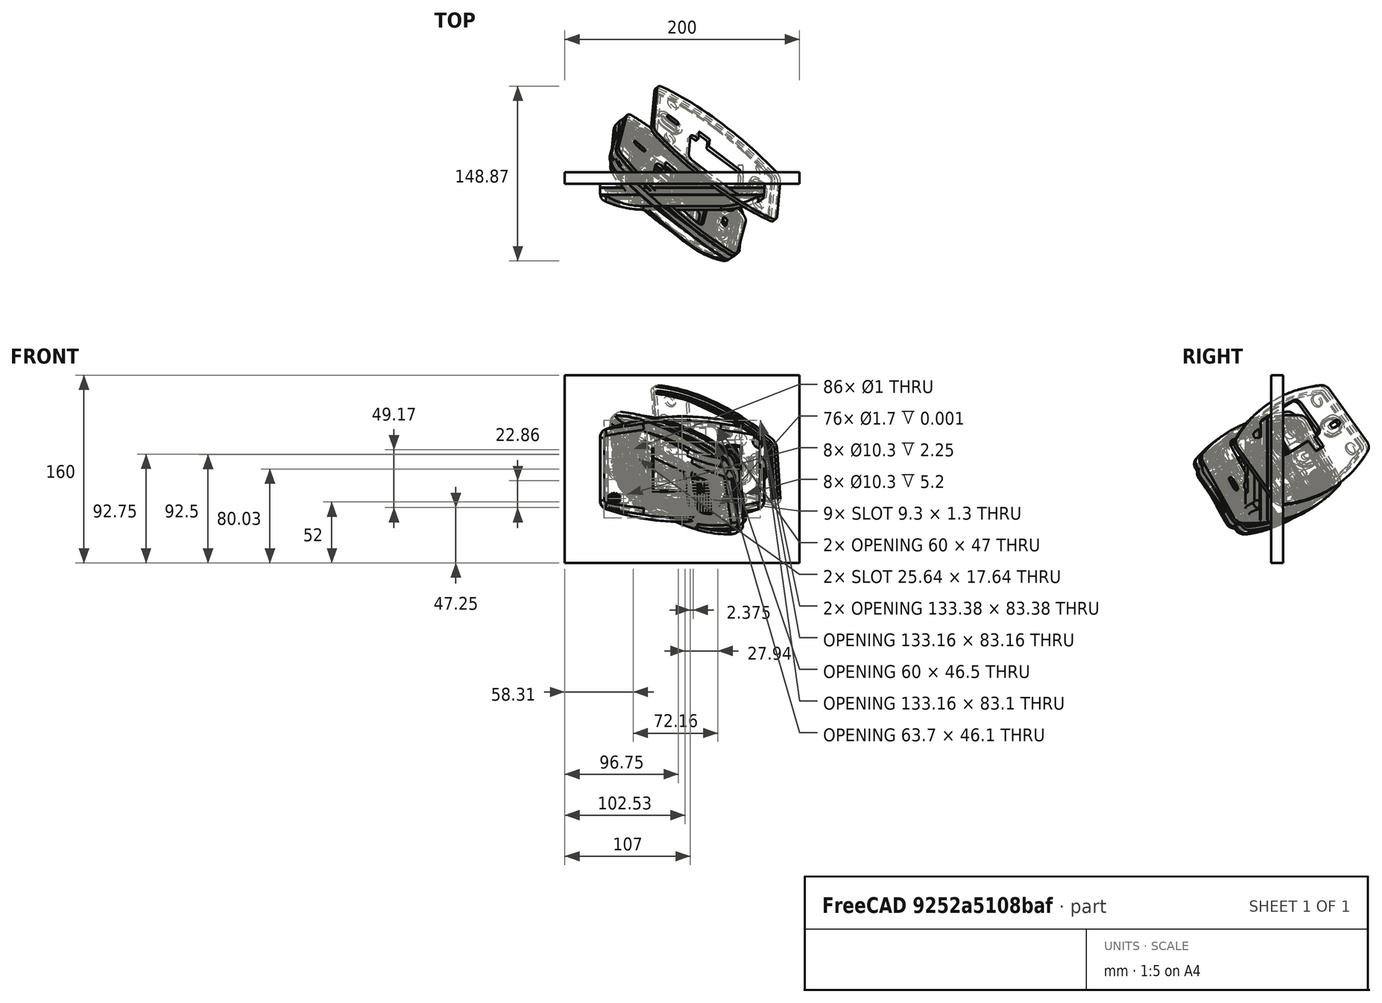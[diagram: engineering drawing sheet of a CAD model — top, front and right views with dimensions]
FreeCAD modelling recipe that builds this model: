
FCSTD DOCUMENT  (FreeCAD 0.19R24291 (Git))
Label: _RoomThermostat
License: All rights reserved
LicenseURL: http://en.wikipedia.org/wiki/All_rights_reserved
objects: Sketcher::SketchObject×100, PartDesign::Pocket×28, PartDesign::Body×26, Part::Feature×23, PartDesign::Pad×20, PartDesign::Mirrored×16, PartDesign::Revolution×11, Part::FeaturePython×10, PartDesign::LinearPattern×6, Part::Compound×6, PartDesign::SubtractivePipe×6, PartDesign::MultiTransform×5, PartDesign::Fillet×5, PartDesign::SubtractiveLoft×5, PartDesign::AdditivePipe×4, PartDesign::Groove×4, PartDesign::PolarPattern×4, PartDesign::AdditiveLoft×3, Drawing::FeatureViewPart×3, PartDesign::Plane×2, +2 more types
note: 371 computed .brp shape members not serialized (recipe doc carries the construction recipe); baked Part::Feature solids carry a one-line shape summary decoded from their .brp

FEATURE [Part::Feature] Part__Feature  label="MH-ET_LIVE_MiniKit"
  Placement = pos=(16.5,-5,-21) rot=(0,0,1;3.14159rad)
  shape: bbox 31.02 x 99.68 x 39.44 mm, 5494 faces, 23 solids (baked)
FEATURE [Sketcher::SketchObject] Sketch  label="gl base"
  FullyConstrained = false
  MapMode = 5
  Placement = pos=(0,0,0) rot=(1,0,0;1.5708rad)
  Support = -> [XZ_Plane]
  sketch-geometry (8):
    g0: LineSegment StartX=-33.28 StartY=21.36 StartZ=0 EndX=26.98 EndY=21.36 EndZ=0
    g1: LineSegment StartX=26.98 StartY=21.36 StartZ=0 EndX=26.98 EndY=-21.36 EndZ=0
    g2: LineSegment StartX=26.98 StartY=-21.36 StartZ=0 EndX=-33.28 EndY=-21.36 EndZ=0
    g3: LineSegment StartX=-33.28 StartY=-21.36 StartZ=0 EndX=-33.28 EndY=21.36 EndZ=0
    g4: LineSegment StartX=-24.48 StartY=18.36 StartZ=0 EndX=24.48 EndY=18.36 EndZ=0
    g5: LineSegment StartX=24.48 StartY=18.36 StartZ=0 EndX=24.48 EndY=-18.36 EndZ=0
    g6: LineSegment StartX=24.48 StartY=-18.36 StartZ=0 EndX=-24.48 EndY=-18.36 EndZ=0
    g7: LineSegment StartX=-24.48 StartY=-18.36 StartZ=0 EndX=-24.48 EndY=18.36 EndZ=0
  constraints (21):
    c: Coincident(g0,g1)
    c: Coincident(g1,g2)
    c: Coincident(g2,g3)
    c: Coincident(g3,g0)
    c: Horizontal(g2)
    c: Vertical(g3)
    c: DistanceX(g0,g0) = 60.26
    c: DistanceY(g1,g1) = 42.72
    c: Coincident(g4,g5)
    c: Coincident(g5,g6)
    c: Coincident(g6,g7)
    c: Coincident(g7,g4)
    c: Horizontal(g6)
    c: Vertical(g7)
    c: Horizontal(g0)
    c: Symmetric(g4,g4,g-2)
    c: Symmetric(g4,g5,g-1)
    c: DistanceX(g4,g4) = 48.96
    c: DistanceX(g4,g0) = 2.5
    c: DistanceY(g5,g5) = 36.72
    c: Symmetric(g0,g1,g-1)
FEATURE [PartDesign::Pad] Pad  label="GL Base"
  Direction = (1,1,1)
  Length = 4.2
  Length2 = 100
  Placement = pos=(0,0,0) rot=(1,0,0;1.5708rad)
  Profile = -> Sketch
  Reversed = true
  Type = 0
FEATURE [Sketcher::SketchObject] Sketch001  label="gl active area"
  FullyConstrained = false
  MapMode = 5
  Placement = pos=(0,0,0) rot=(1,0,0;1.5708rad)
  Support = -> [XZ_Plane]
  sketch-geometry (4):
    g0: LineSegment StartX=-24.48 StartY=18.36 StartZ=0 EndX=24.48 EndY=18.36 EndZ=0
    g1: LineSegment StartX=24.48 StartY=18.36 StartZ=0 EndX=24.48 EndY=-18.36 EndZ=0
    g2: LineSegment StartX=24.48 StartY=-18.36 StartZ=0 EndX=-24.48 EndY=-18.36 EndZ=0
    g3: LineSegment StartX=-24.48 StartY=-18.36 StartZ=0 EndX=-24.48 EndY=18.36 EndZ=0
  constraints (10):
    c: Coincident(g0,g1)
    c: Coincident(g1,g2)
    c: Coincident(g2,g3)
    c: Coincident(g3,g0)
    c: Horizontal(g2)
    c: Vertical(g3)
    c: Symmetric(g0,g0,g-2)
    c: Symmetric(g0,g1,g-1)
    c: DistanceY(g1,g1) = 36.72
    c: DistanceX(g0,g0) = 48.96
FEATURE [PartDesign::Pad] Pad001  label="GL active area"
  BaseFeature = -> Pad
  Direction = (1,1,1)
  Length = 0.1
  Length2 = 100
  Placement = pos=(0,0,0) rot=(1,0,0;1.5708rad)
  Profile = -> Sketch001
  Type = 0
FEATURE [PartDesign::Body] Body  label="Glass"
  Group = -> [Sketch,Pad,Sketch001,Pad001]
  Origin = -> Origin
  Tip = -> Pad001
FEATURE [Sketcher::SketchObject] Sketch003  label="pc skeleton"
  FullyConstrained = false
  MapMode = 5
  Placement = pos=(0,0,0) rot=(1,0,0;1.5708rad)
  Support = -> [XZ_Plane001]
  sketch-geometry (8):
    g0: LineSegment StartX=-33.28 StartY=21.36 StartZ=0 EndX=26.98 EndY=21.36 EndZ=0
    g1: LineSegment StartX=26.98 StartY=21.36 StartZ=0 EndX=26.98 EndY=-21.36 EndZ=0
    g2: LineSegment StartX=26.98 StartY=-21.36 StartZ=0 EndX=-33.28 EndY=-21.36 EndZ=0
    g3: LineSegment StartX=-33.28 StartY=-21.36 StartZ=0 EndX=-33.28 EndY=21.36 EndZ=0
    g4: LineSegment StartX=-24.48 StartY=18.36 StartZ=0 EndX=24.48 EndY=18.36 EndZ=0
    g5: LineSegment StartX=24.48 StartY=18.36 StartZ=0 EndX=24.48 EndY=-18.36 EndZ=0
    g6: LineSegment StartX=24.48 StartY=-18.36 StartZ=0 EndX=-24.48 EndY=-18.36 EndZ=0
    g7: LineSegment StartX=-24.48 StartY=-18.36 StartZ=0 EndX=-24.48 EndY=18.36 EndZ=0
  constraints (21):
    c: Coincident(g0,g1)
    c: Coincident(g1,g2)
    c: Coincident(g2,g3)
    c: Coincident(g3,g0)
    c: Horizontal(g2)
    c: Vertical(g3)
    c: DistanceX(g0,g0) = 60.26
    c: DistanceY(g1,g1) = 42.72
    c: Coincident(g4,g5)
    c: Coincident(g5,g6)
    c: Coincident(g6,g7)
    c: Coincident(g7,g4)
    c: Horizontal(g6)
    c: Vertical(g7)
    c: Horizontal(g0)
    c: Symmetric(g4,g4,g-2)
    c: Symmetric(g4,g5,g-1)
    c: DistanceX(g4,g4) = 48.96
    c: DistanceX(g4,g0) = 2.5
    c: DistanceY(g5,g5) = 36.72
    c: Symmetric(g0,g1,g-1)
FEATURE [Sketcher::SketchObject] Sketch002  label="pc base"
  AttachmentOffset = pos=(0,0,-4.2) rot=(0,0,1;0rad)
  ExternalGeometry = -> [Sketch003]
  FullyConstrained = false
  MapMode = 5
  Placement = pos=(0,4.2,9e-16) rot=(1,0,0;1.5708rad)
  Support = -> [XZ_Plane001]
  sketch-geometry (12):
    g0: LineSegment StartX=33.49 StartY=21.45 StartZ=0 EndX=-43.69 EndY=21.45 EndZ=0
    g1: LineSegment StartX=-43.69 StartY=21.45 StartZ=0 EndX=-43.69 EndY=-21.45 EndZ=0
    g2: LineSegment StartX=-43.69 StartY=-21.45 StartZ=0 EndX=33.49 EndY=-21.45 EndZ=0
    g3: LineSegment StartX=33.49 StartY=-21.45 StartZ=0 EndX=33.49 EndY=21.45 EndZ=0
    g4: LineSegment StartX=-36.77 StartY=18.45 StartZ=0 EndX=30.49 EndY=18.45 EndZ=0
    g5: LineSegment StartX=30.49 StartY=18.45 StartZ=0 EndX=30.49 EndY=-18.45 EndZ=0
    g6: LineSegment StartX=30.49 StartY=-18.45 StartZ=0 EndX=-36.77 EndY=-18.45 EndZ=0
    g7: LineSegment StartX=-36.77 StartY=-18.45 StartZ=0 EndX=-36.77 EndY=18.45 EndZ=0
    g8: Circle CenterX=30.49 CenterY=18.45 CenterZ=0 NormalX=0 NormalY=0 NormalZ=1 AngleXU=0 Radius=1.5
    g9: Circle CenterX=30.49 CenterY=-18.45 CenterZ=0 NormalX=0 NormalY=0 NormalZ=1 AngleXU=0 Radius=1.5
    g10: Circle CenterX=-36.77 CenterY=-18.45 CenterZ=0 NormalX=0 NormalY=0 NormalZ=1 AngleXU=0 Radius=1.5
    g11: Circle CenterX=-36.77 CenterY=18.45 CenterZ=0 NormalX=0 NormalY=0 NormalZ=1 AngleXU=0 Radius=1.5
  constraints (30):
    c: Coincident(g0,g1)
    c: Coincident(g1,g2)
    c: Coincident(g2,g3)
    c: Coincident(g3,g0)
    c: Horizontal(g0)
    c: Horizontal(g2)
    c: Vertical(g1)
    c: Symmetric(g0,g2,g-1)
    c: DistanceX(g0,g-3) = 10.41
    c: DistanceX(g0,g0) = 77.18
    c: DistanceY(g3,g3) = 42.9
    c: Coincident(g4,g5)
    c: Coincident(g5,g6)
    c: Coincident(g6,g7)
    c: Coincident(g7,g4)
    c: Horizontal(g4)
    c: Horizontal(g6)
    c: Vertical(g7)
    c: Symmetric(g4,g5,g-1)
    c: Coincident(g8,g4)
    c: Coincident(g9,g5)
    c: Coincident(g10,g6)
    c: Coincident(g11,g4)
    c: Equal(g8,g11)
    c: Equal(g11,g10)
    c: Equal(g10,g9)
    c: Radius(g9) = 1.5
    c: DistanceX(g0,g11) = 6.92
    c: DistanceX(g8,g0) = 3
    c: DistanceY(g8,g0) = 3
FEATURE [PartDesign::Pad] Pad002  label="PC base"
  Direction = (1,1,1)
  Length = 1.6
  Length2 = 100
  Placement = pos=(0,0,0) rot=(1,0,0;1.5708rad)
  Profile = -> Sketch002
  Reversed = true
  Type = 0
FEATURE [Sketcher::SketchObject] Sketch004  label="pc hole"
  ExternalGeometry = -> [Sketch002]
  FullyConstrained = false
  MapMode = 5
  Placement = pos=(0,0,0) rot=(1,0,0;1.5708rad)
  Support = -> [XZ_Plane001]
  sketch-geometry (1):
    g0: Circle CenterX=-41.69 CenterY=-16.6 CenterZ=0 NormalX=0 NormalY=0 NormalZ=1 AngleXU=0 Radius=0.5
  constraints (3):
    c: DistanceX(g-3,g0) = 2
    c: DistanceY(g-3,g0) = 4.85
    c: Radius(g0) = 0.5
FEATURE [PartDesign::Pocket] Pocket  label="PC FirstHole"
  BaseFeature = -> Pad002
  Length = 5
  Length2 = 100
  Midplane = true
  Placement = pos=(0,0,0) rot=(1,0,0;1.5708rad)
  Profile = -> Sketch004
  Type = 1
FEATURE [PartDesign::LinearPattern] LinearPattern  label="PC OtherHoles"
  BaseFeature = -> Pocket
  Direction = -> Z_Axis001
  Length = 33.02
  Occurrences = 14
  Originals = -> [Pocket]
  Placement = pos=(0,0,0) rot=(1,0,0;1.5708rad)
FEATURE [PartDesign::Body] Body001  label="PCB"
  Group = -> [Sketch002,Sketch003,Pad002,Sketch004,Pocket,LinearPattern]
  Origin = -> Origin001
  Tip = -> LinearPattern
FEATURE [Sketcher::SketchObject] Sketch006  label="sd skeleton"
  FullyConstrained = false
  MapMode = 5
  Placement = pos=(0,0,0) rot=(1,0,0;1.5708rad)
  Support = -> [XZ_Plane002]
  sketch-geometry (8):
    g0: LineSegment StartX=-33.28 StartY=21.36 StartZ=0 EndX=26.98 EndY=21.36 EndZ=0
    g1: LineSegment StartX=26.98 StartY=21.36 StartZ=0 EndX=26.98 EndY=-21.36 EndZ=0
    g2: LineSegment StartX=26.98 StartY=-21.36 StartZ=0 EndX=-33.28 EndY=-21.36 EndZ=0
    g3: LineSegment StartX=-33.28 StartY=-21.36 StartZ=0 EndX=-33.28 EndY=21.36 EndZ=0
    g4: LineSegment StartX=-24.48 StartY=18.36 StartZ=0 EndX=24.48 EndY=18.36 EndZ=0
    g5: LineSegment StartX=24.48 StartY=18.36 StartZ=0 EndX=24.48 EndY=-18.36 EndZ=0
    g6: LineSegment StartX=24.48 StartY=-18.36 StartZ=0 EndX=-24.48 EndY=-18.36 EndZ=0
    g7: LineSegment StartX=-24.48 StartY=-18.36 StartZ=0 EndX=-24.48 EndY=18.36 EndZ=0
  constraints (21):
    c: Coincident(g0,g1)
    c: Coincident(g1,g2)
    c: Coincident(g2,g3)
    c: Coincident(g3,g0)
    c: Horizontal(g2)
    c: Vertical(g3)
    c: DistanceX(g0,g0) = 60.26
    c: DistanceY(g1,g1) = 42.72
    c: Coincident(g4,g5)
    c: Coincident(g5,g6)
    c: Coincident(g6,g7)
    c: Coincident(g7,g4)
    c: Horizontal(g6)
    c: Vertical(g7)
    c: Horizontal(g0)
    c: Symmetric(g4,g4,g-2)
    c: Symmetric(g4,g5,g-1)
    c: DistanceX(g4,g4) = 48.96
    c: DistanceX(g4,g0) = 2.5
    c: DistanceY(g5,g5) = 36.72
    c: Symmetric(g0,g1,g-1)
FEATURE [Sketcher::SketchObject] Sketch005  label="sd base"
  AttachmentOffset = pos=(0,0,-5.8) rot=(0,0,1;0rad)
  ExternalGeometry = -> [Sketch006]
  FullyConstrained = false
  MapMode = 5
  Placement = pos=(0,5.8,1.3e-15) rot=(1,0,0;1.5708rad)
  Support = -> [XZ_Plane002]
  sketch-geometry (6):
    g0: LineSegment StartX=-16.02 StartY=19.96 StartZ=0 EndX=10.58 EndY=19.96 EndZ=0
    g1: LineSegment StartX=10.58 StartY=19.96 StartZ=0 EndX=10.58 EndY=10.96 EndZ=0
    g2: LineSegment StartX=8.48 StartY=3.26 StartZ=0 EndX=-16.02 EndY=3.26 EndZ=0
    g3: LineSegment StartX=-16.02 StartY=3.26 StartZ=0 EndX=-16.02 EndY=19.96 EndZ=0
    g4: LineSegment StartX=10.58 StartY=10.96 StartZ=0 EndX=8.48 EndY=8.86 EndZ=0
    g5: LineSegment StartX=8.48 StartY=8.86 StartZ=0 EndX=8.48 EndY=3.26 EndZ=0
  constraints (18):
    c: Coincident(g0,g1)
    c: Coincident(g2,g3)
    c: Coincident(g3,g0)
    c: Horizontal(g0)
    c: Horizontal(g2)
    c: Vertical(g1)
    c: Vertical(g3)
    c: DistanceX(g0,g-3) = 16.4
    c: DistanceX(g0,g0) = 26.6
    c: DistanceY(g0,g-3) = 1.4
    c: Coincident(g4,g5)
    c: Vertical(g5)
    c: Coincident(g2,g5)
    c: Coincident(g4,g1)
    c: DistanceY(g2,g0) = 16.7
    c: DistanceX(g2,g2) = 24.5
    c: DistanceY(g5,g5) = 5.6
    c: Angle(g5,g4) = 2.35619
FEATURE [PartDesign::Pad] Pad003  label="SD Base"
  Direction = (1,1,1)
  Length = 2.9
  Length2 = 100
  Placement = pos=(0,0,0) rot=(1,0,0;1.5708rad)
  Profile = -> Sketch005
  Reversed = true
  Type = 0
FEATURE [PartDesign::Body] Body002  label="SD Card Slot"
  Group = -> [Sketch005,Sketch006,Pad003]
  Origin = -> Origin002
  Tip = -> Pad003
FEATURE [Sketcher::SketchObject] Sketch009  label="cm skeleton"
  AttachmentOffset = pos=(0,0,-4.2) rot=(0,0,1;0rad)
  ExternalGeometry = -> [Sketch003]
  FullyConstrained = false
  MapMode = 5
  Placement = pos=(0,4.2,9e-16) rot=(1,0,0;1.5708rad)
  Support = -> [XZ_Plane003]
  sketch-geometry (12):
    g0: LineSegment StartX=33.49 StartY=21.45 StartZ=0 EndX=-43.69 EndY=21.45 EndZ=0
    g1: LineSegment StartX=-43.69 StartY=21.45 StartZ=0 EndX=-43.69 EndY=-21.45 EndZ=0
    g2: LineSegment StartX=-43.69 StartY=-21.45 StartZ=0 EndX=33.49 EndY=-21.45 EndZ=0
    g3: LineSegment StartX=33.49 StartY=-21.45 StartZ=0 EndX=33.49 EndY=21.45 EndZ=0
    g4: LineSegment StartX=-36.77 StartY=18.45 StartZ=0 EndX=30.49 EndY=18.45 EndZ=0
    g5: LineSegment StartX=30.49 StartY=18.45 StartZ=0 EndX=30.49 EndY=-18.45 EndZ=0
    g6: LineSegment StartX=30.49 StartY=-18.45 StartZ=0 EndX=-36.77 EndY=-18.45 EndZ=0
    g7: LineSegment StartX=-36.77 StartY=-18.45 StartZ=0 EndX=-36.77 EndY=18.45 EndZ=0
    g8: Circle CenterX=30.49 CenterY=18.45 CenterZ=0 NormalX=0 NormalY=0 NormalZ=1 AngleXU=0 Radius=1.5
    g9: Circle CenterX=30.49 CenterY=-18.45 CenterZ=0 NormalX=0 NormalY=0 NormalZ=1 AngleXU=0 Radius=1.5
    g10: Circle CenterX=-36.77 CenterY=-18.45 CenterZ=0 NormalX=0 NormalY=0 NormalZ=1 AngleXU=0 Radius=1.5
    g11: Circle CenterX=-36.77 CenterY=18.45 CenterZ=0 NormalX=0 NormalY=0 NormalZ=1 AngleXU=0 Radius=1.5
  constraints (30):
    c: Coincident(g0,g1)
    c: Coincident(g1,g2)
    c: Coincident(g2,g3)
    c: Coincident(g3,g0)
    c: Horizontal(g0)
    c: Horizontal(g2)
    c: Vertical(g1)
    c: Symmetric(g0,g2,g-1)
    c: DistanceX(g0,g-3) = 10.41
    c: DistanceX(g0,g0) = 77.18
    c: DistanceY(g3,g3) = 42.9
    c: Coincident(g4,g5)
    c: Coincident(g5,g6)
    c: Coincident(g6,g7)
    c: Coincident(g7,g4)
    c: Horizontal(g4)
    c: Horizontal(g6)
    c: Vertical(g7)
    c: Symmetric(g4,g5,g-1)
    c: Coincident(g8,g4)
    c: Coincident(g9,g5)
    c: Coincident(g10,g6)
    c: Coincident(g11,g4)
    c: Equal(g8,g11)
    c: Equal(g11,g10)
    c: Equal(g10,g9)
    c: Radius(g9) = 1.5
    c: DistanceX(g0,g11) = 6.92
    c: DistanceX(g8,g0) = 3
    c: DistanceY(g8,g0) = 3
FEATURE [Sketcher::SketchObject] Sketch010  label="cm components"
  AttachmentOffset = pos=(0,0,-5.8) rot=(0,0,1;0rad)
  ExternalGeometry = -> [Sketch009]
  FullyConstrained = false
  MapMode = 5
  Placement = pos=(0,5.8,1.3e-15) rot=(1,0,0;1.5708rad)
  Support = -> [XZ_Plane003]
  sketch-geometry (4):
    g0: LineSegment StartX=-27.99 StartY=2.05 StartZ=0 EndX=6.01 EndY=2.05 EndZ=0
    g1: LineSegment StartX=6.01 StartY=2.05 StartZ=0 EndX=6.01 EndY=-17.45 EndZ=0
    g2: LineSegment StartX=6.01 StartY=-17.45 StartZ=0 EndX=-27.99 EndY=-17.45 EndZ=0
    g3: LineSegment StartX=-27.99 StartY=-17.45 StartZ=0 EndX=-27.99 EndY=2.05 EndZ=0
  constraints (12):
    c: Coincident(g0,g1)
    c: Coincident(g1,g2)
    c: Coincident(g2,g3)
    c: Coincident(g3,g0)
    c: Horizontal(g0)
    c: Horizontal(g2)
    c: Vertical(g1)
    c: Vertical(g3)
    c: DistanceX(g-3,g2) = 15.7
    c: DistanceX(g0,g0) = 34
    c: DistanceY(g-3,g2) = 4
    c: DistanceY(g1,g1) = 19.5
FEATURE [PartDesign::Pad] Pad004
  Direction = (1,1,1)
  Length = 1
  Length2 = 100
  Placement = pos=(0,0,0) rot=(1,0,0;1.5708rad)
  Profile = -> Sketch010
  Reversed = true
  Type = 0
FEATURE [PartDesign::Body] Body003  label="Components"
  Group = -> [Sketch009,Sketch010,Pad004]
  Origin = -> Origin003
  Tip = -> Pad004
FEATURE [Part::Compound] Compound  label="Display"
  Links = -> [Body,Body001,Body002,Body003]
  Placement = pos=(0,-20.5,0) rot=(0,0,1;0rad)
FEATURE [Part::FeaturePython] Screw  label="M5x10-Screw"  # Fasteners workbench fastener (typed FeaturePython)
  Placement = pos=(41,-20,14) rot=(1,0,0;1.5708rad)
  diameter = 3
  invert = false
  length = 1
  lengthCustom = 10
  matchOuter = false
  offset = 0
  thread = false
  type = 38
FEATURE [Part::FeaturePython] Nut  label="M5-Nut"  # Fasteners workbench fastener (typed FeaturePython)
  Placement = pos=(41,-13,14) rot=(-1,0,0;1.5708rad)
  diameter = 7
  invert = false
  matchOuter = false
  offset = 0
  thread = false
  type = 7
FEATURE [Part::FeaturePython] Screw001  label="M5x10-Screw005"  # Fasteners workbench fastener (typed FeaturePython)
  Placement = pos=(41,-20,0) rot=(1,0,0;1.5708rad)
  diameter = 3
  invert = false
  length = 1
  lengthCustom = 10
  matchOuter = false
  offset = 0
  thread = false
  type = 38
FEATURE [Part::FeaturePython] Nut001  label="M5-Nut017"  # Fasteners workbench fastener (typed FeaturePython)
  Placement = pos=(41,-13,0) rot=(-1,0,0;1.5708rad)
  diameter = 7
  invert = false
  matchOuter = false
  offset = 0
  thread = false
  type = 7
FEATURE [Part::FeaturePython] Screw002  label="M5x10-Screw006"  # Fasteners workbench fastener (typed FeaturePython)
  Placement = pos=(41,-20,-14) rot=(1,0,0;1.5708rad)
  diameter = 3
  invert = false
  length = 1
  lengthCustom = 10
  matchOuter = false
  offset = 0
  thread = false
  type = 38
FEATURE [Part::FeaturePython] Nut002  label="M5-Nut018"  # Fasteners workbench fastener (typed FeaturePython)
  Placement = pos=(41,-13,-14) rot=(-1,0,0;1.5708rad)
  diameter = 7
  invert = false
  matchOuter = false
  offset = 0
  thread = false
  type = 7
FEATURE [Sketcher::SketchObject] Sketch017
  FullyConstrained = false
  MapMode = 5
  Placement = pos=(0,0,0) rot=(1,0,0;1.5708rad)
  Support = -> [XZ_Plane005]
  sketch-geometry (6):
    g0: LineSegment StartX=-100 StartY=80 StartZ=0 EndX=100 EndY=80 EndZ=0
    g1: LineSegment StartX=100 StartY=80 StartZ=0 EndX=100 EndY=-80 EndZ=0
    g2: LineSegment StartX=100 StartY=-80 StartZ=0 EndX=-100 EndY=-80 EndZ=0
    g3: LineSegment StartX=-100 StartY=-80 StartZ=0 EndX=-100 EndY=80 EndZ=0
    g4: Circle CenterX=-50 CenterY=0 CenterZ=0 NormalX=0 NormalY=0 NormalZ=1 AngleXU=0 Radius=2
    g5: Circle CenterX=50 CenterY=0 CenterZ=0 NormalX=0 NormalY=0 NormalZ=1 AngleXU=0 Radius=2
  constraints (15):
    c: Coincident(g0,g1)
    c: Coincident(g1,g2)
    c: Coincident(g2,g3)
    c: Coincident(g3,g0)
    c: Horizontal(g2)
    c: Vertical(g3)
    c: Symmetric(g0,g1,g-1)
    c: Symmetric(g0,g0,g-2)
    c: DistanceX(g0,g0) = 200
    c: DistanceY(g3,g3) = 160
    c: PointOnObject(g4,g-1)
    c: Symmetric(g5,g4,g-2)
    c: Radius(g5) = 2
    c: Equal(g5,g4)
    c: DistanceX(g4,g5) = 100
FEATURE [PartDesign::Pad] Pad006
  Direction = (1,1,1)
  Length = 10
  Length2 = 100
  Placement = pos=(0,0,0) rot=(1,0,0;1.5708rad)
  Profile = -> Sketch017
  Reversed = true
  Type = 0
FEATURE [Sketcher::SketchObject] Sketch018
  FullyConstrained = false
  MapMode = 5
  Placement = pos=(0,0,0) rot=(1,0,0;1.5708rad)
  Support = -> [XZ_Plane005]
  sketch-geometry (4):
    g0: LineSegment StartX=-20 StartY=35 StartZ=0 EndX=20 EndY=35 EndZ=0
    g1: LineSegment StartX=20 StartY=35 StartZ=0 EndX=20 EndY=0 EndZ=0
    g2: LineSegment StartX=20 StartY=0 StartZ=0 EndX=-20 EndY=0 EndZ=0
    g3: LineSegment StartX=-20 StartY=0 StartZ=0 EndX=-20 EndY=35 EndZ=0
  constraints (11):
    c: Coincident(g0,g1)
    c: Coincident(g1,g2)
    c: Coincident(g2,g3)
    c: Coincident(g3,g0)
    c: Horizontal(g2)
    c: Vertical(g1)
    c: Vertical(g3)
    c: PointOnObject(g1,g-1)
    c: Symmetric(g0,g0,g-2)
    c: DistanceX(g0,g0) = 40
    c: DistanceY(g3,g3) = 35
FEATURE [PartDesign::Pad] Pad007
  BaseFeature = -> Pad006
  Direction = (1,1,1)
  Length = 2
  Length2 = 100
  Placement = pos=(0,0,0) rot=(1,0,0;1.5708rad)
  Profile = -> Sketch018
  Type = 0
FEATURE [PartDesign::Body] Body005  label="Wall"
  Group = -> [Sketch017,Pad006,Sketch018,Pad007]
  Origin = -> Origin005
  Placement = pos=(0,0.01,0) rot=(0,0,1;0rad)
  Tip = -> Pad007
FEATURE [Sketcher::SketchObject] Sketch019
  FullyConstrained = false
  MapMode = 5
  Support = -> [XY_Plane006]
  sketch-geometry (8):
    g0: LineSegment StartX=-2.65 StartY=3.15 StartZ=0 EndX=2.65 EndY=3.15 EndZ=0
    g1: LineSegment StartX=4.65 StartY=1.15 StartZ=0 EndX=4.65 EndY=-1.15 EndZ=0
    g2: LineSegment StartX=2.65 StartY=-3.15 StartZ=0 EndX=-2.65 EndY=-3.15 EndZ=0
    g3: LineSegment StartX=-4.65 StartY=-1.15 StartZ=0 EndX=-4.65 EndY=1.15 EndZ=0
    g4: ArcOfCircle CenterX=2.65 CenterY=-1.15 CenterZ=0 NormalX=0 NormalY=0 NormalZ=1 AngleXU=0 Radius=2 StartAngle=4.71239 EndAngle=6.28319
    g5: ArcOfCircle CenterX=2.65 CenterY=1.15 CenterZ=0 NormalX=0 NormalY=0 NormalZ=1 AngleXU=0 Radius=2 StartAngle=0 EndAngle=1.5708
    g6: ArcOfCircle CenterX=-2.65 CenterY=1.15 CenterZ=0 NormalX=0 NormalY=0 NormalZ=1 AngleXU=0 Radius=2 StartAngle=1.5708 EndAngle=3.14159
    g7: ArcOfCircle CenterX=-2.65 CenterY=-1.15 CenterZ=0 NormalX=0 NormalY=0 NormalZ=1 AngleXU=0 Radius=2 StartAngle=3.14159 EndAngle=4.71239
  constraints (18):
    c: Horizontal(g2)
    c: Vertical(g1)
    c: Vertical(g3)
    c: Tangent(g2,g4) = 1.5708
    c: Tangent(g1,g4) = 1.5708
    c: Tangent(g1,g5) = 1.5708
    c: Tangent(g0,g5) = 1.5708
    c: Tangent(g0,g6) = 1.5708
    c: Tangent(g3,g6) = 1.5708
    c: Tangent(g3,g7) = 1.5708
    c: Tangent(g2,g7) = 1.5708
    c: Equal(g7,g4)
    c: Equal(g5,g6)
    c: DistanceX(g3,g1) = 9.3
    c: DistanceY(g2,g0) = 6.3
    c: Radius(g5) = 2
    c: Symmetric(g4,g5,g-1)
    c: Symmetric(g5,g6,g-2)
FEATURE [PartDesign::Pad] Pad008
  AllowMultiFace = false
  Direction = (1,1,1)
  Length = 13
  Length2 = 100
  Profile = -> Sketch019
  Type = 0
FEATURE [PartDesign::Body] Body006  label="USB connector"
  Group = -> [Sketch019,Pad008]
  Origin = -> Origin006
  Placement = pos=(17,-7,0.25) rot=(0,0,1;3.14159rad)
  Tip = -> Pad008
FEATURE [Sketcher::SketchObject] Sketch022  label="wp cut around trj"
  FullyConstrained = false
  MapMode = 5
  Placement = pos=(0,0,0) rot=(1,0,0;1.5708rad)
  sketch-geometry (13):
    g0: LineSegment StartX=70 StartY=26.7141 StartZ=0 EndX=70 EndY=-26.7141 EndZ=0
    g1: LineSegment StartX=-70 StartY=-26.7141 StartZ=0 EndX=-70 EndY=26.7141 EndZ=0
    g2: ArcOfCircle CenterX=62 CenterY=26.7141 CenterZ=0 NormalX=0 NormalY=0 NormalZ=1 AngleXU=0 Radius=8 StartAngle=0 EndAngle=1.24199
    g3: ArcOfCircle CenterX=-62 CenterY=26.7141 CenterZ=0 NormalX=0 NormalY=0 NormalZ=1 AngleXU=0 Radius=8 StartAngle=1.89961 EndAngle=3.14159
    g4: ArcOfCircle CenterX=-62 CenterY=-26.7141 CenterZ=0 NormalX=0 NormalY=0 NormalZ=1 AngleXU=0 Radius=8 StartAngle=3.14159 EndAngle=4.38358
    g5: ArcOfCircle CenterX=62 CenterY=-26.7141 CenterZ=0 NormalX=0 NormalY=0 NormalZ=1 AngleXU=0 Radius=8 StartAngle=5.0412 EndAngle=6.28319
    g6: LineSegment StartX=62 StartY=26.7141 StartZ=0 EndX=-62 EndY=26.7141 EndZ=0
    g7: LineSegment StartX=-62 StartY=26.7141 StartZ=0 EndX=-62 EndY=-26.7141 EndZ=0
    g8: LineSegment StartX=-62 StartY=-26.7141 StartZ=0 EndX=62 EndY=-26.7141 EndZ=0
    g9: LineSegment StartX=62 StartY=-26.7141 StartZ=0 EndX=62 EndY=26.7141 EndZ=0
    g10: ArcOfCircle CenterX=-7.2e-15 CenterY=-155 CenterZ=0 NormalX=0 NormalY=0 NormalZ=1 AngleXU=0 Radius=200 StartAngle=1.24199 EndAngle=1.89961
    g11: ArcOfCircle CenterX=-1.16e-14 CenterY=155 CenterZ=0 NormalX=0 NormalY=0 NormalZ=1 AngleXU=0 Radius=200 StartAngle=4.38358 EndAngle=5.0412
    g12: LineSegment StartX=0 StartY=45 StartZ=0 EndX=0 EndY=-45 EndZ=0
  constraints (32):
    c: Vertical(g0)
    c: Vertical(g1)
    c: Tangent(g0,g2) = 1.5708
    c: Tangent(g1,g3) = 1.5708
    c: Tangent(g1,g4) = 1.5708
    c: Tangent(g0,g5) = 1.5708
    c: Coincident(g6,g7)
    c: Coincident(g7,g8)
    c: Coincident(g8,g9)
    c: Coincident(g9,g6)
    c: Horizontal(g8)
    c: Coincident(g6,g2)
    c: Coincident(g7,g4)
    c: Coincident(g3,g6)
    c: Coincident(g5,g8)
    c: Symmetric(g5,g2,g-1)
    c: Symmetric(g2,g3,g-2)
    c: DistanceX(g1,g0) = 140
    c: Radius(g2) = 8
    c: Equal(g2,g3)
    c: Equal(g3,g4)
    c: Tangent(g4,g11) = -1.5708
    c: Tangent(g5,g11) = -1.5708
    c: Tangent(g2,g10) = -1.5708
    c: Tangent(g3,g10) = -1.5708
    c: Equal(g11,g10)
    c: Radius(g10) = 200
    c: PointOnObject(g12,g10)
    c: PointOnObject(g12,g11)
    c: Vertical(g12)
    c: DistanceY(g12,g12) = 90
    c: PointOnObject(g-1,g12)
FEATURE [Sketcher::SketchObject] Sketch023  label="wp cut around crs"
  FullyConstrained = false
  MapMode = 5
  Support = -> [XY_Plane007]
  sketch-geometry (5):
    g0: LineSegment StartX=70 StartY=0 StartZ=0 EndX=90 EndY=0 EndZ=0
    g1: LineSegment StartX=90 StartY=0 StartZ=0 EndX=90 EndY=-25 EndZ=0
    g2: LineSegment StartX=90 StartY=-25 StartZ=0 EndX=62 EndY=-25 EndZ=0
    g3: LineSegment StartX=70 StartY=-6 StartZ=0 EndX=70 EndY=0 EndZ=0
    g4: ArcOfCircle CenterX=43.4375 CenterY=-6 CenterZ=0 NormalX=0 NormalY=0 NormalZ=1 AngleXU=0 Radius=26.5625 StartAngle=5.48614 EndAngle=6.28319
  constraints (15):
    c: Coincident(g0,g1)
    c: Coincident(g1,g2)
    c: Coincident(g3,g0)
    c: Horizontal(g0)
    c: Horizontal(g2)
    c: Vertical(g1)
    c: Vertical(g3)
    c: PointOnObject(g0,g-1)
    c: Coincident(g2,g4)
    c: Tangent(g4,g3) = -1.5708
    c: DistanceX(g0) = 70
    c: DistanceY(g3,g3) = 6
    c: DistanceY(g1,g1) = 25
    c: DistanceX(g2,g3) = 8
    c: DistanceX(g0,g0) = 20
FEATURE [Sketcher::SketchObject] Sketch026  label="wp base"
  FullyConstrained = false
  MapMode = 5
  Support = -> [XY_Plane007]
  sketch-geometry (6):
    g0: LineSegment StartX=-71 StartY=0 StartZ=0 EndX=71 EndY=0 EndZ=0
    g1: LineSegment StartX=71 StartY=0 StartZ=0 EndX=71 EndY=-12 EndZ=0
    g2: LineSegment StartX=32.5 StartY=-20 StartZ=0 EndX=-32.5 EndY=-20 EndZ=0
    g3: LineSegment StartX=-71 StartY=-12 StartZ=0 EndX=-71 EndY=0 EndZ=0
    g4: ArcOfCircle CenterX=-32.5 CenterY=76.6406 CenterZ=0 NormalX=0 NormalY=0 NormalZ=1 AngleXU=0 Radius=96.6406 StartAngle=4.30264 EndAngle=4.71239
    g5: ArcOfCircle CenterX=32.5 CenterY=76.6406 CenterZ=0 NormalX=0 NormalY=0 NormalZ=1 AngleXU=0 Radius=96.6406 StartAngle=4.71239 EndAngle=5.12214
  constraints (16):
    c: Coincident(g0,g1)
    c: Coincident(g3,g0)
    c: Horizontal(g2)
    c: Vertical(g1)
    c: Vertical(g3)
    c: Tangent(g2,g4) = 1.5708
    c: Tangent(g2,g5) = 1.5708
    c: Symmetric(g5,g4,g-2)
    c: DistanceX(g4,g5) = 65
    c: Symmetric(g0,g0,g-2)
    c: DistanceX(g0,g0) = 142
    c: Coincident(g3,g4)
    c: Coincident(g1,g5)
    c: DistanceY(g2,g3) = 8
    c: DistanceY(g2,g0) = 20
    c: PointOnObject(g0,g-1)
FEATURE [PartDesign::Pad] Pad009  label="WP Base"
  Direction = (1,1,1)
  Length = 92
  Length2 = 100
  Midplane = true
  Profile = -> Sketch026
  Type = 0
FEATURE [Sketcher::SketchObject] Sketch027  label="wp separation wall plate"
  FullyConstrained = false
  MapMode = 5
  Placement = pos=(0,0,0) rot=(0.57735,0.57735,0.57735;2.0944rad)
  Support = -> [YZ_Plane007]
  sketch-geometry (4):
    g0: LineSegment StartX=-3 StartY=47.5 StartZ=0 EndX=-23 EndY=47.5 EndZ=0
    g1: LineSegment StartX=-23 StartY=47.5 StartZ=0 EndX=-23 EndY=-47.5 EndZ=0
    g2: LineSegment StartX=-23 StartY=-47.5 StartZ=0 EndX=-3 EndY=-47.5 EndZ=0
    g3: LineSegment StartX=-3 StartY=-47.5 StartZ=0 EndX=-3 EndY=47.5 EndZ=0
  constraints (11):
    c: Coincident(g0,g1)
    c: Coincident(g1,g2)
    c: Coincident(g2,g3)
    c: Coincident(g3,g0)
    c: Horizontal(g0)
    c: Horizontal(g2)
    c: Vertical(g3)
    c: DistanceX(g0,g-1) = 3
    c: Symmetric(g1,g0,g-1)
    c: DistanceX(g0,g0) = 20
    c: DistanceY(g1,g1) = 95
FEATURE [PartDesign::Pocket] Pocket003  label="WP Separation wall plate"
  BaseFeature = -> Pad009
  Length = 5
  Length2 = 100
  Midplane = true
  Profile = -> Sketch027
  Type = 1
FEATURE [PartDesign::SubtractivePipe] SubtractivePipe001  label="WP Cut around"
  AuxilleryCurvelinear = true
  AuxillerySpineTangent = false
  BaseFeature = -> Pocket003
  Binormal = (0,0,0)
  Mode = 0
  Profile = -> Sketch023
  Spine = -> Sketch022
  SpineTangent = false
  Transformation = 0
  Transition = 0
FEATURE [Part::FeaturePython] Screw003  label="M4x20-Screw"  # Fasteners workbench fastener (typed FeaturePython)
  Placement = pos=(50,-4,6e-15) rot=(0.57735,-0.57735,0.57735;2.0944rad)
  diameter = 6
  invert = false
  length = 7
  lengthCustom = 20
  matchOuter = false
  offset = 0
  thread = false
  type = 33
FEATURE [Sketcher::SketchObject] Sketch035  label="wp screw holes"
  FullyConstrained = false
  MapMode = 5
  Placement = pos=(0,0,0) rot=(1,0,0;1.5708rad)
  Support = -> [XZ_Plane007]
  sketch-geometry (30):
    g0: ArcOfCircle CenterX=-54 CenterY=0 CenterZ=0 NormalX=0 NormalY=0 NormalZ=1 AngleXU=0 Radius=2.3 StartAngle=1.5708 EndAngle=4.71239
    g1: ArcOfCircle CenterX=-46 CenterY=-1.40496e-11 CenterZ=0 NormalX=0 NormalY=0 NormalZ=1 AngleXU=0 Radius=2.3 StartAngle=4.71239 EndAngle=7.85398
    g2: LineSegment StartX=-54 StartY=-2.3 StartZ=0 EndX=-46 EndY=-2.3 EndZ=0
    g3: LineSegment StartX=-54 StartY=2.3 StartZ=0 EndX=-46 EndY=2.3 EndZ=0
    g4: LineSegment StartX=-50 StartY=2.3 StartZ=0 EndX=-50 EndY=-2.3 EndZ=0
    g5: ArcOfCircle CenterX=50 CenterY=4 CenterZ=0 NormalX=0 NormalY=0 NormalZ=1 AngleXU=0 Radius=2.3 StartAngle=-1.0937e-11 EndAngle=3.14159
    g6: ArcOfCircle CenterX=50 CenterY=-4 CenterZ=0 NormalX=0 NormalY=0 NormalZ=1 AngleXU=0 Radius=2.3 StartAngle=3.14159 EndAngle=6.28319
    g7: LineSegment StartX=47.7 StartY=4 StartZ=0 EndX=47.7 EndY=-4 EndZ=0
    g8: LineSegment StartX=52.3 StartY=4 StartZ=0 EndX=52.3 EndY=-4 EndZ=0
    g9: LineSegment StartX=-24 StartY=30 StartZ=0 EndX=24 EndY=30 EndZ=0
    g10: LineSegment StartX=24 StartY=30 StartZ=0 EndX=24 EndY=6 EndZ=0
    g11: LineSegment StartX=24 StartY=6 StartZ=0 EndX=-24 EndY=6 EndZ=0
    g12: LineSegment StartX=-24 StartY=6 StartZ=0 EndX=-24 EndY=30 EndZ=0
    g13: LineSegment StartX=30 StartY=30 StartZ=0 EndX=30 EndY=6 EndZ=0
    g14: LineSegment StartX=24 StartY=0 StartZ=0 EndX=-8 EndY=0 EndZ=0
    g15: LineSegment StartX=-21 StartY=-10 StartZ=0 EndX=-21 EndY=-1 EndZ=0
    g16: LineSegment StartX=-20 StartY=-11 StartZ=0 EndX=-10 EndY=-11 EndZ=0
    g17: LineSegment StartX=-9 StartY=-10 StartZ=0 EndX=-9 EndY=-1 EndZ=0
    g18: ArcOfCircle CenterX=-20 CenterY=-10 CenterZ=0 NormalX=0 NormalY=0 NormalZ=1 AngleXU=0 Radius=1 StartAngle=3.14159 EndAngle=4.71239
    g19: ArcOfCircle CenterX=-10 CenterY=-10 CenterZ=0 NormalX=0 NormalY=0 NormalZ=1 AngleXU=0 Radius=1 StartAngle=4.71239 EndAngle=6.28319
    g20: ArcOfCircle CenterX=-8 CenterY=-1 CenterZ=0 NormalX=0 NormalY=0 NormalZ=1 AngleXU=0 Radius=1 StartAngle=1.5708 EndAngle=3.14159
    g21: LineSegment StartX=-15 StartY=6 StartZ=0 EndX=-15 EndY=-11 EndZ=0
    g22: ArcOfCircle CenterX=24 CenterY=6 CenterZ=0 NormalX=0 NormalY=0 NormalZ=1 AngleXU=0 Radius=6 StartAngle=4.71239 EndAngle=6.28319
    g23: LineSegment StartX=-22 StartY=4.4e-15 StartZ=0 EndX=-24 EndY=4.4e-15 EndZ=0
    g24: LineSegment StartX=-30 StartY=6 StartZ=0 EndX=-30 EndY=30 EndZ=0
    g25: LineSegment StartX=-24 StartY=36 StartZ=0 EndX=24 EndY=36 EndZ=0
    g26: ArcOfCircle CenterX=-24 CenterY=30 CenterZ=0 NormalX=0 NormalY=0 NormalZ=1 AngleXU=0 Radius=6 StartAngle=1.5708 EndAngle=3.14159
    g27: ArcOfCircle CenterX=24 CenterY=30 CenterZ=0 NormalX=0 NormalY=0 NormalZ=1 AngleXU=0 Radius=6 StartAngle=0 EndAngle=1.5708
    g28: ArcOfCircle CenterX=-24 CenterY=6 CenterZ=0 NormalX=0 NormalY=0 NormalZ=1 AngleXU=0 Radius=6 StartAngle=3.14159 EndAngle=4.71239
    g29: ArcOfCircle CenterX=-22 CenterY=-1 CenterZ=0 NormalX=0 NormalY=0 NormalZ=1 AngleXU=0 Radius=1 StartAngle=0 EndAngle=1.5708
  constraints (72):
    c: Tangent(g0,g3)
    c: Tangent(g0,g2)
    c: Tangent(g2,g1)
    c: Tangent(g3,g1)
    c: Horizontal(g2)
    c: Equal(g0,g1)
    c: PointOnObject(g0,g-1)
    c: Radius(g1) = 2.3
    c: PointOnObject(g4,g3)
    c: PointOnObject(g4,g2)
    c: Symmetric(g1,g0,g4)
    c: DistanceX(g3,g3) = 8
    c: DistanceX(g4,g-1) = 50
    c: Tangent(g5,g8)
    c: Tangent(g5,g7)
    c: Tangent(g7,g6)
    c: Tangent(g8,g6)
    c: Vertical(g7)
    c: Symmetric(g6,g5,g-1)
    c: DistanceY(g6,g5) = 8
    c: Radius(g5) = 2.3
    c: DistanceX(g5) = 50
    c: Coincident(g10,g11)
    c: Coincident(g11,g12)
    c: Horizontal(g11)
    c: Vertical(g10)
    c: Vertical(g12)
    c: Symmetric(g9,g9,g-2)
    c: Horizontal(g14)
    c: Vertical(g13)
    c: Horizontal(g16)
    c: Vertical(g17)
    c: Tangent(g15,g18) = 1.5708
    c: Tangent(g16,g18) = -1.5708
    c: Tangent(g17,g19) = -1.5708
    c: Tangent(g16,g19) = -1.5708
    c: Tangent(g14,g20) = -1.5708
    c: Tangent(g17,g20) = 1.5708
    c: Equal(g19,g20)
    c: Equal(g20,g18)
    c: Vertical(g15)
    c: DistanceY(g16,g-1) = 11
    c: PointOnObject(g21,g11)
    c: PointOnObject(g21,g16)
    c: DistanceX(g21,g-1) = 15
    c: Symmetric(g19,g18,g21)
    c: DistanceX(g15,g17) = 12
    c: Radius(g19) = 1
    c: Tangent(g14,g22) = 1.5708
    c: Tangent(g13,g22) = 1.5708
    c: PointOnObject(g14,g-1)
    c: Vertical(g24)
    c: Horizontal(g25)
    c: Tangent(g25,g26) = 1.5708
    c: Tangent(g24,g26) = 1.5708
    c: Tangent(g25,g27) = 1.5708
    c: Tangent(g13,g27) = 1.5708
    c: Coincident(g9,g10)
    c: DistanceY(g14,g25) = 36
    c: DistanceX(g24,g13) = 60
    c: Radius(g27) = 6
    c: Coincident(g9,g27)
    c: Coincident(g9,g26)
    c: Coincident(g9,g12)
    c: Coincident(g10,g22)
    c: Tangent(g23,g28) = 1.5708
    c: Tangent(g24,g28) = 1.5708
    c: Coincident(g28,g11)
    c: Tangent(g23,g29) = -1.5708
    c: Tangent(g15,g29) = -1.5708
    c: Equal(g29,g19)
    c: Horizontal(g23)
FEATURE [PartDesign::Pocket] Pocket006  label="WP Screw holes"
  BaseFeature = -> SubtractivePipe001
  Length = 5
  Length2 = 100
  Midplane = true
  Profile = -> Sketch035
  Type = 1
FEATURE [Sketcher::SketchObject] Sketch036  label="wp seal rib crs"
  FullyConstrained = false
  MapMode = 5
  Support = -> [XY_Plane007]
  sketch-geometry (5):
    g0: LineSegment StartX=63.4216 StartY=-3 StartZ=0 EndX=66.5784 EndY=-3 EndZ=0
    g1: LineSegment StartX=66.5784 StartY=-3 StartZ=0 EndX=65.75 EndY=-5 EndZ=0
    g2: LineSegment StartX=65.75 StartY=-5 StartZ=0 EndX=64.25 EndY=-5 EndZ=0
    g3: LineSegment StartX=64.25 StartY=-5 StartZ=0 EndX=63.4216 EndY=-3 EndZ=0
    g4: LineSegment StartX=65 StartY=-5 StartZ=0 EndX=65 EndY=-3 EndZ=0
  constraints (14):
    c: Coincident(g0,g1)
    c: Coincident(g1,g2)
    c: Coincident(g2,g3)
    c: Coincident(g3,g0)
    c: Horizontal(g0)
    c: DistanceY(g0,g-1) = 3
    c: PointOnObject(g4,g2)
    c: PointOnObject(g4,g0)
    c: Symmetric(g0,g0,g4)
    c: Symmetric(g1,g2,g4)
    c: DistanceX(g2,g2) = 1.5
    c: Angle(g1,g3) = 0.785398
    c: DistanceY(g1,g1) = 2
    c: DistanceX(g-1,g4) = 65
FEATURE [Sketcher::SketchObject] Sketch039  label="Sketch"
  FullyConstrained = false
  MapMode = 5
  Placement = pos=(0,0,0) rot=(1,0,0;1.5708rad)
  Support = -> [XZ_Plane009]
  sketch-geometry (5):
    g0: LineSegment StartX=3.2 StartY=2.75 StartZ=0 EndX=5 EndY=2.75 EndZ=0
    g1: LineSegment StartX=5 StartY=2.75 StartZ=0 EndX=5 EndY=0 EndZ=0
    g2: LineSegment StartX=5 StartY=0 StartZ=0 EndX=1.5 EndY=0 EndZ=0
    g3: LineSegment StartX=1.5 StartY=0 StartZ=0 EndX=1.5 EndY=1.05 EndZ=0
    g4: LineSegment StartX=3.2 StartY=2.75 StartZ=0 EndX=1.5 EndY=1.05 EndZ=0
  constraints (15):
    c: Coincident(g0,g1)
    c: Coincident(g1,g2)
    c: Coincident(g2,g3)
    c: Horizontal(g0)
    c: Horizontal(g2)
    c: Vertical(g1)
    c: Vertical(g3)
    c: PointOnObject(g1,g-1)
    c: DistanceX(g1) = 5
    c: Coincident(g0,g4)
    c: Coincident(g4,g3)
    c: DistanceY(g0) = 2.75
    c: DistanceX(g2) = 1.5
    c: Angle(g3,g4) = 2.35619
    c: DistanceX(g0) = 3.2
FEATURE [PartDesign::Revolution] Revolution
  Angle = 360
  Axis = (-3e-16,3e-16,1)
  Base = (0,0,0)
  Placement = pos=(0,0,0) rot=(1,0,0;1.5708rad)
  Profile = -> Sketch039
  ReferenceAxis = -> Z_Axis009
  Reversed = true
FEATURE [PartDesign::Body] Body009  label="RingMagnet10x2.75_1"
  Group = -> [Sketch039,Revolution]
  Origin = -> Origin009
  Placement = pos=(-50,-3.5,25) rot=(0,0.707107,0.707107;3.14159rad)
  Tip = -> Revolution
FEATURE [Part::FeaturePython] Washer  label="M4-Washer"  # Fasteners workbench fastener (typed FeaturePython)
  Placement = pos=(50,-3,-1e-15) rot=(1,0,0;1.5708rad)
  diameter = 3
  invert = false
  matchOuter = false
  offset = 0
  type = 6
FEATURE [Part::FeaturePython] Screw004  label="M4x20-Screw001"  # Fasteners workbench fastener (typed FeaturePython)
  Placement = pos=(-50,-4,6e-15) rot=(0.57735,-0.57735,0.57735;2.0944rad)
  diameter = 6
  invert = false
  length = 7
  lengthCustom = 20
  matchOuter = false
  offset = 0
  thread = false
  type = 33
FEATURE [Part::FeaturePython] Washer001  label="M4-Washer001"  # Fasteners workbench fastener (typed FeaturePython)
  Placement = pos=(-50,-3,-1e-15) rot=(1,0,0;1.5708rad)
  diameter = 3
  invert = false
  matchOuter = false
  offset = 0
  type = 6
FEATURE [Sketcher::SketchObject] Sketch040  label="wp screw rim right crs"
  FullyConstrained = false
  MapMode = 5
  Support = -> [XY_Plane007]
  sketch-geometry (5):
    g0: LineSegment StartX=56.3 StartY=-3 StartZ=0 EndX=58.8218 EndY=-3 EndZ=0
    g1: LineSegment StartX=58.8218 StartY=-3 StartZ=0 EndX=57.75 EndY=-7 EndZ=0
    g2: LineSegment StartX=57.75 StartY=-7 StartZ=0 EndX=56.3 EndY=-7 EndZ=0
    g3: LineSegment StartX=56.3 StartY=-7 StartZ=0 EndX=56.3 EndY=-3 EndZ=0
    g4: LineSegment StartX=50 StartY=0 StartZ=0 EndX=50 EndY=-7 EndZ=0
  constraints (16):
    c: Coincident(g0,g1)
    c: Coincident(g1,g2)
    c: Coincident(g2,g3)
    c: Coincident(g3,g0)
    c: Horizontal(g0)
    c: Horizontal(g2)
    c: Vertical(g3)
    c: PointOnObject(g4,g-1)
    c: Vertical(g4)
    c: PointOnObject(g4,g2)
    c: DistanceX(g4) = 50
    c: DistanceX(g4,g2) = 6.3
    c: DistanceX(g2,g2) = 1.45
    c: DistanceY(g0,g4) = 3
    c: DistanceY(g3,g3) = 4
    c: Angle(g1,g3) = 0.261799
FEATURE [PartDesign::AdditivePipe] AdditivePipe001  label="WP Screw rim right"
  AuxilleryCurvelinear = true
  AuxillerySpineTangent = false
  BaseFeature = -> Pocket006
  Binormal = (0,0,0)
  Mode = 0
  Profile = -> Sketch040
  Spine = -> Sketch035 [Edge8,Edge5,Edge6,Edge7]
  SpineTangent = false
  Transformation = 0
  Transition = 0
FEATURE [Sketcher::SketchObject] Sketch041  label="wp screw rim left crs"
  AttachmentOffset = pos=(0,0,-50) rot=(0,0,1;0rad)
  FullyConstrained = false
  MapMode = 5
  Placement = pos=(-50,1.11e-14,-1.11e-14) rot=(0.57735,0.57735,0.57735;2.0944rad)
  Support = -> [YZ_Plane007]
  sketch-geometry (4):
    g0: LineSegment StartX=-3 StartY=6.3 StartZ=0 EndX=-7 EndY=6.3 EndZ=0
    g1: LineSegment StartX=-7 StartY=6.3 StartZ=0 EndX=-7 EndY=7.75 EndZ=0
    g2: LineSegment StartX=-7 StartY=7.75 StartZ=0 EndX=-3 EndY=8.8218 EndZ=0
    g3: LineSegment StartX=-3 StartY=8.8218 StartZ=0 EndX=-3 EndY=6.3 EndZ=0
  constraints (12):
    c: Coincident(g0,g1)
    c: Coincident(g1,g2)
    c: Coincident(g2,g3)
    c: Coincident(g3,g0)
    c: Horizontal(g0)
    c: Vertical(g1)
    c: Vertical(g3)
    c: DistanceX(g0,g-1) = 3
    c: DistanceY(g-1,g0) = 6.3
    c: DistanceX(g0,g0) = 4
    c: DistanceY(g1,g1) = 1.45
    c: Angle(g0,g2) = 0.261799
FEATURE [PartDesign::AdditivePipe] AdditivePipe002  label="WP Screw rim left"
  AuxilleryCurvelinear = true
  AuxillerySpineTangent = false
  BaseFeature = -> AdditivePipe001
  Binormal = (0,0,0)
  Mode = 0
  Profile = -> Sketch041
  Spine = -> Sketch035 [Edge4,Edge1,Edge2,Edge3]
  SpineTangent = false
  Transformation = 0
  Transition = 0
FEATURE [PartDesign::AdditivePipe] AdditivePipe  label="WP Seal rib"
  AuxilleryCurvelinear = true
  AuxillerySpineTangent = false
  BaseFeature = -> AdditivePipe002
  Binormal = (0,0,0)
  Mode = 0
  Profile = -> Sketch036
  Spine = -> Sketch022
  SpineTangent = false
  Transformation = 0
  Transition = 0
FEATURE [Sketcher::SketchObject] Sketch042
  FullyConstrained = false
  MapMode = 5
  Placement = pos=(0,0,0) rot=(1,0,0;1.5708rad)
  Support = -> [XZ_Plane010]
  sketch-geometry (5):
    g0: LineSegment StartX=3.2 StartY=2.75 StartZ=0 EndX=5 EndY=2.75 EndZ=0
    g1: LineSegment StartX=5 StartY=2.75 StartZ=0 EndX=5 EndY=0 EndZ=0
    g2: LineSegment StartX=5 StartY=0 StartZ=0 EndX=1.5 EndY=0 EndZ=0
    g3: LineSegment StartX=1.5 StartY=0 StartZ=0 EndX=1.5 EndY=1.05 EndZ=0
    g4: LineSegment StartX=3.2 StartY=2.75 StartZ=0 EndX=1.5 EndY=1.05 EndZ=0
  constraints (15):
    c: Coincident(g0,g1)
    c: Coincident(g1,g2)
    c: Coincident(g2,g3)
    c: Horizontal(g0)
    c: Horizontal(g2)
    c: Vertical(g1)
    c: Vertical(g3)
    c: PointOnObject(g1,g-1)
    c: DistanceX(g1) = 5
    c: Coincident(g0,g4)
    c: Coincident(g4,g3)
    c: DistanceY(g0) = 2.75
    c: DistanceX(g2) = 1.5
    c: Angle(g3,g4) = 2.35619
    c: DistanceX(g0) = 3.2
FEATURE [PartDesign::Revolution] Revolution001
  Angle = 360
  Axis = (-3e-16,3e-16,1)
  Base = (0,0,0)
  Placement = pos=(0,0,0) rot=(1,0,0;1.5708rad)
  Profile = -> Sketch042
  ReferenceAxis = -> Z_Axis007
  Reversed = true
FEATURE [PartDesign::Body] Body010  label="RingMagnet10x2.75_2"
  Group = -> [Sketch042,Revolution001]
  Origin = -> Origin010
  Placement = pos=(-50,-4,25) rot=(1,0,0;1.5708rad)
  Tip = -> Revolution001
FEATURE [Sketcher::SketchObject] Sketch045  label="hb cut around crs"
  FullyConstrained = false
  MapMode = 5
  Support = -> [XY_Plane013]
  sketch-geometry (5):
    g0: LineSegment StartX=70 StartY=0 StartZ=0 EndX=90 EndY=0 EndZ=0
    g1: LineSegment StartX=90 StartY=0 StartZ=0 EndX=90 EndY=-25 EndZ=0
    g2: LineSegment StartX=90 StartY=-25 StartZ=0 EndX=62 EndY=-25 EndZ=0
    g3: LineSegment StartX=70 StartY=-6 StartZ=0 EndX=70 EndY=0 EndZ=0
    g4: ArcOfCircle CenterX=43.4375 CenterY=-6 CenterZ=0 NormalX=0 NormalY=0 NormalZ=1 AngleXU=0 Radius=26.5625 StartAngle=5.48614 EndAngle=6.28319
  constraints (15):
    c: Coincident(g0,g1)
    c: Coincident(g1,g2)
    c: Coincident(g3,g0)
    c: Horizontal(g0)
    c: Horizontal(g2)
    c: Vertical(g1)
    c: Vertical(g3)
    c: PointOnObject(g0,g-1)
    c: Coincident(g2,g4)
    c: Tangent(g4,g3) = -1.5708
    c: DistanceX(g0) = 70
    c: DistanceY(g3,g3) = 6
    c: DistanceY(g1,g1) = 25
    c: DistanceX(g2,g3) = 8
    c: DistanceX(g0,g0) = 20
FEATURE [Sketcher::SketchObject] Sketch047  label="hb cut around trj"
  FullyConstrained = false
  MapMode = 5
  Placement = pos=(0,0,0) rot=(1,0,0;1.5708rad)
  sketch-geometry (13):
    g0: LineSegment StartX=70 StartY=26.7141 StartZ=0 EndX=70 EndY=-26.7141 EndZ=0
    g1: LineSegment StartX=-70 StartY=-26.7141 StartZ=0 EndX=-70 EndY=26.7141 EndZ=0
    g2: ArcOfCircle CenterX=62 CenterY=26.7141 CenterZ=0 NormalX=0 NormalY=0 NormalZ=1 AngleXU=0 Radius=8 StartAngle=0 EndAngle=1.24199
    g3: ArcOfCircle CenterX=-62 CenterY=26.7141 CenterZ=0 NormalX=0 NormalY=0 NormalZ=1 AngleXU=0 Radius=8 StartAngle=1.89961 EndAngle=3.14159
    g4: ArcOfCircle CenterX=-62 CenterY=-26.7141 CenterZ=0 NormalX=0 NormalY=0 NormalZ=1 AngleXU=0 Radius=8 StartAngle=3.14159 EndAngle=4.38358
    g5: ArcOfCircle CenterX=62 CenterY=-26.7141 CenterZ=0 NormalX=0 NormalY=0 NormalZ=1 AngleXU=0 Radius=8 StartAngle=5.0412 EndAngle=6.28319
    g6: LineSegment StartX=62 StartY=26.7141 StartZ=0 EndX=-62 EndY=26.7141 EndZ=0
    g7: LineSegment StartX=-62 StartY=26.7141 StartZ=0 EndX=-62 EndY=-26.7141 EndZ=0
    g8: LineSegment StartX=-62 StartY=-26.7141 StartZ=0 EndX=62 EndY=-26.7141 EndZ=0
    g9: LineSegment StartX=62 StartY=-26.7141 StartZ=0 EndX=62 EndY=26.7141 EndZ=0
    g10: ArcOfCircle CenterX=2.7e-14 CenterY=-155 CenterZ=0 NormalX=0 NormalY=0 NormalZ=1 AngleXU=0 Radius=200 StartAngle=1.24199 EndAngle=1.89961
    g11: ArcOfCircle CenterX=1.98e-14 CenterY=155 CenterZ=0 NormalX=0 NormalY=0 NormalZ=1 AngleXU=0 Radius=200 StartAngle=4.38358 EndAngle=5.0412
    g12: LineSegment StartX=0 StartY=45 StartZ=0 EndX=0 EndY=-45 EndZ=0
  constraints (32):
    c: Vertical(g0)
    c: Vertical(g1)
    c: Tangent(g0,g2) = 1.5708
    c: Tangent(g1,g3) = 1.5708
    c: Tangent(g1,g4) = 1.5708
    c: Tangent(g0,g5) = 1.5708
    c: Coincident(g6,g7)
    c: Coincident(g7,g8)
    c: Coincident(g8,g9)
    c: Coincident(g9,g6)
    c: Horizontal(g8)
    c: Coincident(g6,g2)
    c: Coincident(g7,g4)
    c: Coincident(g3,g6)
    c: Coincident(g5,g8)
    c: Symmetric(g5,g2,g-1)
    c: Symmetric(g2,g3,g-2)
    c: DistanceX(g1,g0) = 140
    c: Radius(g2) = 8
    c: Tangent(g3,g10) = -1.5708
    c: Tangent(g2,g10) = -1.5708
    c: Tangent(g5,g11) = -1.5708
    c: Tangent(g4,g11) = -1.5708
    c: Equal(g11,g10)
    c: Radius(g10) = 200
    c: Vertical(g7)
    c: Equal(g2,g3)
    c: PointOnObject(g12,g10)
    c: PointOnObject(g12,g11)
    c: Vertical(g12)
    c: PointOnObject(g-1,g12)
    c: DistanceY(g12,g12) = 90
FEATURE [Sketcher::SketchObject] Sketch048  label="hb base"
  FullyConstrained = false
  MapMode = 5
  Support = -> [XY_Plane013]
  sketch-geometry (6):
    g0: LineSegment StartX=-71 StartY=0 StartZ=0 EndX=71 EndY=0 EndZ=0
    g1: LineSegment StartX=71 StartY=0 StartZ=0 EndX=71 EndY=-12 EndZ=0
    g2: LineSegment StartX=32.5 StartY=-22 StartZ=0 EndX=-32.5 EndY=-22 EndZ=0
    g3: LineSegment StartX=-71 StartY=-12 StartZ=0 EndX=-71 EndY=0 EndZ=0
    g4: ArcOfCircle CenterX=-32.5 CenterY=57.1125 CenterZ=0 NormalX=0 NormalY=0 NormalZ=1 AngleXU=0 Radius=79.1125 StartAngle=4.20414 EndAngle=4.71239
    g5: ArcOfCircle CenterX=32.5 CenterY=57.1125 CenterZ=0 NormalX=0 NormalY=0 NormalZ=1 AngleXU=0 Radius=79.1125 StartAngle=4.71239 EndAngle=5.22064
  constraints (16):
    c: Coincident(g0,g1)
    c: Coincident(g3,g0)
    c: Horizontal(g2)
    c: Vertical(g1)
    c: Vertical(g3)
    c: Tangent(g2,g4) = 1.5708
    c: Tangent(g2,g5) = 1.5708
    c: Symmetric(g5,g4,g-2)
    c: DistanceX(g4,g5) = 65
    c: Symmetric(g0,g0,g-2)
    c: DistanceX(g0,g0) = 142
    c: Coincident(g3,g4)
    c: Coincident(g1,g5)
    c: DistanceY(g2,g3) = 10
    c: DistanceY(g2,g0) = 22
    c: PointOnObject(g0,g-1)
FEATURE [PartDesign::Pad] Pad011  label="HB Base"
  Direction = (1,1,1)
  Length = 92
  Length2 = 100
  Midplane = true
  Profile = -> Sketch048
  Type = 0
FEATURE [PartDesign::SubtractivePipe] SubtractivePipe003  label="HB Cut around"
  AuxilleryCurvelinear = true
  AuxillerySpineTangent = false
  BaseFeature = -> Pad011
  Binormal = (0,0,0)
  Mode = 0
  Profile = -> Sketch045
  Spine = -> Sketch047
  SpineTangent = false
  Transformation = 0
  Transition = 0
FEATURE [Sketcher::SketchObject] Sketch050  label="hb seal groove wall plate crs"
  FullyConstrained = false
  MapMode = 5
  Support = -> [XY_Plane013]
  sketch-geometry (6):
    g0: LineSegment StartX=63.0203 StartY=-3 StartZ=0 EndX=66.9797 EndY=-3 EndZ=0
    g1: LineSegment StartX=66.9797 StartY=-3 StartZ=0 EndX=65.433 EndY=-5.67894 EndZ=0
    g2: LineSegment StartX=64.567 StartY=-5.67894 StartZ=0 EndX=63.0203 EndY=-3 EndZ=0
    g3: LineSegment StartX=65 StartY=-5.42894 StartZ=0 EndX=65 EndY=-3 EndZ=0
    g4: LineSegment StartX=64.175 StartY=-5 StartZ=0 EndX=65.825 EndY=-5 EndZ=0
    g5: ArcOfCircle CenterX=65 CenterY=-5.42894 CenterZ=0 NormalX=0 NormalY=0 NormalZ=1 AngleXU=0 Radius=0.5 StartAngle=3.66519 EndAngle=5.75959
  constraints (17):
    c: Coincident(g0,g1)
    c: Coincident(g2,g0)
    c: Horizontal(g0)
    c: DistanceY(g0,g-1) = 3
    c: PointOnObject(g3,g0)
    c: Symmetric(g0,g0,g3)
    c: Angle(g1,g2) = 1.0472
    c: DistanceX(g-1,g3) = 65
    c: PointOnObject(g4,g2)
    c: PointOnObject(g4,g1)
    c: Horizontal(g4)
    c: DistanceY(g4,g0) = 2
    c: DistanceX(g4,g4) = 1.65
    c: Tangent(g1,g5) = 1.5708
    c: Tangent(g2,g5) = 1.5708
    c: Coincident(g3,g5)
    c: Radius(g5) = 0.5
FEATURE [Sketcher::SketchObject] Sketch053  label="hb separation bottom"
  FullyConstrained = false
  MapMode = 5
  Placement = pos=(0,0,0) rot=(0.57735,0.57735,0.57735;2.0944rad)
  Support = -> [YZ_Plane013]
  sketch-geometry (4):
    g0: LineSegment StartX=-3.5 StartY=46 StartZ=0 EndX=0 EndY=46 EndZ=0
    g1: LineSegment StartX=0 StartY=46 StartZ=0 EndX=0 EndY=-46 EndZ=0
    g2: LineSegment StartX=0 StartY=-46 StartZ=0 EndX=-3.5 EndY=-46 EndZ=0
    g3: LineSegment StartX=-3.5 StartY=-46 StartZ=0 EndX=-3.5 EndY=46 EndZ=0
  constraints (11):
    c: Coincident(g0,g1)
    c: Coincident(g1,g2)
    c: Coincident(g2,g3)
    c: Coincident(g3,g0)
    c: Horizontal(g0)
    c: Horizontal(g2)
    c: Vertical(g1)
    c: PointOnObject(g1,g-2)
    c: Symmetric(g2,g0,g-1)
    c: DistanceY(g3,g3) = 92
    c: DistanceX(g0,g0) = 3.5
FEATURE [Sketcher::SketchObject] Sketch055  label="hb wall screw holes"
  AttachmentOffset = pos=(0,0,9.5) rot=(0,0,1;0rad)
  FullyConstrained = false
  MapMode = 5
  Placement = pos=(0,-9.5,-2.1e-15) rot=(1,0,0;1.5708rad)
  Support = -> [XZ_Plane013]
  sketch-geometry (9):
    g0: ArcOfCircle CenterX=50 CenterY=4 CenterZ=0 NormalX=0 NormalY=0 NormalZ=1 AngleXU=0 Radius=9.5 StartAngle=2.364e-13 EndAngle=3.14159
    g1: ArcOfCircle CenterX=50 CenterY=-4 CenterZ=0 NormalX=0 NormalY=0 NormalZ=1 AngleXU=0 Radius=9.5 StartAngle=3.14159 EndAngle=6.28319
    g2: LineSegment StartX=40.5 StartY=4 StartZ=0 EndX=40.5 EndY=-4 EndZ=0
    g3: LineSegment StartX=59.5 StartY=4 StartZ=0 EndX=59.5 EndY=-4 EndZ=0
    g4: ArcOfCircle CenterX=-54 CenterY=0 CenterZ=0 NormalX=0 NormalY=0 NormalZ=1 AngleXU=0 Radius=9.5 StartAngle=1.5708 EndAngle=4.71239
    g5: ArcOfCircle CenterX=-46 CenterY=-2e-16 CenterZ=0 NormalX=0 NormalY=0 NormalZ=1 AngleXU=0 Radius=9.5 StartAngle=4.71239 EndAngle=7.85398
    g6: LineSegment StartX=-54 StartY=-9.5 StartZ=0 EndX=-46 EndY=-9.5 EndZ=0
    g7: LineSegment StartX=-54 StartY=9.5 StartZ=0 EndX=-46 EndY=9.5 EndZ=0
    g8: LineSegment StartX=-50 StartY=9.5 StartZ=0 EndX=-50 EndY=-9.5 EndZ=0
  constraints (22):
    c: Tangent(g0,g3)
    c: Tangent(g0,g2)
    c: Tangent(g2,g1)
    c: Tangent(g3,g1)
    c: Vertical(g2)
    c: Symmetric(g0,g1,g-1)
    c: DistanceX(g0) = 50
    c: DistanceY(g1,g0) = 8
    c: Radius(g1) = 9.5
    c: Tangent(g4,g7)
    c: Tangent(g4,g6)
    c: Tangent(g6,g5)
    c: Tangent(g7,g5)
    c: Horizontal(g6)
    c: Equal(g4,g5)
    c: PointOnObject(g4,g-1)
    c: PointOnObject(g8,g7)
    c: PointOnObject(g8,g6)
    c: Symmetric(g5,g4,g8)
    c: DistanceX(g8,g-1) = 50
    c: Equal(g7,g3)
    c: Equal(g5,g1)
FEATURE [Sketcher::SketchObject] Sketch059  label="ht base"
  FullyConstrained = false
  MapMode = 5
  Support = -> [XY_Plane014]
  sketch-geometry (6):
    g0: LineSegment StartX=-71 StartY=0 StartZ=0 EndX=71 EndY=0 EndZ=0
    g1: LineSegment StartX=71 StartY=0 StartZ=0 EndX=71 EndY=-12 EndZ=0
    g2: LineSegment StartX=32.5 StartY=-22 StartZ=0 EndX=-32.5 EndY=-22 EndZ=0
    g3: LineSegment StartX=-71 StartY=-12 StartZ=0 EndX=-71 EndY=0 EndZ=0
    g4: ArcOfCircle CenterX=-32.5 CenterY=57.1125 CenterZ=0 NormalX=0 NormalY=0 NormalZ=1 AngleXU=0 Radius=79.1125 StartAngle=4.20414 EndAngle=4.71239
    g5: ArcOfCircle CenterX=32.5 CenterY=57.1125 CenterZ=0 NormalX=0 NormalY=0 NormalZ=1 AngleXU=0 Radius=79.1125 StartAngle=4.71239 EndAngle=5.22064
  constraints (16):
    c: Coincident(g0,g1)
    c: Coincident(g3,g0)
    c: Horizontal(g2)
    c: Vertical(g1)
    c: Vertical(g3)
    c: Tangent(g2,g4) = 1.5708
    c: Tangent(g2,g5) = 1.5708
    c: Symmetric(g5,g4,g-2)
    c: DistanceX(g4,g5) = 65
    c: Symmetric(g0,g0,g-2)
    c: DistanceX(g0,g0) = 142
    c: Coincident(g3,g4)
    c: Coincident(g1,g5)
    c: DistanceY(g2,g3) = 10
    c: DistanceY(g2,g0) = 22
    c: PointOnObject(g0,g-1)
FEATURE [PartDesign::Pad] Pad012  label="HT Base"
  Direction = (1,1,1)
  Length = 92
  Length2 = 100
  Midplane = true
  Profile = -> Sketch059
  Type = 0
FEATURE [Sketcher::SketchObject] Sketch060  label="ht cut around crs"
  FullyConstrained = false
  MapMode = 5
  Support = -> [XY_Plane014]
  sketch-geometry (5):
    g0: LineSegment StartX=70 StartY=0 StartZ=0 EndX=90 EndY=0 EndZ=0
    g1: LineSegment StartX=90 StartY=0 StartZ=0 EndX=90 EndY=-25 EndZ=0
    g2: LineSegment StartX=90 StartY=-25 StartZ=0 EndX=62 EndY=-25 EndZ=0
    g3: LineSegment StartX=70 StartY=-6 StartZ=0 EndX=70 EndY=0 EndZ=0
    g4: ArcOfCircle CenterX=43.4375 CenterY=-6 CenterZ=0 NormalX=0 NormalY=0 NormalZ=1 AngleXU=0 Radius=26.5625 StartAngle=5.48614 EndAngle=6.28319
  constraints (15):
    c: Coincident(g0,g1)
    c: Coincident(g1,g2)
    c: Coincident(g3,g0)
    c: Horizontal(g0)
    c: Horizontal(g2)
    c: Vertical(g1)
    c: Vertical(g3)
    c: PointOnObject(g0,g-1)
    c: Coincident(g2,g4)
    c: Tangent(g4,g3) = -1.5708
    c: DistanceX(g0) = 70
    c: DistanceY(g3,g3) = 6
    c: DistanceY(g1,g1) = 25
    c: DistanceX(g2,g3) = 8
    c: DistanceX(g0,g0) = 20
FEATURE [Sketcher::SketchObject] Sketch061  label="ht cut around trj"
  FullyConstrained = true
  MapMode = 5
  Placement = pos=(0,0,0) rot=(1,0,0;1.5708rad)
  sketch-geometry (13):
    g0: LineSegment StartX=70 StartY=26.7141 StartZ=0 EndX=70 EndY=-26.7141 EndZ=0
    g1: LineSegment StartX=-70 StartY=-26.7141 StartZ=0 EndX=-70 EndY=26.7141 EndZ=0
    g2: ArcOfCircle CenterX=62 CenterY=26.7141 CenterZ=0 NormalX=0 NormalY=0 NormalZ=1 AngleXU=0 Radius=8 StartAngle=0 EndAngle=1.24199
    g3: ArcOfCircle CenterX=-62 CenterY=26.7141 CenterZ=0 NormalX=0 NormalY=0 NormalZ=1 AngleXU=0 Radius=8 StartAngle=1.89961 EndAngle=3.14159
    g4: ArcOfCircle CenterX=-62 CenterY=-26.7141 CenterZ=0 NormalX=0 NormalY=0 NormalZ=1 AngleXU=0 Radius=8 StartAngle=3.14159 EndAngle=4.38358
    g5: ArcOfCircle CenterX=62 CenterY=-26.7141 CenterZ=0 NormalX=0 NormalY=0 NormalZ=1 AngleXU=0 Radius=8 StartAngle=5.0412 EndAngle=6.28319
    g6: LineSegment StartX=62 StartY=26.7141 StartZ=0 EndX=-62 EndY=26.7141 EndZ=0
    g7: LineSegment StartX=-62 StartY=26.7141 StartZ=0 EndX=-62 EndY=-26.7141 EndZ=0
    g8: LineSegment StartX=-62 StartY=-26.7141 StartZ=0 EndX=62 EndY=-26.7141 EndZ=0
    g9: LineSegment StartX=62 StartY=-26.7141 StartZ=0 EndX=62 EndY=26.7141 EndZ=0
    g10: ArcOfCircle CenterX=-5.726e-13 CenterY=-155 CenterZ=0 NormalX=0 NormalY=0 NormalZ=1 AngleXU=0 Radius=200 StartAngle=1.24199 EndAngle=1.89961
    g11: ArcOfCircle CenterX=-6.477e-13 CenterY=155 CenterZ=0 NormalX=0 NormalY=0 NormalZ=1 AngleXU=0 Radius=200 StartAngle=4.38358 EndAngle=5.0412
    g12: LineSegment StartX=0 StartY=45 StartZ=0 EndX=0 EndY=-45 EndZ=0
  constraints (32):
    c: Vertical(g0)
    c: Vertical(g1)
    c: Tangent(g0,g2) = 1.5708
    c: Tangent(g1,g3) = 1.5708
    c: Tangent(g1,g4) = 1.5708
    c: Tangent(g0,g5) = 1.5708
    c: Coincident(g6,g7)
    c: Coincident(g7,g8)
    c: Coincident(g8,g9)
    c: Coincident(g9,g6)
    c: Horizontal(g8)
    c: Coincident(g6,g2)
    c: Coincident(g7,g4)
    c: Coincident(g3,g6)
    c: Coincident(g5,g8)
    c: Symmetric(g5,g2,g-1)
    c: Symmetric(g2,g3,g-2)
    c: DistanceX(g1,g0) = 140
    c: Radius(g2) = 8
    c: Tangent(g2,g10) = -1.5708
    c: Tangent(g3,g10) = -1.5708
    c: Vertical(g7)
    c: Tangent(g4,g11) = -1.5708
    c: Tangent(g5,g11) = -1.5708
    c: Equal(g11,g10)
    c: Radius(g10) = 200
    c: PointOnObject(g12,g10)
    c: PointOnObject(g12,g11)
    c: Vertical(g12)
    c: PointOnObject(g-1,g12)
    c: DistanceY(g12,g12) = 90
    c: Equal(g4,g2)
FEATURE [PartDesign::SubtractivePipe] SubtractivePipe006  label="HT Cut around"
  AuxilleryCurvelinear = true
  AuxillerySpineTangent = false
  BaseFeature = -> Pad012
  Binormal = (0,0,0)
  Mode = 0
  Profile = -> Sketch060
  Spine = -> Sketch061
  SpineTangent = false
  Transformation = 0
  Transition = 0
FEATURE [Sketcher::SketchObject] Sketch062  label="ht separation top"
  FullyConstrained = false
  MapMode = 5
  Placement = pos=(0,0,0) rot=(0.57735,0.57735,0.57735;2.0944rad)
  Support = -> [YZ_Plane014]
  sketch-geometry (4):
    g0: LineSegment StartX=-9.5 StartY=46 StartZ=0 EndX=0 EndY=46 EndZ=0
    g1: LineSegment StartX=0 StartY=46 StartZ=0 EndX=0 EndY=-46 EndZ=0
    g2: LineSegment StartX=0 StartY=-46 StartZ=0 EndX=-9.5 EndY=-46 EndZ=0
    g3: LineSegment StartX=-9.5 StartY=-46 StartZ=0 EndX=-9.5 EndY=46 EndZ=0
  constraints (11):
    c: Coincident(g0,g1)
    c: Coincident(g1,g2)
    c: Coincident(g2,g3)
    c: Coincident(g3,g0)
    c: Horizontal(g0)
    c: Horizontal(g2)
    c: Vertical(g3)
    c: PointOnObject(g1,g-2)
    c: DistanceX(g0,g0) = 9.5
    c: Symmetric(g0,g1,g-1)
    c: DistanceY(g3,g3) = 92
FEATURE [Sketcher::SketchObject] Sketch064  label="hb seal rim top crs"
  FullyConstrained = false
  MapMode = 5
  Support = -> [XY_Plane013]
  sketch-geometry (5):
    g0: LineSegment StartX=63.4216 StartY=-9 StartZ=0 EndX=66.5784 EndY=-9 EndZ=0
    g1: LineSegment StartX=66.5784 StartY=-9 StartZ=0 EndX=65.75 EndY=-11 EndZ=0
    g2: LineSegment StartX=65.75 StartY=-11 StartZ=0 EndX=64.25 EndY=-11 EndZ=0
    g3: LineSegment StartX=64.25 StartY=-11 StartZ=0 EndX=63.4216 EndY=-9 EndZ=0
    g4: LineSegment StartX=65 StartY=-11 StartZ=0 EndX=65 EndY=-9 EndZ=0
  constraints (14):
    c: Coincident(g0,g1)
    c: Coincident(g1,g2)
    c: Coincident(g2,g3)
    c: Coincident(g3,g0)
    c: Horizontal(g0)
    c: DistanceY(g0,g-1) = 9
    c: PointOnObject(g4,g2)
    c: PointOnObject(g4,g0)
    c: Symmetric(g0,g0,g4)
    c: Symmetric(g1,g2,g4)
    c: DistanceX(g2,g2) = 1.5
    c: Angle(g1,g3) = 0.785398
    c: DistanceY(g1,g1) = 2
    c: DistanceX(g-1,g4) = 65
FEATURE [Sketcher::SketchObject] Sketch065  label="ht seal groove bottom crs"
  FullyConstrained = false
  MapMode = 5
  Support = -> [XY_Plane014]
  sketch-geometry (6):
    g0: LineSegment StartX=63.0203 StartY=-9 StartZ=0 EndX=66.9797 EndY=-9 EndZ=0
    g1: LineSegment StartX=66.9797 StartY=-9 StartZ=0 EndX=65.433 EndY=-11.6789 EndZ=0
    g2: LineSegment StartX=64.567 StartY=-11.6789 StartZ=0 EndX=63.0203 EndY=-9 EndZ=0
    g3: LineSegment StartX=65 StartY=-11.4289 StartZ=0 EndX=65 EndY=-9 EndZ=0
    g4: LineSegment StartX=64.175 StartY=-11 StartZ=0 EndX=65.825 EndY=-11 EndZ=0
    g5: ArcOfCircle CenterX=65 CenterY=-11.4289 CenterZ=0 NormalX=0 NormalY=0 NormalZ=1 AngleXU=0 Radius=0.5 StartAngle=3.66519 EndAngle=5.75959
  constraints (17):
    c: Coincident(g0,g1)
    c: Coincident(g2,g0)
    c: Horizontal(g0)
    c: DistanceY(g0,g-1) = 9
    c: PointOnObject(g3,g0)
    c: Symmetric(g0,g0,g3)
    c: Angle(g1,g2) = 1.0472
    c: DistanceX(g-1,g3) = 65
    c: PointOnObject(g4,g2)
    c: PointOnObject(g4,g1)
    c: Horizontal(g4)
    c: DistanceY(g4,g0) = 2
    c: DistanceX(g4,g4) = 1.65
    c: Tangent(g1,g5) = 1.5708
    c: Tangent(g2,g5) = 1.5708
    c: Coincident(g3,g5)
    c: Radius(g5) = 0.5
FEATURE [Sketcher::SketchObject] Sketch066  label="hb cavity for wires"
  FullyConstrained = false
  MapMode = 5
  Placement = pos=(0,0,0) rot=(1,0,0;1.5708rad)
  Support = -> [XZ_Plane013]
  sketch-geometry (21):
    g0: LineSegment StartX=-24 StartY=30 StartZ=0 EndX=24 EndY=30 EndZ=0
    g1: LineSegment StartX=24 StartY=30 StartZ=0 EndX=24 EndY=6 EndZ=0
    g2: LineSegment StartX=24 StartY=6 StartZ=0 EndX=-24 EndY=6 EndZ=0
    g3: LineSegment StartX=-24 StartY=6 StartZ=0 EndX=-24 EndY=30 EndZ=0
    g4: LineSegment StartX=-24 StartY=36 StartZ=0 EndX=24 EndY=36 EndZ=0
    g5: LineSegment StartX=30 StartY=30 StartZ=0 EndX=30 EndY=6 EndZ=0
    g6: LineSegment StartX=24 StartY=0 StartZ=0 EndX=-9 EndY=0 EndZ=0
    g7: LineSegment StartX=-30 StartY=6 StartZ=0 EndX=-30 EndY=30 EndZ=0
    g8: ArcOfCircle CenterX=-24 CenterY=30 CenterZ=0 NormalX=0 NormalY=0 NormalZ=1 AngleXU=0 Radius=6 StartAngle=1.5708 EndAngle=3.14159
    g9: ArcOfCircle CenterX=-24 CenterY=6 CenterZ=0 NormalX=0 NormalY=0 NormalZ=1 AngleXU=0 Radius=6 StartAngle=3.14159 EndAngle=4.71239
    g10: ArcOfCircle CenterX=24 CenterY=6 CenterZ=0 NormalX=0 NormalY=0 NormalZ=1 AngleXU=0 Radius=6 StartAngle=4.71239 EndAngle=6.28319
    g11: ArcOfCircle CenterX=24 CenterY=30 CenterZ=0 NormalX=0 NormalY=0 NormalZ=1 AngleXU=0 Radius=6 StartAngle=0 EndAngle=1.5708
    g12: LineSegment StartX=-9.5 StartY=-0.5 StartZ=0 EndX=-9.5 EndY=-10 EndZ=0
    g13: LineSegment StartX=-10 StartY=-10.5 StartZ=0 EndX=-20 EndY=-10.5 EndZ=0
    g14: LineSegment StartX=-20.5 StartY=-10 StartZ=0 EndX=-20.5 EndY=-0.5 EndZ=0
    g15: ArcOfCircle CenterX=-20 CenterY=-10 CenterZ=0 NormalX=0 NormalY=0 NormalZ=1 AngleXU=0 Radius=0.5 StartAngle=3.14159 EndAngle=4.71239
    g16: ArcOfCircle CenterX=-10 CenterY=-10 CenterZ=0 NormalX=0 NormalY=0 NormalZ=1 AngleXU=0 Radius=0.5 StartAngle=4.71239 EndAngle=6.28319
    g17: LineSegment StartX=-15 StartY=-10.5 StartZ=0 EndX=-15 EndY=6 EndZ=0
    g18: LineSegment StartX=-21 StartY=0 StartZ=0 EndX=-24 EndY=0 EndZ=0
    g19: ArcOfCircle CenterX=-21 CenterY=-0.5 CenterZ=0 NormalX=0 NormalY=0 NormalZ=1 AngleXU=0 Radius=0.5 StartAngle=0 EndAngle=1.5708
    g20: ArcOfCircle CenterX=-9 CenterY=-0.5 CenterZ=0 NormalX=0 NormalY=0 NormalZ=1 AngleXU=0 Radius=0.5 StartAngle=1.5708 EndAngle=3.14159
  constraints (49):
    c: Coincident(g0,g1)
    c: Coincident(g1,g2)
    c: Coincident(g2,g3)
    c: Coincident(g3,g0)
    c: Horizontal(g2)
    c: Vertical(g1)
    c: Vertical(g3)
    c: Symmetric(g0,g0,g-2)
    c: Horizontal(g4)
    c: Horizontal(g6)
    c: Vertical(g5)
    c: Tangent(g4,g8) = 1.5708
    c: Tangent(g7,g8) = 1.5708
    c: Tangent(g7,g9) = 1.5708
    c: Tangent(g6,g10) = 1.5708
    c: Tangent(g5,g10) = 1.5708
    c: Tangent(g5,g11) = 1.5708
    c: Tangent(g4,g11) = 1.5708
    c: Coincident(g0,g11)
    c: Coincident(g1,g10)
    c: Coincident(g2,g9)
    c: Coincident(g0,g8)
    c: PointOnObject(g6,g-1)
    c: DistanceY(g4) = 36
    c: DistanceX(g7,g5) = 60
    c: Radius(g11) = 6
    c: Horizontal(g13)
    c: Vertical(g12)
    c: Vertical(g14)
    c: Tangent(g13,g15) = 1.5708
    c: Tangent(g14,g15) = 1.5708
    c: Tangent(g12,g16) = 1.5708
    c: Tangent(g13,g16) = 1.5708
    c: PointOnObject(g17,g13)
    c: PointOnObject(g17,g2)
    c: Vertical(g17)
    c: Symmetric(g16,g15,g17)
    c: Radius(g16) = 0.5
    c: DistanceX(g17,g-1) = 15
    c: Tangent(g6,g18)
    c: Tangent(g18,g19) = -1.5708
    c: Tangent(g14,g19) = -1.5708
    c: Tangent(g12,g20) = -1.5708
    c: Tangent(g6,g20) = -1.5708
    c: Equal(g20,g19)
    c: Equal(g19,g15)
    c: DistanceX(g14,g12) = 11
    c: DistanceY(g13,g-1) = 10.5
    c: Tangent(g9,g18) = 1.5708
FEATURE [Sketcher::SketchObject] Sketch067  label="hb cavity esp"
  AttachmentOffset = pos=(0,0,5) rot=(0,0,1;0rad)
  FullyConstrained = false
  MapMode = 5
  Placement = pos=(0,-5,-1.1e-15) rot=(1,0,0;1.5708rad)
  Support = -> [XZ_Plane013]
  sketch-geometry (16):
    g0: LineSegment StartX=1 StartY=-1.75 StartZ=0 EndX=32 EndY=-1.75 EndZ=0
    g1: LineSegment StartX=32 StartY=-1.75 StartZ=0 EndX=32 EndY=-40.75 EndZ=0
    g2: LineSegment StartX=32 StartY=-40.75 StartZ=0 EndX=1 EndY=-40.75 EndZ=0
    g3: LineSegment StartX=1 StartY=-40.75 StartZ=0 EndX=1 EndY=-1.75 EndZ=0
    g4: LineSegment StartX=32 StartY=-1.5 StartZ=0 EndX=1 EndY=-1.5 EndZ=0
    g5: LineSegment StartX=0.75 StartY=-1.75 StartZ=0 EndX=0.75 EndY=-3.5 EndZ=0
    g6: LineSegment StartX=1 StartY=-41 StartZ=0 EndX=32 EndY=-41 EndZ=0
    g7: LineSegment StartX=32.25 StartY=-40.75 StartZ=0 EndX=32.25 EndY=-1.75 EndZ=0
    g8: ArcOfCircle CenterX=1 CenterY=-40.75 CenterZ=0 NormalX=0 NormalY=0 NormalZ=1 AngleXU=0 Radius=0.25 StartAngle=3.14159 EndAngle=4.71239
    g9: ArcOfCircle CenterX=32 CenterY=-40.75 CenterZ=0 NormalX=0 NormalY=0 NormalZ=1 AngleXU=0 Radius=0.25 StartAngle=4.71239 EndAngle=6.28319
    g10: ArcOfCircle CenterX=32 CenterY=-1.75 CenterZ=0 NormalX=0 NormalY=0 NormalZ=1 AngleXU=0 Radius=0.25 StartAngle=0 EndAngle=1.5708
    g11: ArcOfCircle CenterX=1 CenterY=-1.75 CenterZ=0 NormalX=0 NormalY=0 NormalZ=1 AngleXU=0 Radius=0.25 StartAngle=1.5708 EndAngle=3.14159
    g12: LineSegment StartX=-2 StartY=-3.5 StartZ=0 EndX=0.75 EndY=-3.5 EndZ=0
    g13: LineSegment StartX=0.75 StartY=-35 StartZ=0 EndX=-2 EndY=-35 EndZ=0
    g14: LineSegment StartX=-2 StartY=-35 StartZ=0 EndX=-2 EndY=-3.5 EndZ=0
    g15: LineSegment StartX=0.75 StartY=-35 StartZ=0 EndX=0.75 EndY=-40.75 EndZ=0
  constraints (39):
    c: Coincident(g0,g1)
    c: Coincident(g1,g2)
    c: Coincident(g2,g3)
    c: Coincident(g3,g0)
    c: Horizontal(g0)
    c: Horizontal(g2)
    c: Vertical(g1)
    c: Vertical(g3)
    c: DistanceX(g0) = 1
    c: DistanceX(g0,g0) = 31
    c: DistanceY(g3,g3) = 39
    c: Horizontal(g4)
    c: Horizontal(g6)
    c: Vertical(g5)
    c: Tangent(g6,g8) = -1.5708
    c: Tangent(g7,g9) = -1.5708
    c: Tangent(g6,g9) = -1.5708
    c: Tangent(g4,g10) = -1.5708
    c: Tangent(g7,g10) = -1.5708
    c: Tangent(g5,g11) = -1.5708
    c: Tangent(g4,g11) = -1.5708
    c: Coincident(g0,g11)
    c: Coincident(g0,g10)
    c: Coincident(g1,g9)
    c: Coincident(g2,g8)
    c: Radius(g10) = 0.25
    c: DistanceY(g4,g-1) = 1.5
    c: Coincident(g13,g14)
    c: Coincident(g14,g12)
    c: Horizontal(g12)
    c: Horizontal(g13)
    c: Vertical(g14)
    c: Tangent(g5,g15)
    c: Coincident(g13,g15)
    c: DistanceY(g13,g-1) = 35
    c: Coincident(g5,g12)
    c: DistanceY(g12,g-1) = 3.5
    c: Tangent(g8,g15) = -1.5708
    c: DistanceX(g12,g-1) = 2
FEATURE [Sketcher::SketchObject] Sketch068  label="wp cavity esp"
  AttachmentOffset = pos=(0,0,5) rot=(0,0,1;0rad)
  FullyConstrained = false
  MapMode = 5
  Placement = pos=(0,-5,-1.1e-15) rot=(1,0,0;1.5708rad)
  Support = -> [XZ_Plane007]
  sketch-geometry (12):
    g0: LineSegment StartX=1 StartY=-1.75 StartZ=0 EndX=32 EndY=-1.75 EndZ=0
    g1: LineSegment StartX=32 StartY=-1.75 StartZ=0 EndX=32 EndY=-40.75 EndZ=0
    g2: LineSegment StartX=32 StartY=-40.75 StartZ=0 EndX=1 EndY=-40.75 EndZ=0
    g3: LineSegment StartX=1 StartY=-40.75 StartZ=0 EndX=1 EndY=-1.75 EndZ=0
    g4: LineSegment StartX=32 StartY=-1.5 StartZ=0 EndX=1 EndY=-1.5 EndZ=0
    g5: LineSegment StartX=0.75 StartY=-1.75 StartZ=0 EndX=0.75 EndY=-40.75 EndZ=0
    g6: LineSegment StartX=1 StartY=-41 StartZ=0 EndX=32 EndY=-41 EndZ=0
    g7: LineSegment StartX=32.25 StartY=-40.75 StartZ=0 EndX=32.25 EndY=-1.75 EndZ=0
    g8: ArcOfCircle CenterX=1 CenterY=-40.75 CenterZ=0 NormalX=0 NormalY=0 NormalZ=1 AngleXU=0 Radius=0.25 StartAngle=3.14159 EndAngle=4.71239
    g9: ArcOfCircle CenterX=32 CenterY=-40.75 CenterZ=0 NormalX=0 NormalY=0 NormalZ=1 AngleXU=0 Radius=0.25 StartAngle=4.71239 EndAngle=6.28319
    g10: ArcOfCircle CenterX=32 CenterY=-1.75 CenterZ=0 NormalX=0 NormalY=0 NormalZ=1 AngleXU=0 Radius=0.25 StartAngle=1e-16 EndAngle=1.5708
    g11: ArcOfCircle CenterX=1 CenterY=-1.75 CenterZ=0 NormalX=0 NormalY=0 NormalZ=1 AngleXU=0 Radius=0.25 StartAngle=1.5708 EndAngle=3.14159
  constraints (28):
    c: Coincident(g0,g1)
    c: Coincident(g1,g2)
    c: Coincident(g2,g3)
    c: Coincident(g3,g0)
    c: Horizontal(g0)
    c: Horizontal(g2)
    c: Vertical(g1)
    c: Vertical(g3)
    c: DistanceX(g0) = 1
    c: DistanceX(g0,g0) = 31
    c: DistanceY(g3,g3) = 39
    c: Horizontal(g4)
    c: Horizontal(g6)
    c: Vertical(g5)
    c: Tangent(g5,g8) = -1.5708
    c: Tangent(g6,g8) = -1.5708
    c: Tangent(g7,g9) = -1.5708
    c: Tangent(g6,g9) = -1.5708
    c: Tangent(g4,g10) = -1.5708
    c: Tangent(g7,g10) = -1.5708
    c: Tangent(g5,g11) = -1.5708
    c: Tangent(g4,g11) = -1.5708
    c: Coincident(g0,g11)
    c: Coincident(g0,g10)
    c: Coincident(g1,g9)
    c: Coincident(g2,g8)
    c: Radius(g10) = 0.25
    c: DistanceY(g4,g-1) = 1.5
FEATURE [PartDesign::Pocket] Pocket013  label="WP Cavity ESP"
  BaseFeature = -> AdditivePipe
  Length = 5
  Length2 = 100
  Profile = -> Sketch068
  Reversed = true
  Type = 1
FEATURE [PartDesign::Mirrored] Mirrored001  label="WP Cavity adaptor"
  BaseFeature = -> Pocket013
  MirrorPlane = -> YZ_Plane007
  Originals = -> [Pocket013]
FEATURE [Sketcher::SketchObject] Sketch069  label="hb cavity wires"
  AttachmentOffset = pos=(0,0,4) rot=(0,0,1;0rad)
  ExternalGeometry = -> [Sketch067]
  FullyConstrained = false
  MapMode = 5
  Placement = pos=(0,-4,-9e-16) rot=(1,0,0;1.5708rad)
  Support = -> [XZ_Plane013]
  sketch-geometry (9):
    g0: ArcOfCircle CenterX=29 CenterY=-9.5 CenterZ=0 NormalX=0 NormalY=0 NormalZ=1 AngleXU=0 Radius=2.6 StartAngle=3e-16 EndAngle=3.14159
    g1: ArcOfCircle CenterX=29 CenterY=-34.5 CenterZ=0 NormalX=0 NormalY=0 NormalZ=1 AngleXU=0 Radius=2.6 StartAngle=3.14159 EndAngle=6.28319
    g2: LineSegment StartX=26.4 StartY=-9.5 StartZ=0 EndX=26.4 EndY=-34.5 EndZ=0
    g3: LineSegment StartX=31.6 StartY=-9.5 StartZ=0 EndX=31.6 EndY=-34.5 EndZ=0
    g4: ArcOfCircle CenterX=4 CenterY=-9.5 CenterZ=0 NormalX=0 NormalY=0 NormalZ=1 AngleXU=0 Radius=2.6 StartAngle=2e-16 EndAngle=3.14159
    g5: ArcOfCircle CenterX=4 CenterY=-34.5 CenterZ=0 NormalX=0 NormalY=0 NormalZ=1 AngleXU=0 Radius=2.6 StartAngle=3.14159 EndAngle=6.28319
    g6: LineSegment StartX=1.4 StartY=-9.5 StartZ=0 EndX=1.4 EndY=-34.5 EndZ=0
    g7: LineSegment StartX=6.6 StartY=-9.5 StartZ=0 EndX=6.6 EndY=-34.5 EndZ=0
    g8: LineSegment StartX=16.5 StartY=0 StartZ=0 EndX=16.5 EndY=-39 EndZ=0
  constraints (22):
    c: Tangent(g0,g3)
    c: Tangent(g0,g2)
    c: Tangent(g2,g1)
    c: Tangent(g3,g1)
    c: Vertical(g2)
    c: Equal(g0,g1)
    c: Tangent(g4,g7)
    c: Tangent(g4,g6)
    c: Tangent(g6,g5)
    c: Tangent(g7,g5)
    c: Vertical(g6)
    c: Equal(g4,g5)
    c: PointOnObject(g8,g-1)
    c: Symmetric(g0,g4,g8)
    c: Equal(g4,g0)
    c: Radius(g0) = 2.6
    c: DistanceX(g4,g0) = 25
    c: Equal(g3,g7)
    c: DistanceY(g1,g0) = 25
    c: DistanceY(g0,g-1) = 9.5
    c: Symmetric(g-4,g-3,g8)
    c: Equal(g-3,g8)
FEATURE [Sketcher::SketchObject] Sketch070  label="hb hole USB port"
  FullyConstrained = false
  MapMode = 5
  Support = -> [XY_Plane013]
  sketch-geometry (7):
    g0: ArcOfCircle CenterX=13.95 CenterY=-7.35 CenterZ=0 NormalX=0 NormalY=0 NormalZ=1 AngleXU=0 Radius=1.45 StartAngle=1.5708 EndAngle=3.14159
    g1: ArcOfCircle CenterX=19.55 CenterY=-7.35 CenterZ=0 NormalX=0 NormalY=0 NormalZ=1 AngleXU=0 Radius=1.45 StartAngle=1e-16 EndAngle=1.5708
    g2: LineSegment StartX=13.95 StartY=-5.9 StartZ=0 EndX=19.55 EndY=-5.9 EndZ=0
    g3: LineSegment StartX=16.75 StartY=-5.9 StartZ=0 EndX=16.75 EndY=-12 EndZ=0
    g4: LineSegment StartX=21 StartY=-7.35 StartZ=0 EndX=21 EndY=-12 EndZ=0
    g5: LineSegment StartX=21 StartY=-12 StartZ=0 EndX=12.5 EndY=-12 EndZ=0
    g6: LineSegment StartX=12.5 StartY=-12 StartZ=0 EndX=12.5 EndY=-7.35 EndZ=0
  constraints (19):
    c: Tangent(g0,g2)
    c: Tangent(g2,g1)
    c: Equal(g0,g1)
    c: PointOnObject(g3,g2)
    c: Symmetric(g1,g0,g3)
    c: DistanceX(g3) = 16.75
    c: DistanceY(g1,g-1) = 7.35
    c: Radius(g1) = 1.45
    c: DistanceX(g2,g2) = 5.6
    c: Coincident(g4,g5)
    c: Coincident(g5,g6)
    c: Horizontal(g5)
    c: Vertical(g4)
    c: Vertical(g6)
    c: PointOnObject(g3,g5)
    c: Horizontal(g2)
    c: Tangent(g1,g4) = 1.5708
    c: Tangent(g0,g6) = 1.5708
    c: DistanceY(g4,g-1) = 12
FEATURE [Sketcher::SketchObject] Sketch071  label="ht cavity screen visible low"
  AttachmentOffset = pos=(0,0,21) rot=(0,0,1;0rad)
  FullyConstrained = false
  MapMode = 5
  Placement = pos=(0,-21,-4.7e-15) rot=(1,0,0;1.5708rad)
  Support = -> [XZ_Plane014]
  sketch-geometry (12):
    g0: LineSegment StartX=-24.48 StartY=18.36 StartZ=0 EndX=24.48 EndY=18.36 EndZ=0
    g1: LineSegment StartX=24.48 StartY=18.36 StartZ=0 EndX=24.48 EndY=-18.36 EndZ=0
    g2: LineSegment StartX=24.48 StartY=-18.36 StartZ=0 EndX=-24.48 EndY=-18.36 EndZ=0
    g3: LineSegment StartX=-24.48 StartY=-18.36 StartZ=0 EndX=-24.48 EndY=18.36 EndZ=0
    g4: LineSegment StartX=-24.48 StartY=18.86 StartZ=0 EndX=24.48 EndY=18.86 EndZ=0
    g5: LineSegment StartX=24.98 StartY=18.36 StartZ=0 EndX=24.98 EndY=-18.36 EndZ=0
    g6: LineSegment StartX=24.48 StartY=-18.86 StartZ=0 EndX=-24.48 EndY=-18.86 EndZ=0
    g7: LineSegment StartX=-24.98 StartY=-18.36 StartZ=0 EndX=-24.98 EndY=18.36 EndZ=0
    g8: ArcOfCircle CenterX=24.48 CenterY=18.36 CenterZ=0 NormalX=0 NormalY=0 NormalZ=1 AngleXU=0 Radius=0.5 StartAngle=1.76704e-11 EndAngle=1.5708
    g9: ArcOfCircle CenterX=-24.48 CenterY=18.36 CenterZ=0 NormalX=0 NormalY=0 NormalZ=1 AngleXU=0 Radius=0.5 StartAngle=1.5708 EndAngle=3.14159
    g10: ArcOfCircle CenterX=-24.48 CenterY=-18.36 CenterZ=0 NormalX=0 NormalY=0 NormalZ=1 AngleXU=0 Radius=0.5 StartAngle=3.14159 EndAngle=4.71239
    g11: ArcOfCircle CenterX=24.48 CenterY=-18.36 CenterZ=0 NormalX=0 NormalY=0 NormalZ=1 AngleXU=0 Radius=0.5 StartAngle=4.71239 EndAngle=6.28319
  constraints (26):
    c: Coincident(g0,g1)
    c: Coincident(g1,g2)
    c: Coincident(g2,g3)
    c: Coincident(g3,g0)
    c: Horizontal(g2)
    c: Vertical(g3)
    c: Symmetric(g0,g0,g-2)
    c: Symmetric(g1,g0,g-1)
    c: Horizontal(g4)
    c: Horizontal(g6)
    c: Vertical(g5)
    c: Tangent(g5,g8) = 1.5708
    c: Tangent(g4,g8) = 1.5708
    c: Tangent(g4,g9) = 1.5708
    c: Tangent(g7,g9) = 1.5708
    c: Tangent(g7,g10) = 1.5708
    c: Tangent(g6,g10) = 1.5708
    c: Tangent(g6,g11) = 1.5708
    c: Tangent(g5,g11) = 1.5708
    c: Coincident(g1,g11)
    c: DistanceY(g1,g1) = 36.72
    c: DistanceX(g0,g0) = 48.96
    c: Coincident(g0,g8)
    c: Coincident(g2,g10)
    c: Coincident(g0,g9)
    c: Radius(g8) = 0.5
FEATURE [Sketcher::SketchObject] Sketch072  label="ht cavity screen visible high"
  AttachmentOffset = pos=(0,0,22.1) rot=(0,0,1;0rad)
  FullyConstrained = false
  MapMode = 5
  Placement = pos=(0,-22.1,-4.9e-15) rot=(1,0,0;1.5708rad)
  Support = -> [XZ_Plane014]
  sketch-geometry (12):
    g0: LineSegment StartX=-24.48 StartY=18.36 StartZ=0 EndX=24.48 EndY=18.36 EndZ=0
    g1: LineSegment StartX=24.48 StartY=18.36 StartZ=0 EndX=24.48 EndY=-18.36 EndZ=0
    g2: LineSegment StartX=24.48 StartY=-18.36 StartZ=0 EndX=-24.48 EndY=-18.36 EndZ=0
    g3: LineSegment StartX=-24.48 StartY=-18.36 StartZ=0 EndX=-24.48 EndY=18.36 EndZ=0
    g4: LineSegment StartX=-24.48 StartY=19.56 StartZ=0 EndX=24.48 EndY=19.56 EndZ=0
    g5: LineSegment StartX=25.68 StartY=18.36 StartZ=0 EndX=25.68 EndY=-18.36 EndZ=0
    g6: LineSegment StartX=24.48 StartY=-19.56 StartZ=0 EndX=-24.48 EndY=-19.56 EndZ=0
    g7: LineSegment StartX=-25.68 StartY=-18.36 StartZ=0 EndX=-25.68 EndY=18.36 EndZ=0
    g8: ArcOfCircle CenterX=24.48 CenterY=18.36 CenterZ=0 NormalX=0 NormalY=0 NormalZ=1 AngleXU=0 Radius=1.2 StartAngle=-5.187e-13 EndAngle=1.5708
    g9: ArcOfCircle CenterX=-24.48 CenterY=18.36 CenterZ=0 NormalX=0 NormalY=0 NormalZ=1 AngleXU=0 Radius=1.2 StartAngle=1.5708 EndAngle=3.14159
    g10: ArcOfCircle CenterX=-24.48 CenterY=-18.36 CenterZ=0 NormalX=0 NormalY=0 NormalZ=1 AngleXU=0 Radius=1.2 StartAngle=3.14159 EndAngle=4.71239
    g11: ArcOfCircle CenterX=24.48 CenterY=-18.36 CenterZ=0 NormalX=0 NormalY=0 NormalZ=1 AngleXU=0 Radius=1.2 StartAngle=4.71239 EndAngle=6.28319
  constraints (26):
    c: Coincident(g0,g1)
    c: Coincident(g1,g2)
    c: Coincident(g2,g3)
    c: Coincident(g3,g0)
    c: Horizontal(g2)
    c: Vertical(g3)
    c: Symmetric(g0,g0,g-2)
    c: Symmetric(g1,g0,g-1)
    c: Horizontal(g4)
    c: Horizontal(g6)
    c: Vertical(g5)
    c: Tangent(g5,g8) = 1.5708
    c: Tangent(g4,g8) = 1.5708
    c: Tangent(g4,g9) = 1.5708
    c: Tangent(g7,g9) = 1.5708
    c: Tangent(g7,g10) = 1.5708
    c: Tangent(g6,g10) = 1.5708
    c: Tangent(g6,g11) = 1.5708
    c: Tangent(g5,g11) = 1.5708
    c: Coincident(g1,g11)
    c: DistanceY(g1,g1) = 36.72
    c: DistanceX(g0,g0) = 48.96
    c: Coincident(g0,g8)
    c: Coincident(g2,g10)
    c: Coincident(g0,g9)
    c: Radius(g8) = 1.2
FEATURE [Sketcher::SketchObject] Sketch073  label="hp screen glass cavity"
  AttachmentOffset = pos=(0,0,21.1) rot=(0,0,1;0rad)
  FullyConstrained = false
  MapMode = 5
  Placement = pos=(0,-21.1,-4.7e-15) rot=(1,0,0;1.5708rad)
  Support = -> [XZ_Plane014]
  sketch-geometry (28):
    g0: LineSegment StartX=-33.6 StartY=21.55 StartZ=0 EndX=27.1 EndY=21.55 EndZ=0
    g1: LineSegment StartX=27.1 StartY=21.55 StartZ=0 EndX=27.1 EndY=-21.55 EndZ=0
    g2: LineSegment StartX=27.1 StartY=-21.55 StartZ=0 EndX=-33.6 EndY=-21.55 EndZ=0
    g3: LineSegment StartX=-33.6 StartY=-21.55 StartZ=0 EndX=-33.6 EndY=21.55 EndZ=0
    g4: LineSegment StartX=-28.4038 StartY=23.05 StartZ=0 EndX=21.9038 EndY=23.05 EndZ=0
    g5: LineSegment StartX=28.6 StartY=21.55 StartZ=0 EndX=28.6 EndY=2.59808 EndZ=0
    g6: LineSegment StartX=27.1 StartY=-23.05 StartZ=0 EndX=2.59808 EndY=-23.05 EndZ=0
    g7: LineSegment StartX=-35.1 StartY=-21.55 StartZ=0 EndX=-35.1 EndY=-2.59808 EndZ=0
    g8: ArcOfCircle CenterX=27.1 CenterY=21.55 CenterZ=0 NormalX=0 NormalY=0 NormalZ=1 AngleXU=0 Radius=1.5 StartAngle=4e-16 EndAngle=2.61799
    g9: ArcOfCircle CenterX=-33.6 CenterY=21.55 CenterZ=0 NormalX=0 NormalY=0 NormalZ=1 AngleXU=0 Radius=1.5 StartAngle=0.523599 EndAngle=3.14159
    g10: ArcOfCircle CenterX=-33.6 CenterY=-21.55 CenterZ=0 NormalX=0 NormalY=0 NormalZ=1 AngleXU=0 Radius=1.5 StartAngle=3.14159 EndAngle=4.71239
    g11: ArcOfCircle CenterX=27.1 CenterY=-21.55 CenterZ=0 NormalX=0 NormalY=0 NormalZ=1 AngleXU=0 Radius=1.5 StartAngle=4.71239 EndAngle=6.28319
    g12: ArcOfCircle CenterX=24.5019 CenterY=23.05 CenterZ=0 NormalX=0 NormalY=0 NormalZ=1 AngleXU=0 Radius=1.5 StartAngle=3.66519 EndAngle=5.75959
    g13: ArcOfCircle CenterX=21.9038 CenterY=21.55 CenterZ=0 NormalX=0 NormalY=0 NormalZ=1 AngleXU=0 Radius=1.5 StartAngle=0.523599 EndAngle=1.5708
    g14: ArcOfCircle CenterX=-31.0019 CenterY=23.05 CenterZ=0 NormalX=0 NormalY=0 NormalZ=1 AngleXU=0 Radius=1.5 StartAngle=3.66519 EndAngle=5.75959
    g15: ArcOfCircle CenterX=-28.4038 CenterY=21.55 CenterZ=0 NormalX=0 NormalY=0 NormalZ=1 AngleXU=0 Radius=1.5 StartAngle=1.5708 EndAngle=2.61799
    g16: ArcOfCircle CenterX=0 CenterY=-23.05 CenterZ=0 NormalX=0 NormalY=0 NormalZ=1 AngleXU=0 Radius=1.5 StartAngle=0.523599 EndAngle=2.61799
    g17: ArcOfCircle CenterX=2.59808 CenterY=-21.55 CenterZ=0 NormalX=0 NormalY=0 NormalZ=1 AngleXU=0 Radius=1.5 StartAngle=3.66519 EndAngle=4.71239
    g18: ArcOfCircle CenterX=-2.59808 CenterY=-21.55 CenterZ=0 NormalX=0 NormalY=0 NormalZ=1 AngleXU=0 Radius=1.5 StartAngle=4.71239 EndAngle=5.75959
    g19: LineSegment StartX=-2.59808 StartY=-23.05 StartZ=0 EndX=-33.6 EndY=-23.05 EndZ=0
    g20: ArcOfCircle CenterX=-35.1 CenterY=0 CenterZ=0 NormalX=0 NormalY=0 NormalZ=1 AngleXU=0 Radius=1.5 StartAngle=5.23599 EndAngle=7.33038
    g21: ArcOfCircle CenterX=-33.6 CenterY=2.59808 CenterZ=0 NormalX=0 NormalY=0 NormalZ=1 AngleXU=0 Radius=1.5 StartAngle=3.14159 EndAngle=4.18879
    g22: ArcOfCircle CenterX=-33.6 CenterY=-2.59808 CenterZ=0 NormalX=0 NormalY=0 NormalZ=1 AngleXU=0 Radius=1.5 StartAngle=2.0944 EndAngle=3.14159
    g23: LineSegment StartX=-35.1 StartY=2.59808 StartZ=0 EndX=-35.1 EndY=21.55 EndZ=0
    g24: ArcOfCircle CenterX=28.6 CenterY=0 CenterZ=0 NormalX=0 NormalY=0 NormalZ=1 AngleXU=0 Radius=1.5 StartAngle=2.0944 EndAngle=4.18879
    g25: ArcOfCircle CenterX=27.1 CenterY=2.59808 CenterZ=0 NormalX=0 NormalY=0 NormalZ=1 AngleXU=0 Radius=1.5 StartAngle=5.23599 EndAngle=6.28319
    g26: ArcOfCircle CenterX=27.1 CenterY=-2.59808 CenterZ=0 NormalX=0 NormalY=0 NormalZ=1 AngleXU=0 Radius=1.5 StartAngle=0 EndAngle=1.0472
    g27: LineSegment StartX=28.6 StartY=-2.59808 StartZ=0 EndX=28.6 EndY=-21.55 EndZ=0
  constraints (69):
    c: Coincident(g0,g1)
    c: Coincident(g1,g2)
    c: Coincident(g2,g3)
    c: Coincident(g3,g0)
    c: Horizontal(g2)
    c: Vertical(g3)
    c: Symmetric(g0,g1,g-1)
    c: DistanceY(g1,g1) = 43.1
    c: Horizontal(g4)
    c: Horizontal(g6)
    c: Vertical(g5)
    c: Tangent(g5,g8) = 1.5708
    c: Tangent(g7,g10) = 1.5708
    c: Tangent(g6,g11) = 1.5708
    c: Coincident(g1,g11)
    c: Coincident(g0,g8)
    c: Coincident(g0,g9)
    c: Coincident(g2,g10)
    c: Radius(g8) = 1.5
    c: Tangent(g12,g13) = 1.5708
    c: Tangent(g12,g0)
    c: Equal(g8,g12)
    c: Equal(g12,g13)
    c: Tangent(g8,g12) = 1.5708
    c: Equal(g8,g9)
    c: Tangent(g4,g13) = 1.5708
    c: Equal(g15,g14)
    c: Equal(g14,g9)
    c: Tangent(g14,g0)
    c: Tangent(g9,g14) = 1.5708
    c: Tangent(g14,g15) = 1.5708
    c: Tangent(g4,g15) = 1.5708
    c: Tangent(g9,g4)
    c: PointOnObject(g16,g-2)
    c: Tangent(g16,g2)
    c: Equal(g16,g11)
    c: Tangent(g6,g19)
    c: Tangent(g6,g17) = 1.5708
    c: Tangent(g18,g19) = 1.5708
    c: Tangent(g16,g18) = 1.5708
    c: Tangent(g16,g17) = 1.5708
    c: Equal(g17,g18)
    c: Equal(g18,g16)
    c: Tangent(g10,g19) = 1.5708
    c: PointOnObject(g20,g-1)
    c: Tangent(g20,g22) = 1.5708
    c: Tangent(g20,g21) = 1.5708
    c: Tangent(g3,g20)
    c: Tangent(g7,g23)
    c: Equal(g20,g22)
    c: Equal(g22,g21)
    c: Equal(g21,g9)
    c: Tangent(g21,g23) = 1.5708
    c: Tangent(g7,g22) = 1.5708
    c: Tangent(g9,g23) = 1.5708
    c: PointOnObject(g24,g-1)
    c: Tangent(g5,g27)
    c: Tangent(g27,g26) = 1.5708
    c: Tangent(g26,g24) = 1.5708
    c: Tangent(g24,g25) = 1.5708
    c: Tangent(g5,g25) = 1.5708
    c: Tangent(g24,g1)
    c: Equal(g24,g25)
    c: Equal(g25,g26)
    c: Equal(g26,g8)
    c: Tangent(g11,g27) = 1.5708
    c: DistanceX(g9,g-1) = 33.6
    c: Horizontal(g0)
    c: DistanceX(g8) = 27.1
FEATURE [Sketcher::SketchObject] Sketch074  label="hp cutout pcb"
  AttachmentOffset = pos=(0,0,18) rot=(0,0,1;0rad)
  ExternalGeometry = -> [Sketch061]
  FullyConstrained = true
  MapMode = 5
  Placement = pos=(0,-18,-4e-15) rot=(1,0,0;1.5708rad)
  Support = -> [XZ_Plane014]
  sketch-geometry (30):
    g0: LineSegment StartX=-43.7 StartY=24.5 StartZ=0 EndX=-38.5 EndY=24.5 EndZ=0
    g1: LineSegment StartX=37 StartY=-28.5 StartZ=0 EndX=37 EndY=-35.2157 EndZ=0
    g2: LineSegment StartX=-45.2 StartY=-25.5 StartZ=0 EndX=-45.2 EndY=23 EndZ=0
    g3: ArcOfCircle CenterX=-43.7 CenterY=23 CenterZ=0 NormalX=0 NormalY=0 NormalZ=1 AngleXU=0 Radius=1.5 StartAngle=1.5708 EndAngle=3.14159
    g4: ArcOfCircle CenterX=43.7 CenterY=23 CenterZ=0 NormalX=0 NormalY=0 NormalZ=1 AngleXU=0 Radius=1.5 StartAngle=0 EndAngle=1.5708
    g5: ArcOfCircle CenterX=-43.7 CenterY=-25.5 CenterZ=0 NormalX=0 NormalY=0 NormalZ=1 AngleXU=0 Radius=1.5 StartAngle=3.14159 EndAngle=4.71239
    g6: LineSegment StartX=-38.5 StartY=-27 StartZ=0 EndX=-43.7 EndY=-27 EndZ=0
    g7: Circle CenterX=-40 CenterY=-30 CenterZ=0 NormalX=0 NormalY=0 NormalZ=1 AngleXU=0 Radius=3
    g8: Circle CenterX=40 CenterY=-30 CenterZ=0 NormalX=0 NormalY=0 NormalZ=1 AngleXU=0 Radius=3
    g9: LineSegment StartX=-37 StartY=-28.5 StartZ=0 EndX=-37 EndY=-35.2157 EndZ=0
    g10: ArcOfCircle CenterX=-35.5 CenterY=-35.2157 CenterZ=0 NormalX=0 NormalY=0 NormalZ=1 AngleXU=0 Radius=1.5 StartAngle=3.14159 EndAngle=4.52788
    g11: ArcOfCircle CenterX=35.5 CenterY=-35.2157 CenterZ=0 NormalX=0 NormalY=0 NormalZ=1 AngleXU=0 Radius=1.5 StartAngle=4.8969 EndAngle=6.28319
    g12: ArcOfCircle CenterX=-38.5 CenterY=-28.5 CenterZ=0 NormalX=0 NormalY=0 NormalZ=1 AngleXU=0 Radius=1.5 StartAngle=5e-16 EndAngle=1.5708
    g13: LineSegment StartX=38.5 StartY=-27 StartZ=0 EndX=43.7 EndY=-27 EndZ=0
    g14: ArcOfCircle CenterX=38.5 CenterY=-28.5 CenterZ=0 NormalX=0 NormalY=0 NormalZ=1 AngleXU=0 Radius=1.5 StartAngle=1.5708 EndAngle=3.14159
    g15: LineSegment StartX=45.2 StartY=23 StartZ=0 EndX=45.2 EndY=-25.5 EndZ=0
    g16: ArcOfCircle CenterX=43.7 CenterY=-25.5 CenterZ=0 NormalX=0 NormalY=0 NormalZ=1 AngleXU=0 Radius=1.5 StartAngle=4.71239 EndAngle=6.28319
    g17: ArcOfCircle CenterX=-6.477e-13 CenterY=155 CenterZ=0 NormalX=0 NormalY=0 NormalZ=1 AngleXU=0 Radius=195 StartAngle=4.52788 EndAngle=4.8969
    g18: ArcOfCircle CenterX=-6.477e-13 CenterY=-155 CenterZ=0 NormalX=0 NormalY=0 NormalZ=1 AngleXU=0 Radius=195 StartAngle=1.38629 EndAngle=1.7553
    g19: LineSegment StartX=-37 StartY=35.2157 StartZ=0 EndX=-37 EndY=26 EndZ=0
    g20: LineSegment StartX=37 StartY=35.2157 StartZ=0 EndX=37 EndY=26 EndZ=0
    g21: ArcOfCircle CenterX=35.5 CenterY=35.2157 CenterZ=0 NormalX=0 NormalY=0 NormalZ=1 AngleXU=0 Radius=1.5 StartAngle=2.2e-15 EndAngle=1.38629
    g22: ArcOfCircle CenterX=-35.5 CenterY=35.2157 CenterZ=0 NormalX=0 NormalY=0 NormalZ=1 AngleXU=0 Radius=1.5 StartAngle=1.7553 EndAngle=3.14159
    g23: LineSegment StartX=38.5 StartY=24.5 StartZ=0 EndX=43.7 EndY=24.5 EndZ=0
    g24: ArcOfCircle CenterX=38.5 CenterY=26 CenterZ=0 NormalX=0 NormalY=0 NormalZ=1 AngleXU=0 Radius=1.5 StartAngle=3.14159 EndAngle=4.71239
    g25: ArcOfCircle CenterX=-38.5 CenterY=26 CenterZ=0 NormalX=0 NormalY=0 NormalZ=1 AngleXU=0 Radius=1.5 StartAngle=4.71239 EndAngle=6.28319
    g26: LineSegment StartX=-38.5 StartY=26 StartZ=0 EndX=38.5 EndY=26 EndZ=0
    g27: LineSegment StartX=38.5 StartY=26 StartZ=0 EndX=38.5 EndY=-28.5 EndZ=0
    g28: LineSegment StartX=38.5 StartY=-28.5 StartZ=0 EndX=-38.5 EndY=-28.5 EndZ=0
    g29: LineSegment StartX=-38.5 StartY=-28.5 StartZ=0 EndX=-38.5 EndY=26 EndZ=0
  constraints (71):
    c: DistanceX(g3,g-1) = 43.7
    c: Horizontal(g0)
    c: Vertical(g1)
    c: Tangent(g0,g3) = 1.5708
    c: Tangent(g2,g3) = 1.5708
    c: Tangent(g2,g5) = 1.5708
    c: Radius(g4) = 1.5
    c: Tangent(g5,g6) = 1.5708
    c: Symmetric(g8,g7,g-2)
    c: DistanceX(g7,g8) = 80
    c: DistanceY(g8,g-1) = 30
    c: Equal(g7,g8)
    c: Radius(g8) = 3
    c: Vertical(g9)
    c: Tangent(g9,g7)
    c: Tangent(g9,g10) = -1.5708
    c: Equal(g10,g5)
    c: Equal(g5,g3)
    c: Horizontal(g6)
    c: Vertical(g2)
    c: Equal(g4,g5)
    c: Tangent(g8,g1)
    c: Tangent(g1,g11) = 1.5708
    c: Equal(g11,g4)
    c: DistanceY(g4) = 23
    c: Tangent(g9,g12) = 1.5708
    c: Tangent(g6,g12) = -1.5708
    c: Equal(g12,g4)
    c: Tangent(g7,g6)
    c: Horizontal(g13)
    c: Tangent(g1,g14) = -1.5708
    c: Tangent(g13,g14) = 1.5708
    c: Equal(g14,g4)
    c: Vertical(g15)
    c: Tangent(g13,g16) = -1.5708
    c: Tangent(g15,g16) = 1.5708
    c: Equal(g16,g4)
    c: Symmetric(g16,g5,g-2)
    c: Tangent(g4,g15) = 1.5708
    c: Coincident(g17,g-3)
    c: Radius(g17) = 195
    c: Tangent(g10,g17) = -1.5708
    c: Tangent(g11,g17) = -1.5708
    c: Equal(g17,g18)
    c: Symmetric(g18,g17,g-1)
    c: Vertical(g19)
    c: Vertical(g20)
    c: Tangent(g20,g21) = 1.5708
    c: Tangent(g18,g21) = -1.5708
    c: Tangent(g18,g22) = -1.5708
    c: Tangent(g19,g22) = -1.5708
    c: Tangent(g0,g23)
    c: Tangent(g23,g24) = -1.5708
    c: Tangent(g20,g24) = -1.5708
    c: Tangent(g19,g25) = 1.5708
    c: Tangent(g0,g25) = -1.5708
    c: Equal(g4,g24)
    c: Equal(g24,g21)
    c: Equal(g21,g22)
    c: Equal(g22,g25)
    c: Coincident(g26,g27)
    c: Coincident(g27,g28)
    c: Coincident(g28,g29)
    c: Coincident(g29,g26)
    c: Vertical(g27)
    c: Vertical(g29)
    c: Coincident(g26,g25)
    c: Coincident(g27,g14)
    c: Coincident(g12,g28)
    c: Coincident(g24,g26)
    c: Tangent(g4,g23) = 1.5708
FEATURE [Sketcher::SketchObject] Sketch083  label="hb magnet hole"
  AttachmentOffset = pos=(0,0,25) rot=(0,0,1;0rad)
  FullyConstrained = false
  MapMode = 5
  Placement = pos=(0,0,25) rot=(0,0,1;0rad)
  Support = -> [XY_Plane013]
  sketch-geometry (5):
    g0: LineSegment StartX=-50 StartY=-3.8 StartZ=0 EndX=-44.85 EndY=-3.8 EndZ=0
    g1: LineSegment StartX=-44.85 StartY=-3.8 StartZ=0 EndX=-44.85 EndY=-13.8 EndZ=0
    g2: LineSegment StartX=-44.85 StartY=-13.8 StartZ=0 EndX=-50 EndY=-13.8 EndZ=0
    g3: LineSegment StartX=-50 StartY=-13.8 StartZ=0 EndX=-50 EndY=-3.8 EndZ=0
    g4: LineSegment StartX=-50 StartY=-3.8 StartZ=0 EndX=-50 EndY=0 EndZ=0
  constraints (15):
    c: Coincident(g0,g1)
    c: Coincident(g1,g2)
    c: Coincident(g2,g3)
    c: Coincident(g3,g0)
    c: Horizontal(g0)
    c: Horizontal(g2)
    c: Vertical(g1)
    c: Vertical(g3)
    c: Coincident(g4,g0)
    c: PointOnObject(g4,g-1)
    c: Vertical(g4)
    c: DistanceY(g4,g4) = 3.8
    c: DistanceX(g0,g0) = 5.15
    c: DistanceY(g1,g1) = 10
    c: DistanceX(g4,g-1) = 50
FEATURE [Sketcher::SketchObject] Sketch084  label="wp magnet hole"
  AttachmentOffset = pos=(0,0,25) rot=(0,0,1;0rad)
  FullyConstrained = false
  MapMode = 5
  Placement = pos=(0,0,25) rot=(0,0,1;0rad)
  Support = -> [XY_Plane007]
  sketch-geometry (5):
    g0: LineSegment StartX=-50 StartY=-5 StartZ=0 EndX=-44.85 EndY=-5 EndZ=0
    g1: LineSegment StartX=-44.85 StartY=-5 StartZ=0 EndX=-44.85 EndY=-0.75 EndZ=0
    g2: LineSegment StartX=-44.85 StartY=-0.75 StartZ=0 EndX=-50 EndY=-0.75 EndZ=0
    g3: LineSegment StartX=-50 StartY=-0.75 StartZ=0 EndX=-50 EndY=-5 EndZ=0
    g4: LineSegment StartX=-50 StartY=-0.75 StartZ=0 EndX=-50 EndY=4.4 EndZ=0
  constraints (15):
    c: Coincident(g0,g1)
    c: Coincident(g1,g2)
    c: Coincident(g2,g3)
    c: Coincident(g3,g0)
    c: Horizontal(g0)
    c: Horizontal(g2)
    c: Vertical(g1)
    c: Vertical(g3)
    c: DistanceY(g0,g-1) = 5
    c: DistanceX(g0,g0) = 5.15
    c: Coincident(g4,g2)
    c: Vertical(g4)
    c: Equal(g2,g4)
    c: DistanceX(g4,g-1) = 50
    c: DistanceY(g2,g-1) = 0.75
FEATURE [PartDesign::Groove] Groove001  label="WP Magnet hole 1"
  Angle = 360
  Axis = (0,5.15,0)
  Base = (-50,-0.75,25)
  BaseFeature = -> Mirrored001
  Profile = -> Sketch084
  ReferenceAxis = -> Sketch084 [Axis0]
FEATURE [Sketcher::SketchObject] Sketch085
  FullyConstrained = false
  MapMode = 5
  Placement = pos=(0,0,0) rot=(1,0,0;1.5708rad)
  Support = -> [XZ_Plane015]
  sketch-geometry (5):
    g0: LineSegment StartX=3.2 StartY=2.75 StartZ=0 EndX=5 EndY=2.75 EndZ=0
    g1: LineSegment StartX=5 StartY=2.75 StartZ=0 EndX=5 EndY=0 EndZ=0
    g2: LineSegment StartX=5 StartY=0 StartZ=0 EndX=1.5 EndY=0 EndZ=0
    g3: LineSegment StartX=1.5 StartY=0 StartZ=0 EndX=1.5 EndY=1.05 EndZ=0
    g4: LineSegment StartX=3.2 StartY=2.75 StartZ=0 EndX=1.5 EndY=1.05 EndZ=0
  constraints (15):
    c: Coincident(g0,g1)
    c: Coincident(g1,g2)
    c: Coincident(g2,g3)
    c: Horizontal(g0)
    c: Horizontal(g2)
    c: Vertical(g1)
    c: Vertical(g3)
    c: PointOnObject(g1,g-1)
    c: DistanceX(g1) = 5
    c: Coincident(g0,g4)
    c: Coincident(g4,g3)
    c: DistanceY(g0) = 2.75
    c: DistanceX(g2) = 1.5
    c: Angle(g3,g4) = 2.35619
    c: DistanceX(g0) = 3.2
FEATURE [PartDesign::Revolution] Revolution003
  Angle = 360
  Axis = (-3e-16,3e-16,1)
  Base = (0,0,0)
  Placement = pos=(0,0,0) rot=(1,0,0;1.5708rad)
  Profile = -> Sketch085
  ReferenceAxis = -> Z_Axis017
  Reversed = true
FEATURE [PartDesign::Body] Body015  label="RingMagnet10x2.75_003"
  Group = -> [Sketch085,Revolution003]
  Origin = -> Origin015
  Placement = pos=(50,-3.5,-25) rot=(0,0.707107,0.707107;3.14159rad)
  Tip = -> Revolution003
FEATURE [Sketcher::SketchObject] Sketch086
  FullyConstrained = false
  MapMode = 5
  Placement = pos=(0,0,0) rot=(1,0,0;1.5708rad)
  Support = -> [XZ_Plane016]
  sketch-geometry (5):
    g0: LineSegment StartX=3.2 StartY=2.75 StartZ=0 EndX=5 EndY=2.75 EndZ=0
    g1: LineSegment StartX=5 StartY=2.75 StartZ=0 EndX=5 EndY=0 EndZ=0
    g2: LineSegment StartX=5 StartY=0 StartZ=0 EndX=1.5 EndY=0 EndZ=0
    g3: LineSegment StartX=1.5 StartY=0 StartZ=0 EndX=1.5 EndY=1.05 EndZ=0
    g4: LineSegment StartX=3.2 StartY=2.75 StartZ=0 EndX=1.5 EndY=1.05 EndZ=0
  constraints (15):
    c: Coincident(g0,g1)
    c: Coincident(g1,g2)
    c: Coincident(g2,g3)
    c: Horizontal(g0)
    c: Horizontal(g2)
    c: Vertical(g1)
    c: Vertical(g3)
    c: PointOnObject(g1,g-1)
    c: DistanceX(g1) = 5
    c: Coincident(g0,g4)
    c: Coincident(g4,g3)
    c: DistanceY(g0) = 2.75
    c: DistanceX(g2) = 1.5
    c: Angle(g3,g4) = 2.35619
    c: DistanceX(g0) = 3.2
FEATURE [PartDesign::Revolution] Revolution002
  Angle = 360
  Axis = (-3e-16,3e-16,1)
  Base = (0,0,0)
  Placement = pos=(0,0,0) rot=(1,0,0;1.5708rad)
  Profile = -> Sketch086
  ReferenceAxis = -> Z_Axis007
  Reversed = true
FEATURE [PartDesign::Body] Body016  label="RingMagnet10x2.75_004"
  Group = -> [Sketch086,Revolution002]
  Origin = -> Origin016
  Placement = pos=(50,-4,-25) rot=(1,0,0;1.5708rad)
  Tip = -> Revolution002
FEATURE [Sketcher::SketchObject] Sketch087  label="hb pcb support right high"
  AttachmentOffset = pos=(0,0,15.5) rot=(0,0,1;0rad)
  FullyConstrained = false
  MapMode = 5
  Placement = pos=(0,-15.5,-3.4e-15) rot=(1,0,0;1.5708rad)
  Support = -> [XZ_Plane013]
  sketch-geometry (7):
    g0: Circle CenterX=30.49 CenterY=18.45 CenterZ=0 NormalX=0 NormalY=0 NormalZ=1 AngleXU=0 Radius=1.5
    g1: LineSegment StartX=27.49 StartY=21.45 StartZ=0 EndX=33.49 EndY=21.45 EndZ=0
    g2: LineSegment StartX=33.49 StartY=21.45 StartZ=0 EndX=33.49 EndY=15.45 EndZ=0
    g3: LineSegment StartX=33.49 StartY=15.45 StartZ=0 EndX=27.49 EndY=15.45 EndZ=0
    g4: LineSegment StartX=27.49 StartY=15.45 StartZ=0 EndX=27.49 EndY=21.45 EndZ=0
    g5: LineSegment StartX=27.49 StartY=18.45 StartZ=0 EndX=33.49 EndY=18.45 EndZ=0
    g6: LineSegment StartX=30.49 StartY=21.45 StartZ=0 EndX=30.49 EndY=15.45 EndZ=0
  constraints (21):
    c: DistanceY(g0) = 18.45
    c: DistanceX(g0) = 30.49
    c: Coincident(g1,g2)
    c: Coincident(g2,g3)
    c: Coincident(g3,g4)
    c: Coincident(g4,g1)
    c: Horizontal(g1)
    c: Horizontal(g3)
    c: Vertical(g2)
    c: Vertical(g4)
    c: Radius(g0) = 1.5
    c: PointOnObject(g5,g4)
    c: PointOnObject(g5,g2)
    c: PointOnObject(g6,g1)
    c: PointOnObject(g6,g3)
    c: Symmetric(g1,g2,g5)
    c: Symmetric(g1,g1,g6)
    c: PointOnObject(g0,g6)
    c: PointOnObject(g0,g5)
    c: Equal(g1,g2)
    c: DistanceX(g1,g1) = 6
FEATURE [Sketcher::SketchObject] Sketch088  label="hb pcb support right low"
  AttachmentOffset = pos=(0,0,9) rot=(0,0,1;0rad)
  FullyConstrained = false
  MapMode = 5
  Placement = pos=(0,-9,-2e-15) rot=(1,0,0;1.5708rad)
  Support = -> [XZ_Plane013]
  sketch-geometry (6):
    g0: Circle CenterX=30.49 CenterY=18.45 CenterZ=0 NormalX=0 NormalY=0 NormalZ=1 AngleXU=0 Radius=1.5
    g1: LineSegment StartX=30 StartY=22.45 StartZ=0 EndX=38 EndY=22.45 EndZ=0
    g2: LineSegment StartX=38 StartY=22.45 StartZ=0 EndX=38 EndY=14.45 EndZ=0
    g3: LineSegment StartX=38 StartY=14.45 StartZ=0 EndX=30 EndY=14.45 EndZ=0
    g4: LineSegment StartX=30 StartY=14.45 StartZ=0 EndX=30 EndY=22.45 EndZ=0
    g5: LineSegment StartX=30 StartY=18.45 StartZ=0 EndX=38 EndY=18.45 EndZ=0
  constraints (18):
    c: DistanceY(g0) = 18.45
    c: DistanceX(g0) = 30.49
    c: Coincident(g1,g2)
    c: Coincident(g2,g3)
    c: Coincident(g3,g4)
    c: Coincident(g4,g1)
    c: Horizontal(g1)
    c: Horizontal(g3)
    c: Vertical(g2)
    c: Vertical(g4)
    c: Radius(g0) = 1.5
    c: PointOnObject(g5,g4)
    c: PointOnObject(g5,g2)
    c: Symmetric(g1,g2,g5)
    c: PointOnObject(g0,g5)
    c: Equal(g1,g2)
    c: DistanceX(g1,g1) = 8
    c: DistanceX(g1) = 30
FEATURE [Sketcher::SketchObject] Sketch089  label="hb pcb support left high"
  AttachmentOffset = pos=(0,0,14.5) rot=(0,0,1;0rad)
  FullyConstrained = false
  MapMode = 5
  Placement = pos=(0,-14.5,-3.2e-15) rot=(1,0,0;1.5708rad)
  Support = -> [XZ_Plane013]
  sketch-geometry (7):
    g0: Circle CenterX=-36.77 CenterY=18.45 CenterZ=0 NormalX=0 NormalY=0 NormalZ=1 AngleXU=0 Radius=1.5
    g1: LineSegment StartX=-39.77 StartY=21.45 StartZ=0 EndX=-33.77 EndY=21.45 EndZ=0
    g2: LineSegment StartX=-33.77 StartY=21.45 StartZ=0 EndX=-33.77 EndY=15.45 EndZ=0
    g3: LineSegment StartX=-33.77 StartY=15.45 StartZ=0 EndX=-39.77 EndY=15.45 EndZ=0
    g4: LineSegment StartX=-39.77 StartY=15.45 StartZ=0 EndX=-39.77 EndY=21.45 EndZ=0
    g5: LineSegment StartX=-39.77 StartY=18.45 StartZ=0 EndX=-33.77 EndY=18.45 EndZ=0
    g6: LineSegment StartX=-36.77 StartY=21.45 StartZ=0 EndX=-36.77 EndY=15.45 EndZ=0
  constraints (21):
    c: DistanceY(g0) = 18.45
    c: Coincident(g1,g2)
    c: Coincident(g2,g3)
    c: Coincident(g3,g4)
    c: Coincident(g4,g1)
    c: Horizontal(g1)
    c: Horizontal(g3)
    c: Vertical(g2)
    c: Vertical(g4)
    c: Radius(g0) = 1.5
    c: PointOnObject(g5,g4)
    c: PointOnObject(g5,g2)
    c: PointOnObject(g6,g1)
    c: PointOnObject(g6,g3)
    c: Symmetric(g1,g2,g5)
    c: Symmetric(g1,g1,g6)
    c: PointOnObject(g0,g6)
    c: PointOnObject(g0,g5)
    c: Equal(g1,g2)
    c: DistanceX(g1,g1) = 6
    c: DistanceX(g0,g-1) = 36.77
FEATURE [Sketcher::SketchObject] Sketch090  label="hb pcb support left low"
  AttachmentOffset = pos=(0,0,9) rot=(0,0,1;0rad)
  FullyConstrained = false
  MapMode = 5
  Placement = pos=(0,-9,-2e-15) rot=(1,0,0;1.5708rad)
  Support = -> [XZ_Plane013]
  sketch-geometry (7):
    g0: Circle CenterX=-36.77 CenterY=18.45 CenterZ=0 NormalX=0 NormalY=0 NormalZ=1 AngleXU=0 Radius=1.5
    g1: LineSegment StartX=-40.77 StartY=22.45 StartZ=0 EndX=-32.77 EndY=22.45 EndZ=0
    g2: LineSegment StartX=-32.77 StartY=22.45 StartZ=0 EndX=-32.77 EndY=14.45 EndZ=0
    g3: LineSegment StartX=-32.77 StartY=14.45 StartZ=0 EndX=-40.77 EndY=14.45 EndZ=0
    g4: LineSegment StartX=-40.77 StartY=14.45 StartZ=0 EndX=-40.77 EndY=22.45 EndZ=0
    g5: LineSegment StartX=-40.77 StartY=18.45 StartZ=0 EndX=-32.77 EndY=18.45 EndZ=0
    g6: LineSegment StartX=-36.77 StartY=22.45 StartZ=0 EndX=-36.77 EndY=14.45 EndZ=0
  constraints (21):
    c: DistanceY(g0) = 18.45
    c: Coincident(g1,g2)
    c: Coincident(g2,g3)
    c: Coincident(g3,g4)
    c: Coincident(g4,g1)
    c: Horizontal(g1)
    c: Horizontal(g3)
    c: Vertical(g2)
    c: Vertical(g4)
    c: Radius(g0) = 1.5
    c: PointOnObject(g5,g4)
    c: PointOnObject(g5,g2)
    c: PointOnObject(g6,g1)
    c: PointOnObject(g6,g3)
    c: Symmetric(g1,g2,g5)
    c: Symmetric(g1,g1,g6)
    c: PointOnObject(g0,g6)
    c: PointOnObject(g0,g5)
    c: Equal(g1,g2)
    c: DistanceX(g1,g1) = 8
    c: DistanceX(g0,g-1) = 36.77
FEATURE [Sketcher::SketchObject] Sketch091  label="hb pcb alignment pin"
  AttachmentOffset = pos=(0,0,18.45) rot=(0,0,1;0rad)
  FullyConstrained = false
  MapMode = 5
  Placement = pos=(0,0,18.45) rot=(0,0,1;0rad)
  Support = -> [XY_Plane013]
  sketch-geometry (6):
    g0: LineSegment StartX=-36.77 StartY=-14.5 StartZ=0 EndX=-38.07 EndY=-14.5 EndZ=0
    g1: LineSegment StartX=-38.07 StartY=-14.5 StartZ=0 EndX=-38.07 EndY=-15.7 EndZ=0
    g2: LineSegment StartX=-37.67 StartY=-17 StartZ=0 EndX=-36.77 EndY=-17 EndZ=0
    g3: LineSegment StartX=-36.77 StartY=-17 StartZ=0 EndX=-36.77 EndY=-14.5 EndZ=0
    g4: LineSegment StartX=-36.77 StartY=-14.5 StartZ=0 EndX=-36.77 EndY=0 EndZ=0
    g5: ArcOfCircle CenterX=-35.7575 CenterY=-15.7 CenterZ=0 NormalX=0 NormalY=0 NormalZ=1 AngleXU=0 Radius=2.3125 StartAngle=3.14159 EndAngle=3.73859
  constraints (18):
    c: Horizontal(g0)
    c: Coincident(g0,g1)
    c: Vertical(g1)
    c: Horizontal(g2)
    c: Coincident(g2,g3)
    c: Coincident(g3,g0)
    c: Vertical(g3)
    c: Coincident(g4,g0)
    c: PointOnObject(g4,g-1)
    c: Vertical(g4)
    c: DistanceX(g4,g-1) = 36.77
    c: DistanceY(g0,g-1) = 14.5
    c: DistanceX(g0,g0) = 1.3
    c: DistanceY(g1,g1) = 1.2
    c: DistanceY(g2,g-1) = 17
    c: Coincident(g5,g2)
    c: Tangent(g1,g5) = -1.5708
    c: DistanceX(g2,g2) = 0.9
FEATURE [Sketcher::SketchObject] Sketch094
  FullyConstrained = false
  MapMode = 5
  Placement = pos=(0,0,0) rot=(1,0,0;1.5708rad)
  Support = -> [XZ_Plane017]
  sketch-geometry (5):
    g0: LineSegment StartX=0 StartY=0 StartZ=0 EndX=0 EndY=-12 EndZ=0
    g1: LineSegment StartX=0 StartY=-12 StartZ=0 EndX=1.5 EndY=-1.25 EndZ=0
    g2: LineSegment StartX=1.5 StartY=-1.25 StartZ=0 EndX=2.65 EndY=-0.1 EndZ=0
    g3: LineSegment StartX=2.65 StartY=0 StartZ=0 EndX=0 EndY=0 EndZ=0
    g4: LineSegment StartX=2.65 StartY=-0.1 StartZ=0 EndX=2.65 EndY=0 EndZ=0
  constraints (14):
    c: Coincident(g-1,g0)
    c: Vertical(g0)
    c: Coincident(g0,g1)
    c: Coincident(g1,g2)
    c: Coincident(g3,g0)
    c: DistanceY(g0,g0) = 12
    c: Angle(g3,g2) = 0.785398
    c: DistanceX(g0,g1) = 1.5
    c: Horizontal(g3)
    c: Coincident(g4,g2)
    c: Vertical(g4)
    c: Coincident(g3,g4)
    c: DistanceX(g3) = 2.65
    c: DistanceY(g4,g4) = 0.1
FEATURE [PartDesign::Revolution] Revolution005
  AllowMultiFace = false
  Angle = 360
  Axis = (-3e-16,3e-16,1)
  Base = (0,0,0)
  Placement = pos=(0,0,0) rot=(1,0,0;1.5708rad)
  Profile = -> Sketch094
  ReferenceAxis = -> Z_Axis019
  Reversed = true
FEATURE [Sketcher::SketchObject] Sketch095  label="Sketch001"
  FullyConstrained = false
  MapMode = 5
  Placement = pos=(0,0,0) rot=(1,0,0;1.5708rad)
  Support = -> [XZ_Plane017]
  sketch-geometry (3):
    g0: LineSegment StartX=-2 StartY=0 StartZ=0 EndX=0 EndY=-2 EndZ=0
    g1: LineSegment StartX=0 StartY=-2 StartZ=0 EndX=2 EndY=0 EndZ=0
    g2: LineSegment StartX=2 StartY=0 StartZ=0 EndX=-2 EndY=0 EndZ=0
  constraints (9):
    c: PointOnObject(g0,g-1)
    c: Coincident(g0,g1)
    c: PointOnObject(g1,g-1)
    c: Coincident(g1,g2)
    c: Coincident(g2,g0)
    c: PointOnObject(g0,g-2)
    c: Equal(g1,g0)
    c: Perpendicular(g0,g1)
    c: DistanceX(g2,g2) = 4
FEATURE [PartDesign::Pocket] Pocket020  label="Pocket"
  AllowMultiFace = false
  BaseFeature = -> Revolution005
  Length = 0.6
  Length2 = 100
  Midplane = true
  Placement = pos=(0,0,0) rot=(1,0,0;1.5708rad)
  Profile = -> Sketch095
  Type = 0
FEATURE [PartDesign::PolarPattern] PolarPattern002  label="PolarPattern"
  Angle = 90
  Axis = -> Z_Axis019
  BaseFeature = -> Pocket020
  Occurrences = 2
  Originals = -> [Pocket020]
  Placement = pos=(0,0,0) rot=(1,0,0;1.5708rad)
FEATURE [PartDesign::Body] Body017  label="SelftappingScrew3.0x12_01"
  Group = -> [Sketch094,Revolution005,Sketch095,Pocket020,PolarPattern002]
  Origin = -> Origin017
  Placement = pos=(40,-5.8,30) rot=(-1,0,0;1.5708rad)
  Tip = -> PolarPattern002
FEATURE [Sketcher::SketchObject] Sketch096
  FullyConstrained = false
  MapMode = 5
  Placement = pos=(0,0,0) rot=(1,0,0;1.5708rad)
  Support = -> [XZ_Plane018]
  sketch-geometry (3):
    g0: LineSegment StartX=-2 StartY=0 StartZ=0 EndX=0 EndY=-2 EndZ=0
    g1: LineSegment StartX=0 StartY=-2 StartZ=0 EndX=2 EndY=0 EndZ=0
    g2: LineSegment StartX=2 StartY=0 StartZ=0 EndX=-2 EndY=0 EndZ=0
  constraints (9):
    c: PointOnObject(g0,g-1)
    c: Coincident(g0,g1)
    c: PointOnObject(g1,g-1)
    c: Coincident(g1,g2)
    c: Coincident(g2,g0)
    c: PointOnObject(g0,g-2)
    c: Equal(g1,g0)
    c: Perpendicular(g0,g1)
    c: DistanceX(g2,g2) = 4
FEATURE [Sketcher::SketchObject] Sketch097
  FullyConstrained = false
  MapMode = 5
  Placement = pos=(0,0,0) rot=(1,0,0;1.5708rad)
  Support = -> [XZ_Plane018]
  sketch-geometry (5):
    g0: LineSegment StartX=0 StartY=0 StartZ=0 EndX=0 EndY=-12 EndZ=0
    g1: LineSegment StartX=0 StartY=-12 StartZ=0 EndX=1.5 EndY=-1.25 EndZ=0
    g2: LineSegment StartX=1.5 StartY=-1.25 StartZ=0 EndX=2.65 EndY=-0.1 EndZ=0
    g3: LineSegment StartX=2.65 StartY=0 StartZ=0 EndX=0 EndY=0 EndZ=0
    g4: LineSegment StartX=2.65 StartY=-0.1 StartZ=0 EndX=2.65 EndY=0 EndZ=0
  constraints (14):
    c: Coincident(g-1,g0)
    c: Vertical(g0)
    c: Coincident(g0,g1)
    c: Coincident(g1,g2)
    c: Coincident(g3,g0)
    c: DistanceY(g0,g0) = 12
    c: Angle(g3,g2) = 0.785398
    c: DistanceX(g0,g1) = 1.5
    c: Horizontal(g3)
    c: Coincident(g4,g2)
    c: Vertical(g4)
    c: Coincident(g3,g4)
    c: DistanceX(g3) = 2.65
    c: DistanceY(g4,g4) = 0.1
FEATURE [PartDesign::Revolution] Revolution006
  AllowMultiFace = false
  Angle = 360
  Axis = (-3e-16,3e-16,1)
  Base = (0,0,0)
  Placement = pos=(0,0,0) rot=(1,0,0;1.5708rad)
  Profile = -> Sketch097
  ReferenceAxis = -> Z_Axis014
  Reversed = true
FEATURE [PartDesign::Pocket] Pocket021
  AllowMultiFace = false
  BaseFeature = -> Revolution006
  Length = 0.6
  Length2 = 100
  Midplane = true
  Placement = pos=(0,0,0) rot=(1,0,0;1.5708rad)
  Profile = -> Sketch096
  Type = 0
FEATURE [PartDesign::PolarPattern] PolarPattern003
  Angle = 90
  Axis = -> Z_Axis020
  BaseFeature = -> Pocket021
  Occurrences = 2
  Originals = -> [Pocket021]
  Placement = pos=(0,0,0) rot=(1,0,0;1.5708rad)
FEATURE [PartDesign::Body] Body018  label="SelftappingScrew3.0x12_02"
  Group = -> [Sketch097,Revolution006,Sketch096,Pocket021,PolarPattern003]
  Origin = -> Origin018
  Placement = pos=(-40,-5.8,30) rot=(-1,0,0;1.5708rad)
  Tip = -> PolarPattern003
FEATURE [Sketcher::SketchObject] Sketch098
  FullyConstrained = false
  MapMode = 5
  Placement = pos=(0,0,0) rot=(1,0,0;1.5708rad)
  Support = -> [XZ_Plane019]
  sketch-geometry (3):
    g0: LineSegment StartX=-2 StartY=0 StartZ=0 EndX=0 EndY=-2 EndZ=0
    g1: LineSegment StartX=0 StartY=-2 StartZ=0 EndX=2 EndY=0 EndZ=0
    g2: LineSegment StartX=2 StartY=0 StartZ=0 EndX=-2 EndY=0 EndZ=0
  constraints (9):
    c: PointOnObject(g0,g-1)
    c: Coincident(g0,g1)
    c: PointOnObject(g1,g-1)
    c: Coincident(g1,g2)
    c: Coincident(g2,g0)
    c: PointOnObject(g0,g-2)
    c: Equal(g1,g0)
    c: Perpendicular(g0,g1)
    c: DistanceX(g2,g2) = 4
FEATURE [Sketcher::SketchObject] Sketch099
  FullyConstrained = false
  MapMode = 5
  Placement = pos=(0,0,0) rot=(1,0,0;1.5708rad)
  Support = -> [XZ_Plane019]
  sketch-geometry (5):
    g0: LineSegment StartX=0 StartY=0 StartZ=0 EndX=0 EndY=-12 EndZ=0
    g1: LineSegment StartX=0 StartY=-12 StartZ=0 EndX=1.5 EndY=-1.25 EndZ=0
    g2: LineSegment StartX=1.5 StartY=-1.25 StartZ=0 EndX=2.65 EndY=-0.1 EndZ=0
    g3: LineSegment StartX=2.65 StartY=0 StartZ=0 EndX=0 EndY=0 EndZ=0
    g4: LineSegment StartX=2.65 StartY=-0.1 StartZ=0 EndX=2.65 EndY=0 EndZ=0
  constraints (14):
    c: Coincident(g-1,g0)
    c: Vertical(g0)
    c: Coincident(g0,g1)
    c: Coincident(g1,g2)
    c: Coincident(g3,g0)
    c: DistanceY(g0,g0) = 12
    c: Angle(g3,g2) = 0.785398
    c: DistanceX(g0,g1) = 1.5
    c: Horizontal(g3)
    c: Coincident(g4,g2)
    c: Vertical(g4)
    c: Coincident(g3,g4)
    c: DistanceX(g3) = 2.65
    c: DistanceY(g4,g4) = 0.1
FEATURE [PartDesign::Revolution] Revolution007
  AllowMultiFace = false
  Angle = 360
  Axis = (-3e-16,3e-16,1)
  Base = (0,0,0)
  Placement = pos=(0,0,0) rot=(1,0,0;1.5708rad)
  Profile = -> Sketch099
  ReferenceAxis = -> Z_Axis014
  Reversed = true
FEATURE [PartDesign::Pocket] Pocket022
  AllowMultiFace = false
  BaseFeature = -> Revolution007
  Length = 0.6
  Length2 = 100
  Midplane = true
  Placement = pos=(0,0,0) rot=(1,0,0;1.5708rad)
  Profile = -> Sketch098
  Type = 0
FEATURE [PartDesign::PolarPattern] PolarPattern004
  Angle = 90
  Axis = -> Z_Axis022
  BaseFeature = -> Pocket022
  Occurrences = 2
  Originals = -> [Pocket022]
  Placement = pos=(0,0,0) rot=(1,0,0;1.5708rad)
FEATURE [PartDesign::Body] Body019  label="SelftappingScrew3.0x12_03"
  Group = -> [Sketch099,Revolution007,Sketch098,Pocket022,PolarPattern004]
  Origin = -> Origin019
  Placement = pos=(40,-5.8,-30) rot=(-1,0,0;1.5708rad)
  Tip = -> PolarPattern004
FEATURE [Sketcher::SketchObject] Sketch100
  FullyConstrained = false
  MapMode = 5
  Placement = pos=(0,0,0) rot=(1,0,0;1.5708rad)
  Support = -> [XZ_Plane020]
  sketch-geometry (3):
    g0: LineSegment StartX=-2 StartY=0 StartZ=0 EndX=0 EndY=-2 EndZ=0
    g1: LineSegment StartX=0 StartY=-2 StartZ=0 EndX=2 EndY=0 EndZ=0
    g2: LineSegment StartX=2 StartY=0 StartZ=0 EndX=-2 EndY=0 EndZ=0
  constraints (9):
    c: PointOnObject(g0,g-1)
    c: Coincident(g0,g1)
    c: PointOnObject(g1,g-1)
    c: Coincident(g1,g2)
    c: Coincident(g2,g0)
    c: PointOnObject(g0,g-2)
    c: Equal(g1,g0)
    c: Perpendicular(g0,g1)
    c: DistanceX(g2,g2) = 4
FEATURE [Sketcher::SketchObject] Sketch101
  FullyConstrained = false
  MapMode = 5
  Placement = pos=(0,0,0) rot=(1,0,0;1.5708rad)
  Support = -> [XZ_Plane020]
  sketch-geometry (5):
    g0: LineSegment StartX=0 StartY=0 StartZ=0 EndX=0 EndY=-12 EndZ=0
    g1: LineSegment StartX=0 StartY=-12 StartZ=0 EndX=1.5 EndY=-1.25 EndZ=0
    g2: LineSegment StartX=1.5 StartY=-1.25 StartZ=0 EndX=2.65 EndY=-0.1 EndZ=0
    g3: LineSegment StartX=2.65 StartY=0 StartZ=0 EndX=0 EndY=0 EndZ=0
    g4: LineSegment StartX=2.65 StartY=-0.1 StartZ=0 EndX=2.65 EndY=0 EndZ=0
  constraints (14):
    c: Coincident(g-1,g0)
    c: Vertical(g0)
    c: Coincident(g0,g1)
    c: Coincident(g1,g2)
    c: Coincident(g3,g0)
    c: DistanceY(g0,g0) = 12
    c: Angle(g3,g2) = 0.785398
    c: DistanceX(g0,g1) = 1.5
    c: Horizontal(g3)
    c: Coincident(g4,g2)
    c: Vertical(g4)
    c: Coincident(g3,g4)
    c: DistanceX(g3) = 2.65
    c: DistanceY(g4,g4) = 0.1
FEATURE [PartDesign::Revolution] Revolution008
  AllowMultiFace = false
  Angle = 360
  Axis = (-3e-16,3e-16,1)
  Base = (0,0,0)
  Placement = pos=(0,0,0) rot=(1,0,0;1.5708rad)
  Profile = -> Sketch101
  ReferenceAxis = -> Z_Axis014
  Reversed = true
FEATURE [PartDesign::Pocket] Pocket023
  AllowMultiFace = false
  BaseFeature = -> Revolution008
  Length = 0.6
  Length2 = 100
  Midplane = true
  Placement = pos=(0,0,0) rot=(1,0,0;1.5708rad)
  Profile = -> Sketch100
  Type = 0
FEATURE [PartDesign::PolarPattern] PolarPattern005
  Angle = 90
  Axis = -> Z_Axis024
  BaseFeature = -> Pocket023
  Occurrences = 2
  Originals = -> [Pocket023]
  Placement = pos=(0,0,0) rot=(1,0,0;1.5708rad)
FEATURE [PartDesign::Body] Body020  label="SelftappingScrew3.0x12_04"
  Group = -> [Sketch101,Revolution008,Sketch100,Pocket023,PolarPattern005]
  Origin = -> Origin020
  Placement = pos=(-40,-5.8,-30) rot=(-1,0,0;1.5708rad)
  Tip = -> PolarPattern005
FEATURE [Sketcher::SketchObject] Sketch102  label="hb screwhole bottom top"
  AttachmentOffset = pos=(0,0,30) rot=(0,0,1;0rad)
  FullyConstrained = false
  MapMode = 5
  Placement = pos=(0,0,30) rot=(0,0,1;0rad)
  Support = -> [XY_Plane013]
  sketch-geometry (7):
    g0: LineSegment StartX=40 StartY=-3 StartZ=0 EndX=40 EndY=-18.3 EndZ=0
    g1: LineSegment StartX=40.5 StartY=-18.3 StartZ=0 EndX=41.65 EndY=-6.95 EndZ=0
    g2: LineSegment StartX=41.65 StartY=-6.95 StartZ=0 EndX=42.8 EndY=-5.8 EndZ=0
    g3: LineSegment StartX=42.8 StartY=-5.8 StartZ=0 EndX=42.8 EndY=-3 EndZ=0
    g4: LineSegment StartX=42.8 StartY=-3 StartZ=0 EndX=40 EndY=-3 EndZ=0
    g5: LineSegment StartX=40 StartY=-3 StartZ=0 EndX=40 EndY=-0.2 EndZ=0
    g6: LineSegment StartX=40.5 StartY=-18.3 StartZ=0 EndX=40 EndY=-18.3 EndZ=0
  constraints (21):
    c: Vertical(g0)
    c: Coincident(g1,g2)
    c: Coincident(g2,g3)
    c: Vertical(g3)
    c: Coincident(g3,g4)
    c: Coincident(g4,g0)
    c: Horizontal(g4)
    c: Coincident(g5,g0)
    c: Vertical(g5)
    c: DistanceX(g5) = 40
    c: DistanceY(g0,g-1) = 3
    c: DistanceX(g4,g4) = 2.8
    c: Equal(g4,g5)
    c: DistanceY(g2,g-1) = 5.8
    c: Angle(g0,g2) = 2.35619
    c: Horizontal(g6)
    c: Coincident(g1,g6)
    c: Coincident(g6,g0)
    c: DistanceX(g6,g6) = 0.5
    c: DistanceY(g1,g2) = 12.5
    c: DistanceX(g0,g1) = 1.65
FEATURE [PartDesign::Mirrored] Mirrored006
  MirrorPlane = -> XY_Plane013
FEATURE [PartDesign::Mirrored] Mirrored007
  MirrorPlane = -> YZ_Plane013
FEATURE [Sketcher::SketchObject] Sketch103  label="ht screwhole bottom top"
  AttachmentOffset = pos=(0,0,30) rot=(0,0,1;0rad)
  FullyConstrained = false
  MapMode = 5
  Placement = pos=(0,0,30) rot=(0,0,1;0rad)
  Support = -> [XY_Plane014]
  sketch-geometry (7):
    g0: LineSegment StartX=40 StartY=-3 StartZ=0 EndX=40 EndY=-18.3 EndZ=0
    g1: LineSegment StartX=40.2 StartY=-18.3 StartZ=0 EndX=41.65 EndY=-6.95 EndZ=0
    g2: LineSegment StartX=41.65 StartY=-6.95 StartZ=0 EndX=42.8 EndY=-5.8 EndZ=0
    g3: LineSegment StartX=42.8 StartY=-5.8 StartZ=0 EndX=42.8 EndY=-3 EndZ=0
    g4: LineSegment StartX=42.8 StartY=-3 StartZ=0 EndX=40 EndY=-3 EndZ=0
    g5: LineSegment StartX=40 StartY=-3 StartZ=0 EndX=40 EndY=-0.2 EndZ=0
    g6: LineSegment StartX=40.2 StartY=-18.3 StartZ=0 EndX=40 EndY=-18.3 EndZ=0
  constraints (21):
    c: Vertical(g0)
    c: Coincident(g1,g2)
    c: Coincident(g2,g3)
    c: Vertical(g3)
    c: Coincident(g3,g4)
    c: Coincident(g4,g0)
    c: Horizontal(g4)
    c: Coincident(g5,g0)
    c: Vertical(g5)
    c: DistanceX(g5) = 40
    c: DistanceY(g0,g-1) = 3
    c: DistanceX(g4,g4) = 2.8
    c: Equal(g4,g5)
    c: DistanceY(g2,g-1) = 5.8
    c: Angle(g0,g2) = 2.35619
    c: Horizontal(g6)
    c: Coincident(g1,g6)
    c: Coincident(g6,g0)
    c: DistanceX(g6,g6) = 0.2
    c: DistanceY(g1,g2) = 12.5
    c: DistanceX(g0,g1) = 1.65
FEATURE [PartDesign::Mirrored] Mirrored008
  MirrorPlane = -> XY_Plane014
FEATURE [PartDesign::Mirrored] Mirrored009
  MirrorPlane = -> YZ_Plane014
FEATURE [PartDesign::Mirrored] Mirrored010
  MirrorPlane = -> XY_Plane013
FEATURE [PartDesign::Mirrored] Mirrored011
  MirrorPlane = -> YZ_Plane013
FEATURE [PartDesign::Mirrored] Mirrored012
  MirrorPlane = -> XY_Plane007
FEATURE [PartDesign::Mirrored] Mirrored013
  MirrorPlane = -> YZ_Plane007
FEATURE [PartDesign::MultiTransform] MultiTransform003  label="WP Magnet hole 2,3,4"
  BaseFeature = -> Groove001
  Originals = -> [Groove001]
  Transformations = -> [Mirrored012,Mirrored013]
FEATURE [PartDesign::Body] Body007  label="WallPlate"
  Group = -> [Sketch026,Pad009,Pocket003,SubtractivePipe001,Sketch022,Sketch023,Sketch027,Sketch035,Pocket006,AdditivePipe001,AdditivePipe002,Sketch036,AdditivePipe,Sketch040,Sketch041,Sketch068,Pocket013,Mirrored001,Sketch084,Groove001,MultiTransform003,Mirrored012,Mirrored013]
  Origin = -> Origin007
  Tip = -> MultiTransform003
FEATURE [PartDesign::Fillet] Fillet  label="HT Fillet around"
  Base = -> SubtractivePipe006 [Edge7]
  BaseFeature = -> SubtractivePipe006
  Radius = 6
  SupportTransform = false
FEATURE [PartDesign::Fillet] Fillet001  label="HB Fillet around"
  Base = -> SubtractivePipe003 [Edge7]
  BaseFeature = -> SubtractivePipe003
  Radius = 6
  SupportTransform = false
FEATURE [PartDesign::Plane] DatumPlane001  label="HT ButtonPlane"
  AttachmentOffset = pos=(0,0,41) rot=(0,0,1;0rad)
  Length = 63.3489
  MapMode = 5
  Placement = pos=(41,-9.1e-15,9.1e-15) rot=(0.57735,0.57735,0.57735;2.0944rad)
  ResizeMode = 0
  Support = -> [YZ_Plane014]
  Width = 102.445
FEATURE [Sketcher::SketchObject] Sketch075  label="hp cutout button low"
  AttachmentOffset = pos=(0,0,20) rot=(0,0,1;0rad)
  ExternalGeometry = -> [DatumPlane001]
  FullyConstrained = false
  MapMode = 5
  Placement = pos=(0,-20,-4.4e-15) rot=(1,0,0;1.5708rad)
  Support = -> [XZ_Plane014]
  sketch-geometry (4):
    g0: ArcOfCircle CenterX=41 CenterY=-14 CenterZ=0 NormalX=0 NormalY=0 NormalZ=1 AngleXU=0 Radius=5.2 StartAngle=1.5708 EndAngle=4.71239
    g1: LineSegment StartX=41 StartY=-19.2 StartZ=0 EndX=75 EndY=-19.2 EndZ=0
    g2: LineSegment StartX=41 StartY=-8.8 StartZ=0 EndX=75 EndY=-8.8 EndZ=0
    g3: LineSegment StartX=75 StartY=-8.8 StartZ=0 EndX=75 EndY=-19.2 EndZ=0
  constraints (11):
    c: Tangent(g0,g2)
    c: Tangent(g0,g1)
    c: Horizontal(g1)
    c: DistanceY(g0,g-1) = 14
    c: Radius(g0) = 5.2
    c: Coincident(g3,g2)
    c: Coincident(g3,g1)
    c: Vertical(g3)
    c: DistanceX(g2) = 75
    c: Horizontal(g2)
    c: PointOnObject(g0,g-3)
FEATURE [Sketcher::SketchObject] Sketch076  label="hp cutout button high"
  AttachmentOffset = pos=(0,0,22) rot=(0,0,1;0rad)
  ExternalGeometry = -> [DatumPlane001]
  FullyConstrained = false
  MapMode = 5
  Placement = pos=(0,-22,-4.9e-15) rot=(1,0,0;1.5708rad)
  Support = -> [XZ_Plane014]
  sketch-geometry (5):
    g0: ArcOfCircle CenterX=41 CenterY=-14 CenterZ=0 NormalX=0 NormalY=0 NormalZ=1 AngleXU=0 Radius=6.4 StartAngle=1.7017 EndAngle=4.58149
    g1: LineSegment StartX=40.1646 StartY=-20.3452 StartZ=0 EndX=75 EndY=-24.9314 EndZ=0
    g2: LineSegment StartX=40.1646 StartY=-7.65475 StartZ=0 EndX=75 EndY=-3.06859 EndZ=0
    g3: LineSegment StartX=75 StartY=-3.06859 StartZ=0 EndX=75 EndY=-24.9314 EndZ=0
    g4: LineSegment StartX=41 StartY=-14 StartZ=0 EndX=75 EndY=-14 EndZ=0
  constraints (13):
    c: Tangent(g0,g2)
    c: Tangent(g0,g1)
    c: DistanceY(g0,g-1) = 14
    c: Radius(g0) = 6.4
    c: Coincident(g3,g2)
    c: Coincident(g3,g1)
    c: Vertical(g3)
    c: DistanceX(g2) = 75
    c: Coincident(g4,g0)
    c: PointOnObject(g4,g3)
    c: Symmetric(g1,g2,g4)
    c: Angle(g1,g2) = 0.261799
    c: PointOnObject(g0,g-3)
FEATURE [PartDesign::SubtractiveLoft] SubtractiveLoft001  label="HT Cutout button 1"
  BaseFeature = -> Fillet
  Closed = false
  Profile = -> Sketch075
  Ruled = false
  Sections = -> [Sketch076]
FEATURE [Sketcher::SketchObject] Sketch110  label="hb pillar adaptor 1"
  AttachmentOffset = pos=(0,0,-33.1) rot=(0,0,1;0rad)
  FullyConstrained = false
  MapMode = 5
  Placement = pos=(0,0,-33.1) rot=(0,0,1;0rad)
  Support = -> [XY_Plane013]
  sketch-geometry (8):
    g0: LineSegment StartX=-24.8 StartY=-4.5 StartZ=0 EndX=-24.8 EndY=-13 EndZ=0
    g1: LineSegment StartX=-24.8 StartY=-13 StartZ=0 EndX=-24.2 EndY=-13 EndZ=0
    g2: LineSegment StartX=-23.3 StartY=-10.5 StartZ=0 EndX=-22.7 EndY=-10.5 EndZ=0
    g3: LineSegment StartX=-22.7 StartY=-10.5 StartZ=0 EndX=-22.7 EndY=-4.5 EndZ=0
    g4: LineSegment StartX=-22.7 StartY=-4.5 StartZ=0 EndX=-24.8 EndY=-4.5 EndZ=0
    g5: LineSegment StartX=-24.8 StartY=-13 StartZ=0 EndX=-24.8 EndY=-20.8062 EndZ=0
    g6: ArcOfCircle CenterX=-30.9876 CenterY=-9.14447 CenterZ=0 NormalX=0 NormalY=0 NormalZ=1 AngleXU=0 Radius=7.80617 StartAngle=5.76661 EndAngle=6.10865
    g7: LineSegment StartX=-30.9876 StartY=-9.14447 StartZ=0 EndX=-23.3 EndY=-10.5 EndZ=0
  constraints (24):
    c: Vertical(g0)
    c: Coincident(g0,g1)
    c: Horizontal(g2)
    c: Coincident(g2,g3)
    c: Vertical(g3)
    c: Coincident(g3,g4)
    c: Coincident(g4,g0)
    c: DistanceY(g0,g-1) = 4.5
    c: Horizontal(g4)
    c: DistanceX(g0,g2) = 1.5
    c: Horizontal(g1)
    c: DistanceY(g2,g-1) = 10.5
    c: DistanceY(g1,g2) = 2.5
    c: Coincident(g5,g0)
    c: Vertical(g5)
    c: DistanceX(g0,g-1) = 24.8
    c: DistanceX(g2,g2) = 0.6
    c: Coincident(g6,g2)
    c: Coincident(g6,g1)
    c: Coincident(g7,g6)
    c: Coincident(g7,g2)
    c: Angle(g2,g7) = 2.96706
    c: DistanceX(g1,g1) = 0.6
    c: Equal(g5,g7)
FEATURE [Sketcher::SketchObject] Sketch111
  FullyConstrained = false
  MapMode = 5
  Support = -> [XY_Plane027]
  sketch-geometry (13):
    g0: LineSegment StartX=9.8 StartY=17.1 StartZ=0 EndX=-9.8 EndY=17.1 EndZ=0
    g1: LineSegment StartX=-12.8 StartY=14.1 StartZ=0 EndX=-12.8 EndY=-17.1 EndZ=0
    g2: LineSegment StartX=-12.8 StartY=-17.1 StartZ=0 EndX=12.8 EndY=-17.1 EndZ=0
    g3: LineSegment StartX=12.8 StartY=-17.1 StartZ=0 EndX=12.8 EndY=14.1 EndZ=0
    g4: GeomPoint X=12.8 Y=17.1 Z=0
    g5: ArcOfCircle CenterX=9.8 CenterY=14.1 CenterZ=0 NormalX=0 NormalY=0 NormalZ=1 AngleXU=0 Radius=3 StartAngle=0 EndAngle=1.5708
    g6: ArcOfCircle CenterX=-9.8 CenterY=14.1 CenterZ=0 NormalX=0 NormalY=0 NormalZ=1 AngleXU=0 Radius=3 StartAngle=1.5708 EndAngle=3.14159
    g7: Circle CenterX=-9.8 CenterY=14.1 CenterZ=0 NormalX=0 NormalY=0 NormalZ=1 AngleXU=0 Radius=1.6
    g8: Circle CenterX=9.8 CenterY=-14.1 CenterZ=0 NormalX=0 NormalY=0 NormalZ=1 AngleXU=0 Radius=1.6
    g9: LineSegment StartX=-9.8 StartY=14.1 StartZ=0 EndX=9.8 EndY=14.1 EndZ=0
    g10: LineSegment StartX=9.8 StartY=14.1 StartZ=0 EndX=9.8 EndY=-14.1 EndZ=0
    g11: LineSegment StartX=9.8 StartY=-14.1 StartZ=0 EndX=-9.8 EndY=-14.1 EndZ=0
    g12: LineSegment StartX=-9.8 StartY=-14.1 StartZ=0 EndX=-9.8 EndY=14.1 EndZ=0
  constraints (28):
    c: Vertical(g1)
    c: Symmetric(g1,g3,g-2)
    c: PointOnObject(g4,g0)
    c: Symmetric(g4,g2,g-1)
    c: Symmetric(g2,g2,g-2)
    c: Tangent(g3,g5) = -1.5708
    c: Tangent(g0,g5) = -1.5708
    c: Tangent(g0,g6) = -1.5708
    c: Tangent(g1,g6) = -1.5708
    c: Symmetric(g5,g6,g-2)
    c: Coincident(g1,g2)
    c: DistanceY(g2,g0) = 34.2
    c: Vertical(g3)
    c: DistanceX(g1,g3) = 25.6
    c: Radius(g5) = 3
    c: Coincident(g7,g6)
    c: Diameter(g7) = 3.2
    c: Coincident(g9,g10)
    c: Coincident(g10,g11)
    c: Coincident(g11,g12)
    c: Coincident(g12,g9)
    c: Horizontal(g11)
    c: Vertical(g12)
    c: Coincident(g9,g6)
    c: Coincident(g10,g8)
    c: Symmetric(g6,g9,g-2)
    c: Symmetric(g5,g8,g-1)
    c: Equal(g8,g7)
FEATURE [PartDesign::Pad] Pad019
  Direction = (1,1,1)
  Length = 1
  Length2 = 100
  Profile = -> Sketch111
  Reversed = true
  Type = 0
FEATURE [Part::Feature] Part__Feature003  label="Phonix2Pins001"
  Placement = pos=(2.53914,22.8011,-15.51) rot=(0.57735,0.57735,0.57735;2.0944rad)
  shape: bbox 10.73 x 8.1 x 13.5 mm, 169 faces (baked)
FEATURE [Sketcher::SketchObject] Sketch112
  FullyConstrained = false
  MapMode = 5
  Placement = pos=(0,0,0) rot=(0.57735,0.57735,0.57735;2.0944rad)
  Support = -> [YZ_Plane028]
  sketch-geometry (4):
    g0: LineSegment StartX=-2.25 StartY=3.6 StartZ=0 EndX=2.25 EndY=3.6 EndZ=0
    g1: LineSegment StartX=2.25 StartY=3.6 StartZ=0 EndX=2.25 EndY=0 EndZ=0
    g2: LineSegment StartX=2.25 StartY=0 StartZ=0 EndX=-2.25 EndY=0 EndZ=0
    g3: LineSegment StartX=-2.25 StartY=0 StartZ=0 EndX=-2.25 EndY=3.6 EndZ=0
  constraints (11):
    c: Coincident(g0,g1)
    c: Coincident(g1,g2)
    c: Coincident(g2,g3)
    c: Coincident(g3,g0)
    c: Horizontal(g2)
    c: Vertical(g1)
    c: Vertical(g3)
    c: DistanceX(g0,g0) = 4.5
    c: DistanceY(g1,g1) = 3.6
    c: PointOnObject(g1,g-1)
    c: Symmetric(g0,g0,g-2)
FEATURE [PartDesign::Pad] Pad020
  Direction = (1,1,1)
  Length = 6.3
  Length2 = 100
  Midplane = true
  Placement = pos=(0,0,0) rot=(0.57735,0.57735,0.57735;2.0944rad)
  Profile = -> Sketch112
  Type = 0
FEATURE [PartDesign::Body] Body028  label="BodyDevice003"
  Group = -> [Sketch112,Pad020]
  Origin = -> Origin028
  Placement = pos=(0,-2.35,0) rot=(0,0,1;0rad)
  Tip = -> Pad020
FEATURE [Sketcher::SketchObject] Sketch113
  AttachmentOffset = pos=(0,0,4) rot=(0,0,1;0rad)
  FullyConstrained = false
  MapMode = 5
  Placement = pos=(0,0,4) rot=(0,0,1;0rad)
  Support = -> [XY_Plane030]
  sketch-geometry (2):
    g0: ArcOfCircle CenterX=0 CenterY=0 CenterZ=0 NormalX=0 NormalY=0 NormalZ=1 AngleXU=0 Radius=2.3 StartAngle=0.9701 EndAngle=5.31309
    g1: LineSegment StartX=1.3 StartY=1.89737 StartZ=0 EndX=1.3 EndY=-1.89737 EndZ=0
  constraints (6):
    c: Coincident(g1,g0)
    c: Coincident(g1,g0)
    c: Coincident(g0,g-1)
    c: DistanceX(g0,g0) = 1.3
    c: Diameter(g0) = 4.6
    c: Vertical(g1)
FEATURE [PartDesign::Pad] Pad021
  Direction = (1,1,1)
  Length = 4.7
  Length2 = 100
  Profile = -> Sketch113
  Type = 0
FEATURE [PartDesign::Body] Body030  label="DallasSensor001"
  Group = -> [Sketch113,Pad021]
  Origin = -> Origin030
  Placement = pos=(-11,-15,0) rot=(0,0,1;0rad)
  Tip = -> Pad021
FEATURE [Sketcher::SketchObject] Sketch114
  FullyConstrained = false
  MapMode = 5
  Placement = pos=(0,0,0) rot=(0.57735,0.57735,0.57735;2.0944rad)
  Support = -> [YZ_Plane031]
  sketch-geometry (12):
    g0: LineSegment StartX=-2 StartY=5 StartZ=0 EndX=2 EndY=5 EndZ=0
    g1: LineSegment StartX=2 StartY=5 StartZ=0 EndX=2 EndY=0 EndZ=0
    g2: LineSegment StartX=2 StartY=0 StartZ=0 EndX=1.4 EndY=0 EndZ=0
    g3: LineSegment StartX=-2 StartY=0 StartZ=0 EndX=-2 EndY=5 EndZ=0
    g4: LineSegment StartX=-1.4 StartY=4 StartZ=0 EndX=-0.3 EndY=4 EndZ=0
    g5: LineSegment StartX=-0.3 StartY=4 StartZ=0 EndX=-0.3 EndY=0 EndZ=0
    g6: LineSegment StartX=-1.4 StartY=0 StartZ=0 EndX=-1.4 EndY=4 EndZ=0
    g7: LineSegment StartX=0.3 StartY=4 StartZ=0 EndX=1.4 EndY=4 EndZ=0
    g8: LineSegment StartX=1.4 StartY=4 StartZ=0 EndX=1.4 EndY=0 EndZ=0
    g9: LineSegment StartX=0.3 StartY=0 StartZ=0 EndX=0.3 EndY=4 EndZ=0
    g10: LineSegment StartX=-1.4 StartY=0 StartZ=0 EndX=-2 EndY=0 EndZ=0
    g11: LineSegment StartX=0.3 StartY=0 StartZ=0 EndX=-0.3 EndY=0 EndZ=0
  constraints (33):
    c: Coincident(g0,g1)
    c: Coincident(g1,g2)
    c: Coincident(g10,g3)
    c: Coincident(g3,g0)
    c: Horizontal(g0)
    c: Vertical(g1)
    c: Vertical(g3)
    c: PointOnObject(g1,g-1)
    c: Coincident(g4,g5)
    c: Coincident(g6,g4)
    c: Horizontal(g4)
    c: Vertical(g5)
    c: Vertical(g6)
    c: Coincident(g7,g8)
    c: Coincident(g9,g7)
    c: Horizontal(g7)
    c: Vertical(g8)
    c: Vertical(g9)
    c: Tangent(g2,g10)
    c: Coincident(g6,g10)
    c: Coincident(g5,g11)
    c: Coincident(g11,g9)
    c: Tangent(g2,g11)
    c: Coincident(g8,g2)
    c: Equal(g2,g11)
    c: Equal(g11,g10)
    c: Symmetric(g1,g3,g-2)
    c: Equal(g7,g4)
    c: DistanceX(g0,g0) = 4
    c: DistanceX(g2,g2) = 0.6
    c: DistanceY(g1,g1) = 5
    c: DistanceY(g8,g8) = 4
    c: PointOnObject(g4,g7)
FEATURE [PartDesign::Pad] Pad022
  Direction = (1,1,1)
  Length = 0.6
  Length2 = 100
  Midplane = true
  Placement = pos=(0,0,0) rot=(0.57735,0.57735,0.57735;2.0944rad)
  Profile = -> Sketch114
  Type = 0
FEATURE [PartDesign::Body] Body031  label="DallasPins001"
  Group = -> [Sketch114,Pad022]
  Origin = -> Origin031
  Placement = pos=(-11,-15,0) rot=(0,0,1;0rad)
  Tip = -> Pad022
FEATURE [Sketcher::SketchObject] Sketch115
  FullyConstrained = false
  MapMode = 5
  Placement = pos=(0,0,0) rot=(1,0,0;1.5708rad)
  Support = -> [XZ_Plane029]
  sketch-geometry (10):
    g0: LineSegment StartX=0 StartY=1.9 StartZ=0 EndX=3.2 EndY=1.9 EndZ=0
    g1: LineSegment StartX=3.2 StartY=1.4 StartZ=0 EndX=0 EndY=1.4 EndZ=0
    g2: LineSegment StartX=0 StartY=1.4 StartZ=0 EndX=0 EndY=1.9 EndZ=0
    g3: LineSegment StartX=4 StartY=0.5 StartZ=0 EndX=5.5 EndY=0.5 EndZ=0
    g4: LineSegment StartX=5.5 StartY=0.5 StartZ=0 EndX=5.5 EndY=0 EndZ=0
    g5: LineSegment StartX=5.5 StartY=0 StartZ=0 EndX=4 EndY=0 EndZ=0
    g6: LineSegment StartX=3.2 StartY=1.4 StartZ=0 EndX=3.5221 EndY=0.352981 EndZ=0
    g7: LineSegment StartX=4 StartY=0.5 StartZ=0 EndX=3.6779 EndY=1.54702 EndZ=0
    g8: ArcOfCircle CenterX=3.2 CenterY=1.4 CenterZ=0 NormalX=0 NormalY=0 NormalZ=1 AngleXU=0 Radius=0.5 StartAngle=0.29845 EndAngle=1.5708
    g9: ArcOfCircle CenterX=4 CenterY=0.5 CenterZ=0 NormalX=0 NormalY=0 NormalZ=1 AngleXU=0 Radius=0.5 StartAngle=3.44004 EndAngle=4.71239
  constraints (26):
    c: Coincident(g1,g2)
    c: Coincident(g2,g0)
    c: Horizontal(g0)
    c: Horizontal(g1)
    c: Vertical(g2)
    c: PointOnObject(g0,g-2)
    c: Coincident(g3,g4)
    c: Coincident(g4,g5)
    c: Horizontal(g3)
    c: Horizontal(g5)
    c: Vertical(g4)
    c: PointOnObject(g4,g-1)
    c: Tangent(g0,g8) = 1.5708
    c: Tangent(g7,g8) = -1.5708
    c: Tangent(g6,g9) = -1.5708
    c: Tangent(g5,g9) = 1.5708
    c: Coincident(g3,g7)
    c: Coincident(g3,g9)
    c: Coincident(g1,g6)
    c: Coincident(g1,g8)
    c: Parallel(g6,g7)
    c: DistanceX(g3) = 5.5
    c: DistanceY(g4,g4) = 0.5
    c: DistanceX(g1) = 3.2
    c: DistanceY(g1) = 1.4
    c: DistanceX(g1,g3) = 0.8
FEATURE [PartDesign::Pad] Pad023
  Direction = (1,1,1)
  Length = 4
  Length2 = 100
  Midplane = true
  Placement = pos=(0,0,0) rot=(1,0,0;1.5708rad)
  Profile = -> Sketch115
  Type = 0
FEATURE [PartDesign::Mirrored] Mirrored  label="Mirrored014"
  BaseFeature = -> Pad023
  MirrorPlane = -> YZ_Plane029
  Originals = -> [Pad023]
  Placement = pos=(0,0,0) rot=(1,0,0;1.5708rad)
FEATURE [Sketcher::SketchObject] Sketch116
  FullyConstrained = false
  MapMode = 5
  Support = -> [XY_Plane029]
  sketch-geometry (4):
    g0: LineSegment StartX=6 StartY=0.9 StartZ=0 EndX=1 EndY=0.9 EndZ=0
    g1: LineSegment StartX=1 StartY=0.9 StartZ=0 EndX=1 EndY=-0.9 EndZ=0
    g2: LineSegment StartX=1 StartY=-0.9 StartZ=0 EndX=6 EndY=-0.9 EndZ=0
    g3: LineSegment StartX=6 StartY=-0.9 StartZ=0 EndX=6 EndY=0.9 EndZ=0
  constraints (11):
    c: Coincident(g0,g1)
    c: Coincident(g1,g2)
    c: Coincident(g2,g3)
    c: Coincident(g3,g0)
    c: Horizontal(g0)
    c: Horizontal(g2)
    c: Vertical(g1)
    c: Symmetric(g0,g2,g-1)
    c: DistanceY(g3,g3) = 1.8
    c: DistanceX(g0) = 6
    c: DistanceX(g0) = 1
FEATURE [PartDesign::Pocket] Pocket027
  BaseFeature = -> Mirrored
  Length = 5
  Length2 = 100
  Midplane = true
  Placement = pos=(0,0,0) rot=(1,0,0;1.5708rad)
  Profile = -> Sketch116
  Type = 1
FEATURE [PartDesign::Mirrored] Mirrored019
  BaseFeature = -> Pocket027
  MirrorPlane = -> YZ_Plane029
  Originals = -> [Pocket027]
  Placement = pos=(0,0,0) rot=(1,0,0;1.5708rad)
FEATURE [PartDesign::Body] Body029  label="PinsDevice003"
  Group = -> [Sketch115,Pad023,Mirrored,Sketch116,Pocket027,Mirrored019]
  Origin = -> Origin029
  Placement = pos=(0,-2.35,0) rot=(0,0,1;0rad)
  Tip = -> Mirrored019
FEATURE [Sketcher::SketchObject] Sketch117
  FullyConstrained = false
  MapMode = 5
  Placement = pos=(0,0,0) rot=(0.57735,0.57735,0.57735;2.0944rad)
  Support = -> [YZ_Plane032]
  sketch-geometry (4):
    g0: LineSegment StartX=-2.25 StartY=3.6 StartZ=0 EndX=2.25 EndY=3.6 EndZ=0
    g1: LineSegment StartX=2.25 StartY=3.6 StartZ=0 EndX=2.25 EndY=0 EndZ=0
    g2: LineSegment StartX=2.25 StartY=0 StartZ=0 EndX=-2.25 EndY=0 EndZ=0
    g3: LineSegment StartX=-2.25 StartY=0 StartZ=0 EndX=-2.25 EndY=3.6 EndZ=0
  constraints (11):
    c: Coincident(g0,g1)
    c: Coincident(g1,g2)
    c: Coincident(g2,g3)
    c: Coincident(g3,g0)
    c: Horizontal(g2)
    c: Vertical(g1)
    c: Vertical(g3)
    c: DistanceX(g0,g0) = 4.5
    c: DistanceY(g1,g1) = 3.6
    c: PointOnObject(g1,g-1)
    c: Symmetric(g0,g0,g-2)
FEATURE [PartDesign::Pad] Pad025
  Direction = (1,1,1)
  Length = 6.3
  Length2 = 100
  Midplane = true
  Placement = pos=(0,0,0) rot=(0.57735,0.57735,0.57735;2.0944rad)
  Profile = -> Sketch117
  Type = 0
FEATURE [PartDesign::Body] Body032  label="BodyDevice004"
  Group = -> [Sketch117,Pad025]
  Origin = -> Origin033
  Placement = pos=(0,12.65,0) rot=(0,0,1;0rad)
  Tip = -> Pad025
FEATURE [Sketcher::SketchObject] Sketch118
  FullyConstrained = false
  MapMode = 5
  Support = -> [XY_Plane032]
  sketch-geometry (4):
    g0: LineSegment StartX=6 StartY=0.9 StartZ=0 EndX=1 EndY=0.9 EndZ=0
    g1: LineSegment StartX=1 StartY=0.9 StartZ=0 EndX=1 EndY=-0.9 EndZ=0
    g2: LineSegment StartX=1 StartY=-0.9 StartZ=0 EndX=6 EndY=-0.9 EndZ=0
    g3: LineSegment StartX=6 StartY=-0.9 StartZ=0 EndX=6 EndY=0.9 EndZ=0
  constraints (11):
    c: Coincident(g0,g1)
    c: Coincident(g1,g2)
    c: Coincident(g2,g3)
    c: Coincident(g3,g0)
    c: Horizontal(g0)
    c: Horizontal(g2)
    c: Vertical(g1)
    c: Symmetric(g0,g2,g-1)
    c: DistanceY(g3,g3) = 1.8
    c: DistanceX(g0) = 6
    c: DistanceX(g0) = 1
FEATURE [Sketcher::SketchObject] Sketch119
  FullyConstrained = false
  MapMode = 5
  Placement = pos=(0,0,0) rot=(1,0,0;1.5708rad)
  Support = -> [XZ_Plane033]
  sketch-geometry (10):
    g0: LineSegment StartX=0 StartY=1.9 StartZ=0 EndX=3.2 EndY=1.9 EndZ=0
    g1: LineSegment StartX=3.2 StartY=1.4 StartZ=0 EndX=0 EndY=1.4 EndZ=0
    g2: LineSegment StartX=0 StartY=1.4 StartZ=0 EndX=0 EndY=1.9 EndZ=0
    g3: LineSegment StartX=4 StartY=0.5 StartZ=0 EndX=5.5 EndY=0.5 EndZ=0
    g4: LineSegment StartX=5.5 StartY=0.5 StartZ=0 EndX=5.5 EndY=0 EndZ=0
    g5: LineSegment StartX=5.5 StartY=0 StartZ=0 EndX=4 EndY=0 EndZ=0
    g6: LineSegment StartX=3.2 StartY=1.4 StartZ=0 EndX=3.5221 EndY=0.352981 EndZ=0
    g7: LineSegment StartX=4 StartY=0.5 StartZ=0 EndX=3.6779 EndY=1.54702 EndZ=0
    g8: ArcOfCircle CenterX=3.2 CenterY=1.4 CenterZ=0 NormalX=0 NormalY=0 NormalZ=1 AngleXU=0 Radius=0.5 StartAngle=0.29845 EndAngle=1.5708
    g9: ArcOfCircle CenterX=4 CenterY=0.5 CenterZ=0 NormalX=0 NormalY=0 NormalZ=1 AngleXU=0 Radius=0.5 StartAngle=3.44004 EndAngle=4.71239
  constraints (26):
    c: Coincident(g1,g2)
    c: Coincident(g2,g0)
    c: Horizontal(g0)
    c: Horizontal(g1)
    c: Vertical(g2)
    c: PointOnObject(g0,g-2)
    c: Coincident(g3,g4)
    c: Coincident(g4,g5)
    c: Horizontal(g3)
    c: Horizontal(g5)
    c: Vertical(g4)
    c: PointOnObject(g4,g-1)
    c: Tangent(g0,g8) = 1.5708
    c: Tangent(g7,g8) = -1.5708
    c: Tangent(g6,g9) = -1.5708
    c: Tangent(g5,g9) = 1.5708
    c: Coincident(g3,g7)
    c: Coincident(g3,g9)
    c: Coincident(g1,g6)
    c: Coincident(g1,g8)
    c: Parallel(g6,g7)
    c: DistanceX(g3) = 5.5
    c: DistanceY(g4,g4) = 0.5
    c: DistanceX(g1) = 3.2
    c: DistanceY(g1) = 1.4
    c: DistanceX(g1,g3) = 0.8
FEATURE [PartDesign::Pad] Pad024
  Direction = (1,1,1)
  Length = 4
  Length2 = 100
  Midplane = true
  Placement = pos=(0,0,0) rot=(1,0,0;1.5708rad)
  Profile = -> Sketch119
  Type = 0
FEATURE [PartDesign::Mirrored] Mirrored020
  BaseFeature = -> Pad024
  MirrorPlane = -> YZ_Plane033
  Originals = -> [Pad024]
  Placement = pos=(0,0,0) rot=(1,0,0;1.5708rad)
FEATURE [PartDesign::Pocket] Pocket028
  BaseFeature = -> Mirrored020
  Length = 5
  Length2 = 100
  Midplane = true
  Placement = pos=(0,0,0) rot=(1,0,0;1.5708rad)
  Profile = -> Sketch118
  Type = 1
FEATURE [PartDesign::Mirrored] Mirrored003  label="Mirrored021"
  BaseFeature = -> Pocket028
  MirrorPlane = -> YZ_Plane033
  Originals = -> [Pocket028]
  Placement = pos=(0,0,0) rot=(1,0,0;1.5708rad)
FEATURE [PartDesign::Body] Body033  label="PinsDevice004"
  Group = -> [Sketch119,Pad024,Mirrored020,Sketch118,Pocket028,Mirrored003]
  Origin = -> Origin032
  Placement = pos=(0,12.65,0) rot=(0,0,1;0rad)
  Tip = -> Mirrored003
FEATURE [Sketcher::SketchObject] Sketch120
  FullyConstrained = false
  MapMode = 5
  Support = -> [XY_Plane027]
  sketch-geometry (1):
    g0: Circle CenterX=11.45 CenterY=-11.09 CenterZ=0 NormalX=0 NormalY=0 NormalZ=1 AngleXU=0 Radius=0.5
  constraints (3):
    c: DistanceX(g-1,g0) = 11.45
    c: DistanceY(g0,g-1) = 11.09
    c: Diameter(g0) = 1
FEATURE [PartDesign::Pocket] Pocket029
  BaseFeature = -> Pad019
  Length = 5
  Length2 = 100
  Midplane = true
  Profile = -> Sketch120
  Type = 1
FEATURE [PartDesign::LinearPattern] LinearPattern008
  Direction = -> Y_Axis027
  Length = 20.32
  Occurrences = 9
FEATURE [PartDesign::Mirrored] Mirrored021  label="Mirrored022"
  MirrorPlane = -> YZ_Plane027
FEATURE [PartDesign::MultiTransform] MultiTransform005
  BaseFeature = -> Pocket029
  Originals = -> [Pocket029]
  Transformations = -> [LinearPattern008,Mirrored021]
FEATURE [PartDesign::Body] Body027  label="PCB002"
  Group = -> [Sketch111,Pad019,Sketch120,Pocket029,MultiTransform005,LinearPattern008,Mirrored021]
  Origin = -> Origin027
  Tip = -> MultiTransform005
FEATURE [Part::Compound] Compound002  label="DIYless ESP8266 Master shield"
  Links = -> [Body027,Part__Feature003,Body028,Body029,Body030,Body031,Body032,Body033]
  Placement = pos=(-15,-10.5,-19) rot=(-1,0,0;1.5708rad)
FEATURE [Sketcher::SketchObject] Sketch121  label="hb cavity adaptor pcb"
  AttachmentOffset = pos=(0,0,5) rot=(0,0,1;0rad)
  FullyConstrained = false
  MapMode = 5
  Placement = pos=(0,-5,-1.1e-15) rot=(1,0,0;1.5708rad)
  Support = -> [XZ_Plane013]
  sketch-geometry (13):
    g0: LineSegment StartX=-27.75 StartY=-1 StartZ=0 EndX=-2.25 EndY=-1 EndZ=0
    g1: LineSegment StartX=-1.25 StartY=-2 StartZ=0 EndX=-1.25 EndY=-36 EndZ=0
    g2: LineSegment StartX=-2.25 StartY=-37 StartZ=0 EndX=-27.75 EndY=-37 EndZ=0
    g3: LineSegment StartX=-28.75 StartY=-36 StartZ=0 EndX=-28.75 EndY=-2 EndZ=0
    g4: LineSegment StartX=-27.75 StartY=-2 StartZ=0 EndX=-2.25 EndY=-2 EndZ=0
    g5: LineSegment StartX=-2.25 StartY=-2 StartZ=0 EndX=-2.25 EndY=-36 EndZ=0
    g6: LineSegment StartX=-2.25 StartY=-36 StartZ=0 EndX=-27.75 EndY=-36 EndZ=0
    g7: LineSegment StartX=-27.75 StartY=-36 StartZ=0 EndX=-27.75 EndY=-2 EndZ=0
    g8: LineSegment StartX=-15 StartY=0 StartZ=0 EndX=-15 EndY=-37 EndZ=0
    g9: ArcOfCircle CenterX=-2.25 CenterY=-2 CenterZ=0 NormalX=0 NormalY=0 NormalZ=1 AngleXU=0 Radius=1 StartAngle=0 EndAngle=1.5708
    g10: ArcOfCircle CenterX=-27.75 CenterY=-2 CenterZ=0 NormalX=0 NormalY=0 NormalZ=1 AngleXU=0 Radius=1 StartAngle=1.5708 EndAngle=3.14159
    g11: ArcOfCircle CenterX=-27.75 CenterY=-36 CenterZ=0 NormalX=0 NormalY=0 NormalZ=1 AngleXU=0 Radius=1 StartAngle=3.14159 EndAngle=4.71239
    g12: ArcOfCircle CenterX=-2.25 CenterY=-36 CenterZ=0 NormalX=0 NormalY=0 NormalZ=1 AngleXU=0 Radius=1 StartAngle=4.71239 EndAngle=6.28319
  constraints (31):
    c: Horizontal(g0)
    c: Horizontal(g2)
    c: Vertical(g1)
    c: Vertical(g3)
    c: Coincident(g4,g5)
    c: Coincident(g5,g6)
    c: Coincident(g6,g7)
    c: Coincident(g7,g4)
    c: Horizontal(g4)
    c: Horizontal(g6)
    c: Vertical(g5)
    c: PointOnObject(g8,g-1)
    c: PointOnObject(g8,g2)
    c: Symmetric(g5,g6,g8)
    c: Tangent(g0,g9) = 1.5708
    c: Tangent(g1,g9) = 1.5708
    c: Tangent(g0,g10) = 1.5708
    c: Tangent(g3,g10) = 1.5708
    c: Tangent(g2,g11) = 1.5708
    c: Tangent(g3,g11) = 1.5708
    c: Tangent(g2,g12) = 1.5708
    c: Tangent(g1,g12) = 1.5708
    c: Coincident(g5,g12)
    c: Coincident(g6,g11)
    c: Coincident(g4,g10)
    c: Coincident(g4,g9)
    c: Radius(g9) = 1
    c: DistanceX(g4,g4) = 25.5
    c: DistanceX(g8,g-1) = 15
    c: DistanceY(g9,g-1) = 2
    c: DistanceY(g5,g5) = 34
FEATURE [Sketcher::SketchObject] Sketch122  label="hb pillar adaptor 2"
  AttachmentOffset = pos=(0,0,-5) rot=(0,0,1;0rad)
  FullyConstrained = false
  MapMode = 5
  Placement = pos=(0,0,-5) rot=(0,0,1;0rad)
  Support = -> [XY_Plane013]
  sketch-geometry (8):
    g0: LineSegment StartX=-5.2 StartY=-4.5 StartZ=0 EndX=-5.2 EndY=-13 EndZ=0
    g1: LineSegment StartX=-5.2 StartY=-13 StartZ=0 EndX=-4.6 EndY=-13 EndZ=0
    g2: LineSegment StartX=-3.7 StartY=-10.5 StartZ=0 EndX=-3.1 EndY=-10.5 EndZ=0
    g3: LineSegment StartX=-3.1 StartY=-10.5 StartZ=0 EndX=-3.1 EndY=-4.5 EndZ=0
    g4: LineSegment StartX=-3.1 StartY=-4.5 StartZ=0 EndX=-5.2 EndY=-4.5 EndZ=0
    g5: LineSegment StartX=-5.2 StartY=-13 StartZ=0 EndX=-5.2 EndY=-20.8062 EndZ=0
    g6: ArcOfCircle CenterX=-11.3876 CenterY=-9.14447 CenterZ=0 NormalX=0 NormalY=0 NormalZ=1 AngleXU=0 Radius=7.80617 StartAngle=5.76661 EndAngle=6.10865
    g7: LineSegment StartX=-11.3876 StartY=-9.14447 StartZ=0 EndX=-3.7 EndY=-10.5 EndZ=0
  constraints (24):
    c: Vertical(g0)
    c: Coincident(g0,g1)
    c: Horizontal(g2)
    c: Coincident(g2,g3)
    c: Vertical(g3)
    c: Coincident(g3,g4)
    c: Coincident(g4,g0)
    c: DistanceY(g0,g-1) = 4.5
    c: Horizontal(g4)
    c: DistanceX(g0,g2) = 1.5
    c: Horizontal(g1)
    c: DistanceY(g2,g-1) = 10.5
    c: DistanceY(g1,g2) = 2.5
    c: Coincident(g5,g0)
    c: Vertical(g5)
    c: DistanceX(g0,g-1) = 5.2
    c: DistanceX(g2,g2) = 0.6
    c: Coincident(g6,g2)
    c: Coincident(g6,g1)
    c: Coincident(g7,g6)
    c: Coincident(g7,g2)
    c: Angle(g2,g7) = 2.96706
    c: DistanceX(g1,g1) = 0.6
    c: Equal(g5,g7)
FEATURE [Sketcher::SketchObject] Sketch008
  AttachmentOffset = pos=(0,0,4) rot=(0,0,1;0rad)
  FullyConstrained = false
  MapMode = 5
  Placement = pos=(0,0,4) rot=(0,0,1;0rad)
  Support = -> [XY_Plane034]
  sketch-geometry (2):
    g0: ArcOfCircle CenterX=0 CenterY=0 CenterZ=0 NormalX=0 NormalY=0 NormalZ=1 AngleXU=0 Radius=2.3 StartAngle=0.9701 EndAngle=5.31309
    g1: LineSegment StartX=1.3 StartY=1.89737 StartZ=0 EndX=1.3 EndY=-1.89737 EndZ=0
  constraints (6):
    c: Coincident(g1,g0)
    c: Coincident(g1,g0)
    c: Coincident(g0,g-1)
    c: DistanceX(g0,g0) = 1.3
    c: Diameter(g0) = 4.6
    c: Vertical(g1)
FEATURE [PartDesign::Pad] Pad026
  Direction = (1,1,1)
  Length = 4.7
  Length2 = 100
  Profile = -> Sketch008
  Type = 0
FEATURE [PartDesign::Body] Body034  label="DallasSensor"
  Group = -> [Sketch008,Pad026]
  Origin = -> Origin034
  Tip = -> Pad026
FEATURE [Sketcher::SketchObject] Sketch125  label="Sketch009"
  FullyConstrained = false
  MapMode = 5
  Placement = pos=(0,0,0) rot=(0.57735,0.57735,0.57735;2.0944rad)
  Support = -> [YZ_Plane035]
  sketch-geometry (12):
    g0: LineSegment StartX=-2 StartY=5 StartZ=0 EndX=2 EndY=5 EndZ=0
    g1: LineSegment StartX=2 StartY=5 StartZ=0 EndX=2 EndY=0 EndZ=0
    g2: LineSegment StartX=2 StartY=0 StartZ=0 EndX=1.4 EndY=0 EndZ=0
    g3: LineSegment StartX=-2 StartY=0 StartZ=0 EndX=-2 EndY=5 EndZ=0
    g4: LineSegment StartX=-1.4 StartY=4 StartZ=0 EndX=-0.3 EndY=4 EndZ=0
    g5: LineSegment StartX=-0.3 StartY=4 StartZ=0 EndX=-0.3 EndY=0 EndZ=0
    g6: LineSegment StartX=-1.4 StartY=0 StartZ=0 EndX=-1.4 EndY=4 EndZ=0
    g7: LineSegment StartX=0.3 StartY=4 StartZ=0 EndX=1.4 EndY=4 EndZ=0
    g8: LineSegment StartX=1.4 StartY=4 StartZ=0 EndX=1.4 EndY=0 EndZ=0
    g9: LineSegment StartX=0.3 StartY=0 StartZ=0 EndX=0.3 EndY=4 EndZ=0
    g10: LineSegment StartX=-1.4 StartY=0 StartZ=0 EndX=-2 EndY=0 EndZ=0
    g11: LineSegment StartX=0.3 StartY=0 StartZ=0 EndX=-0.3 EndY=0 EndZ=0
  constraints (33):
    c: Coincident(g0,g1)
    c: Coincident(g1,g2)
    c: Coincident(g10,g3)
    c: Coincident(g3,g0)
    c: Horizontal(g0)
    c: Vertical(g1)
    c: Vertical(g3)
    c: PointOnObject(g1,g-1)
    c: Coincident(g4,g5)
    c: Coincident(g6,g4)
    c: Horizontal(g4)
    c: Vertical(g5)
    c: Vertical(g6)
    c: Coincident(g7,g8)
    c: Coincident(g9,g7)
    c: Horizontal(g7)
    c: Vertical(g8)
    c: Vertical(g9)
    c: Tangent(g2,g10)
    c: Coincident(g6,g10)
    c: Coincident(g5,g11)
    c: Coincident(g11,g9)
    c: Tangent(g2,g11)
    c: Coincident(g8,g2)
    c: Equal(g2,g11)
    c: Equal(g11,g10)
    c: Symmetric(g1,g3,g-2)
    c: Equal(g7,g4)
    c: DistanceX(g0,g0) = 4
    c: DistanceX(g2,g2) = 0.6
    c: DistanceY(g1,g1) = 5
    c: DistanceY(g8,g8) = 4
    c: PointOnObject(g4,g7)
FEATURE [PartDesign::Pad] Pad027
  Direction = (1,1,1)
  Length = 0.6
  Length2 = 100
  Midplane = true
  Placement = pos=(0,0,0) rot=(0.57735,0.57735,0.57735;2.0944rad)
  Profile = -> Sketch125
  Type = 0
FEATURE [PartDesign::Body] Body035  label="DallasPins"
  Group = -> [Sketch125,Pad027]
  Origin = -> Origin035
  Tip = -> Pad027
FEATURE [Part::Compound] Compound003  label="Dallas Sensor"
  Links = -> [Body034,Body035]
  Placement = pos=(-52,-11.5,-25) rot=(0.57735,-0.57735,-0.57735;2.0944rad)
FEATURE [Sketcher::SketchObject] Sketch131  label="hb separation top"
  AttachmentOffset = pos=(0,0,9) rot=(0,0,1;0rad)
  FullyConstrained = false
  MapMode = 5
  Placement = pos=(0,-9,-2e-15) rot=(1,0,0;1.5708rad)
  Support = -> [XZ_Plane013]
  sketch-geometry (5):
    g0: ArcOfCircle CenterX=41 CenterY=14 CenterZ=0 NormalX=0 NormalY=0 NormalZ=1 AngleXU=0 Radius=6 StartAngle=8.262e-13 EndAngle=3.14159
    g1: ArcOfCircle CenterX=41 CenterY=-14 CenterZ=0 NormalX=0 NormalY=0 NormalZ=1 AngleXU=0 Radius=6 StartAngle=3.14159 EndAngle=6.28319
    g2: LineSegment StartX=35 StartY=14 StartZ=0 EndX=35 EndY=-14 EndZ=0
    g3: LineSegment StartX=47 StartY=14 StartZ=0 EndX=47 EndY=-14 EndZ=0
    g4: Circle CenterX=0 CenterY=0 CenterZ=0 NormalX=0 NormalY=0 NormalZ=1 AngleXU=0 Radius=90
  constraints (11):
    c: Tangent(g0,g3)
    c: Tangent(g0,g2)
    c: Tangent(g2,g1)
    c: Tangent(g3,g1)
    c: Vertical(g2)
    c: DistanceX(g0) = 41
    c: Symmetric(g0,g1,g-1)
    c: DistanceY(g1,g0) = 28
    c: Radius(g0) = 6
    c: Coincident(g4,g-1)
    c: Radius(g4) = 90
FEATURE [PartDesign::Plane] DatumPlane002  label="HB ButtonPlane"
  AttachmentOffset = pos=(0,0,41) rot=(0,0,1;0rad)
  Length = 63.3835
  MapMode = 5
  Placement = pos=(41,-9.1e-15,9.1e-15) rot=(0.57735,0.57735,0.57735;2.0944rad)
  ResizeMode = 0
  Support = -> [YZ_Plane013]
  Width = 102.942
FEATURE [Sketcher::SketchObject] Sketch132  label="hb button nut hole"
  AttachmentOffset = pos=(0,0,13) rot=(0,0,1;0rad)
  ExternalGeometry = -> [DatumPlane002]
  FullyConstrained = false
  MapMode = 5
  Placement = pos=(0,-13,-2.9e-15) rot=(1,0,0;1.5708rad)
  Support = -> [XZ_Plane013]
  sketch-geometry (7):
    g0: LineSegment StartX=32 StartY=-9.7 StartZ=0 EndX=43.4826 EndY=-9.7 EndZ=0
    g1: LineSegment StartX=43.4826 StartY=-9.7 StartZ=0 EndX=45.9652 EndY=-14 EndZ=0
    g2: LineSegment StartX=45.9652 StartY=-14 StartZ=0 EndX=43.4826 EndY=-18.3 EndZ=0
    g3: LineSegment StartX=43.4826 StartY=-18.3 StartZ=0 EndX=32 EndY=-18.3 EndZ=0
    g4: LineSegment StartX=32 StartY=-18.3 StartZ=0 EndX=32 EndY=-9.7 EndZ=0
    g5: Circle CenterX=41 CenterY=-14 CenterZ=0 NormalX=0 NormalY=0 NormalZ=1 AngleXU=0 Radius=4.3
    g6: LineSegment StartX=41 StartY=-14 StartZ=0 EndX=32 EndY=-14 EndZ=0
  constraints (20):
    c: Horizontal(g0)
    c: Coincident(g0,g1)
    c: Coincident(g1,g2)
    c: Coincident(g2,g3)
    c: Horizontal(g3)
    c: Coincident(g3,g4)
    c: Coincident(g4,g0)
    c: Vertical(g4)
    c: Tangent(g5,g1)
    c: Coincident(g6,g5)
    c: PointOnObject(g6,g4)
    c: Horizontal(g6)
    c: DistanceY(g5,g-1) = 14
    c: Tangent(g5,g3)
    c: Tangent(g5,g2)
    c: Symmetric(g0,g2,g6)
    c: Angle(g1,g2) = 2.0944
    c: DistanceY(g2,g0) = 8.6
    c: DistanceX(g0,g5) = 9
    c: PointOnObject(g5,g-3)
FEATURE [Sketcher::SketchObject] Sketch133  label="hb button screw hole"
  ExternalGeometry = -> [DatumPlane002]
  FullyConstrained = false
  MapMode = 5
  Placement = pos=(0,0,0) rot=(1,0,0;1.5708rad)
  Support = -> [XZ_Plane013]
  sketch-geometry (1):
    g0: Circle CenterX=41 CenterY=-14 CenterZ=0 NormalX=0 NormalY=0 NormalZ=1 AngleXU=0 Radius=2.65
  constraints (3):
    c: PointOnObject(g0,g-3)
    c: DistanceY(g0,g-1) = 14
    c: Diameter(g0) = 5.3
FEATURE [PartDesign::Pocket] Pocket036  label="HB Button screw hole 1"
  BaseFeature = -> Fillet001
  Length = 5
  Length2 = 100
  Midplane = true
  Profile = -> Sketch133
  Type = 1
FEATURE [PartDesign::Pocket] Pocket035  label="HB Button nut hole 1"
  BaseFeature = -> Pocket036
  Length = 5
  Length2 = 100
  Profile = -> Sketch132
  Type = 1
FEATURE [Sketcher::SketchObject] Sketch134  label="hb cutout button low"
  AttachmentOffset = pos=(0,0,20) rot=(0,0,1;0rad)
  ExternalGeometry = -> [DatumPlane002]
  FullyConstrained = false
  MapMode = 5
  Placement = pos=(0,-20,-4.4e-15) rot=(1,0,0;1.5708rad)
  Support = -> [XZ_Plane013]
  sketch-geometry (4):
    g0: ArcOfCircle CenterX=41 CenterY=-14 CenterZ=0 NormalX=0 NormalY=0 NormalZ=1 AngleXU=0 Radius=5.2 StartAngle=1.5708 EndAngle=4.71239
    g1: LineSegment StartX=41 StartY=-19.2 StartZ=0 EndX=75 EndY=-19.2 EndZ=0
    g2: LineSegment StartX=41 StartY=-8.8 StartZ=0 EndX=75 EndY=-8.8 EndZ=0
    g3: LineSegment StartX=75 StartY=-8.8 StartZ=0 EndX=75 EndY=-19.2 EndZ=0
  constraints (11):
    c: Tangent(g0,g2)
    c: Tangent(g0,g1)
    c: Horizontal(g1)
    c: DistanceY(g0,g-1) = 14
    c: Radius(g0) = 5.2
    c: Coincident(g3,g2)
    c: Coincident(g3,g1)
    c: Vertical(g3)
    c: DistanceX(g2) = 75
    c: Horizontal(g2)
    c: PointOnObject(g0,g-3)
FEATURE [Sketcher::SketchObject] Sketch135  label="hb cutout button high"
  AttachmentOffset = pos=(0,0,22) rot=(0,0,1;0rad)
  ExternalGeometry = -> [DatumPlane002]
  FullyConstrained = false
  MapMode = 5
  Placement = pos=(0,-22,-4.9e-15) rot=(1,0,0;1.5708rad)
  Support = -> [XZ_Plane013]
  sketch-geometry (5):
    g0: ArcOfCircle CenterX=41 CenterY=-14 CenterZ=0 NormalX=0 NormalY=0 NormalZ=1 AngleXU=0 Radius=6.4 StartAngle=1.7017 EndAngle=4.58149
    g1: LineSegment StartX=40.1646 StartY=-20.3452 StartZ=0 EndX=75 EndY=-24.9314 EndZ=0
    g2: LineSegment StartX=40.1646 StartY=-7.65475 StartZ=0 EndX=75 EndY=-3.06859 EndZ=0
    g3: LineSegment StartX=75 StartY=-3.06859 StartZ=0 EndX=75 EndY=-24.9314 EndZ=0
    g4: LineSegment StartX=41 StartY=-14 StartZ=0 EndX=75 EndY=-14 EndZ=0
  constraints (13):
    c: Tangent(g0,g2)
    c: Tangent(g0,g1)
    c: DistanceY(g0,g-1) = 14
    c: Radius(g0) = 6.4
    c: Coincident(g3,g2)
    c: Coincident(g3,g1)
    c: Vertical(g3)
    c: DistanceX(g2) = 75
    c: Coincident(g4,g0)
    c: PointOnObject(g4,g3)
    c: Symmetric(g1,g2,g4)
    c: Angle(g1,g2) = 0.261799
    c: PointOnObject(g0,g-3)
FEATURE [PartDesign::SubtractiveLoft] SubtractiveLoft006  label="HB Cutout button top 1"
  BaseFeature = -> Pocket035
  Closed = false
  Profile = -> Sketch134
  Ruled = false
  Sections = -> [Sketch135]
FEATURE [Sketcher::SketchObject] Sketch136  label="ht cutout for buttons btm"
  AttachmentOffset = pos=(0,0,9.5) rot=(0,0,1;0rad)
  ExternalGeometry = -> [DatumPlane001]
  FullyConstrained = true
  MapMode = 5
  Placement = pos=(0,-9.5,-2.1e-15) rot=(1,0,0;1.5708rad)
  Support = -> [XZ_Plane014]
  sketch-geometry (4):
    g0: ArcOfCircle CenterX=41 CenterY=14 CenterZ=0 NormalX=0 NormalY=0 NormalZ=1 AngleXU=0 Radius=8.5 StartAngle=2e-16 EndAngle=3.14159
    g1: ArcOfCircle CenterX=41 CenterY=-14 CenterZ=0 NormalX=0 NormalY=0 NormalZ=1 AngleXU=0 Radius=8.5 StartAngle=3.14159 EndAngle=6.28319
    g2: LineSegment StartX=32.5 StartY=14 StartZ=0 EndX=32.5 EndY=-14 EndZ=0
    g3: LineSegment StartX=49.5 StartY=14 StartZ=0 EndX=49.5 EndY=-14 EndZ=0
  constraints (9):
    c: Tangent(g0,g3)
    c: Tangent(g0,g2)
    c: Tangent(g2,g1)
    c: Tangent(g3,g1)
    c: Vertical(g2)
    c: PointOnObject(g0,g-3)
    c: Symmetric(g1,g0,g-1)
    c: DistanceY(g1,g0) = 28
    c: Radius(g0) = 8.5
FEATURE [Sketcher::SketchObject] Sketch150  label="ht cutout for buttons mid"
  AttachmentOffset = pos=(0,0,18.5) rot=(0,0,1;0rad)
  ExternalGeometry = -> [DatumPlane001]
  FullyConstrained = true
  MapMode = 5
  Placement = pos=(0,-18.5,-4.1e-15) rot=(1,0,0;1.5708rad)
  Support = -> [XZ_Plane014]
  sketch-geometry (4):
    g0: ArcOfCircle CenterX=41 CenterY=14 CenterZ=0 NormalX=0 NormalY=0 NormalZ=1 AngleXU=0 Radius=6.2 StartAngle=3e-16 EndAngle=3.14159
    g1: ArcOfCircle CenterX=41 CenterY=-14 CenterZ=0 NormalX=0 NormalY=0 NormalZ=1 AngleXU=0 Radius=6.2 StartAngle=3.14159 EndAngle=6.28319
    g2: LineSegment StartX=34.8 StartY=14 StartZ=0 EndX=34.8 EndY=-14 EndZ=0
    g3: LineSegment StartX=47.2 StartY=14 StartZ=0 EndX=47.2 EndY=-14 EndZ=0
  constraints (9):
    c: Tangent(g0,g3)
    c: Tangent(g0,g2)
    c: Tangent(g2,g1)
    c: Tangent(g3,g1)
    c: Vertical(g2)
    c: PointOnObject(g0,g-3)
    c: Symmetric(g1,g0,g-1)
    c: DistanceY(g1,g0) = 28
    c: Radius(g0) = 6.2
FEATURE [Sketcher::SketchObject] Sketch151  label="ht cutout for buttons top"
  AttachmentOffset = pos=(0,0,22) rot=(0,0,1;0rad)
  ExternalGeometry = -> [DatumPlane001]
  FullyConstrained = true
  MapMode = 5
  Placement = pos=(0,-22,-4.9e-15) rot=(1,0,0;1.5708rad)
  Support = -> [XZ_Plane014]
  sketch-geometry (4):
    g0: ArcOfCircle CenterX=41 CenterY=14 CenterZ=0 NormalX=0 NormalY=0 NormalZ=1 AngleXU=0 Radius=6.2 StartAngle=3e-16 EndAngle=3.14159
    g1: ArcOfCircle CenterX=41 CenterY=-14 CenterZ=0 NormalX=0 NormalY=0 NormalZ=1 AngleXU=0 Radius=6.2 StartAngle=3.14159 EndAngle=6.28319
    g2: LineSegment StartX=34.8 StartY=14 StartZ=0 EndX=34.8 EndY=-14 EndZ=0
    g3: LineSegment StartX=47.2 StartY=14 StartZ=0 EndX=47.2 EndY=-14 EndZ=0
  constraints (9):
    c: Tangent(g0,g3)
    c: Tangent(g0,g2)
    c: Tangent(g2,g1)
    c: Tangent(g3,g1)
    c: Vertical(g2)
    c: PointOnObject(g0,g-3)
    c: Symmetric(g1,g0,g-1)
    c: DistanceY(g1,g0) = 28
    c: Radius(g0) = 6.2
FEATURE [Sketcher::SketchObject] Sketch154  label="hb dallas pillar low"
  AttachmentOffset = pos=(0,0,9) rot=(0,0,1;0rad)
  ExternalGeometry = -> [Sketch121]
  FullyConstrained = true
  MapMode = 5
  Placement = pos=(0,-9,-2e-15) rot=(1,0,0;1.5708rad)
  Support = -> [XZ_Plane013]
  sketch-geometry (9):
    g0: LineSegment StartX=-29.75 StartY=-25 StartZ=0 EndX=-32.75 EndY=-25 EndZ=0
    g1: LineSegment StartX=-33.75 StartY=-26 StartZ=0 EndX=-33.75 EndY=-32 EndZ=0
    g2: LineSegment StartX=-32.75 StartY=-33 StartZ=0 EndX=-29.75 EndY=-33 EndZ=0
    g3: LineSegment StartX=-28.75 StartY=-32 StartZ=0 EndX=-28.75 EndY=-26 EndZ=0
    g4: LineSegment StartX=-33.75 StartY=-29 StartZ=0 EndX=-28.75 EndY=-29 EndZ=0
    g5: ArcOfCircle CenterX=-32.75 CenterY=-26 CenterZ=0 NormalX=0 NormalY=0 NormalZ=1 AngleXU=0 Radius=1 StartAngle=1.5708 EndAngle=3.14159
    g6: ArcOfCircle CenterX=-29.75 CenterY=-26 CenterZ=0 NormalX=0 NormalY=0 NormalZ=1 AngleXU=0 Radius=1 StartAngle=-3.6e-15 EndAngle=1.5708
    g7: ArcOfCircle CenterX=-29.75 CenterY=-32 CenterZ=0 NormalX=0 NormalY=0 NormalZ=1 AngleXU=0 Radius=1 StartAngle=4.71239 EndAngle=6.28319
    g8: ArcOfCircle CenterX=-32.75 CenterY=-32 CenterZ=0 NormalX=0 NormalY=0 NormalZ=1 AngleXU=0 Radius=1 StartAngle=3.14159 EndAngle=4.71239
  constraints (23):
    c: Horizontal(g0)
    c: Horizontal(g2)
    c: Vertical(g1)
    c: Vertical(g3)
    c: PointOnObject(g4,g1)
    c: PointOnObject(g4,g3)
    c: DistanceY(g4,g-1) = 29
    c: Tangent(g1,g5) = -1.5708
    c: Tangent(g0,g5) = -1.5708
    c: Tangent(g0,g6) = -1.5708
    c: Tangent(g3,g6) = -1.5708
    c: Tangent(g3,g7) = -1.5708
    c: Tangent(g2,g7) = -1.5708
    c: Tangent(g2,g8) = -1.5708
    c: Tangent(g1,g8) = -1.5708
    c: Equal(g7,g8)
    c: Equal(g8,g5)
    c: Equal(g5,g6)
    c: Radius(g6) = 1
    c: DistanceX(g1,g3) = 5
    c: DistanceY(g2,g0) = 8
    c: Symmetric(g8,g5,g4)
    c: PointOnObject(g3,g-3)
FEATURE [Sketcher::SketchObject] Sketch155  label="hb dallas pillar high"
  AttachmentOffset = pos=(0,0,18.5) rot=(0,0,1;0rad)
  ExternalGeometry = -> [Sketch121]
  FullyConstrained = true
  MapMode = 5
  Placement = pos=(0,-18.5,-4.1e-15) rot=(1,0,0;1.5708rad)
  Support = -> [XZ_Plane013]
  sketch-geometry (9):
    g0: LineSegment StartX=-29.75 StartY=-25.5 StartZ=0 EndX=-30.75 EndY=-25.5 EndZ=0
    g1: LineSegment StartX=-31.75 StartY=-26.5 StartZ=0 EndX=-31.75 EndY=-31.5 EndZ=0
    g2: LineSegment StartX=-30.75 StartY=-32.5 StartZ=0 EndX=-29.75 EndY=-32.5 EndZ=0
    g3: LineSegment StartX=-28.75 StartY=-31.5 StartZ=0 EndX=-28.75 EndY=-26.5 EndZ=0
    g4: LineSegment StartX=-31.75 StartY=-29 StartZ=0 EndX=-28.75 EndY=-29 EndZ=0
    g5: ArcOfCircle CenterX=-30.75 CenterY=-26.5 CenterZ=0 NormalX=0 NormalY=0 NormalZ=1 AngleXU=0 Radius=1 StartAngle=1.5708 EndAngle=3.14159
    g6: ArcOfCircle CenterX=-29.75 CenterY=-26.5 CenterZ=0 NormalX=0 NormalY=0 NormalZ=1 AngleXU=0 Radius=1 StartAngle=0 EndAngle=1.5708
    g7: ArcOfCircle CenterX=-29.75 CenterY=-31.5 CenterZ=0 NormalX=0 NormalY=0 NormalZ=1 AngleXU=0 Radius=1 StartAngle=4.71239 EndAngle=6.28319
    g8: ArcOfCircle CenterX=-30.75 CenterY=-31.5 CenterZ=0 NormalX=0 NormalY=0 NormalZ=1 AngleXU=0 Radius=1 StartAngle=3.14159 EndAngle=4.71239
  constraints (23):
    c: Horizontal(g0)
    c: Horizontal(g2)
    c: Vertical(g1)
    c: Vertical(g3)
    c: PointOnObject(g4,g1)
    c: PointOnObject(g4,g3)
    c: DistanceY(g4,g-1) = 29
    c: Tangent(g1,g5) = -1.5708
    c: Tangent(g0,g5) = -1.5708
    c: Tangent(g0,g6) = -1.5708
    c: Tangent(g3,g6) = -1.5708
    c: Tangent(g3,g7) = -1.5708
    c: Tangent(g2,g7) = -1.5708
    c: Tangent(g2,g8) = -1.5708
    c: Tangent(g1,g8) = -1.5708
    c: Equal(g7,g8)
    c: Equal(g8,g5)
    c: Equal(g5,g6)
    c: Radius(g6) = 1
    c: DistanceX(g1,g3) = 3
    c: DistanceY(g2,g0) = 7
    c: Symmetric(g8,g5,g4)
    c: PointOnObject(g3,g-3)
FEATURE [Sketcher::SketchObject] Sketch156  label="hb dallas cavity"
  AttachmentOffset = pos=(0,0,-35) rot=(0,0,1;0rad)
  FullyConstrained = true
  MapMode = 5
  Placement = pos=(-35,7.8e-15,-7.8e-15) rot=(0.57735,0.57735,0.57735;2.0944rad)
  Support = -> [YZ_Plane013]
  sketch-geometry (5):
    g0: ArcOfCircle CenterX=-16 CenterY=-29 CenterZ=0 NormalX=0 NormalY=0 NormalZ=1 AngleXU=0 Radius=2.45 StartAngle=4.18879 EndAngle=8.37758
    g1: LineSegment StartX=-17.225 StartY=-26.8782 StartZ=0 EndX=-19 EndY=-27.903 EndZ=0
    g2: LineSegment StartX=-19 StartY=-27.903 StartZ=0 EndX=-19 EndY=-30.097 EndZ=0
    g3: LineSegment StartX=-19 StartY=-30.097 StartZ=0 EndX=-17.225 EndY=-31.1218 EndZ=0
    g4: LineSegment StartX=-16 StartY=-29 StartZ=0 EndX=-19 EndY=-29 EndZ=0
  constraints (13):
    c: DistanceY(g0,g-1) = 29
    c: DistanceX(g0,g-1) = 16
    c: Radius(g0) = 2.45
    c: Coincident(g1,g2)
    c: Vertical(g2)
    c: Coincident(g2,g3)
    c: DistanceX(g1,g0) = 3
    c: Tangent(g0,g1) = -1.5708
    c: Tangent(g0,g3) = -1.5708
    c: Coincident(g4,g0)
    c: PointOnObject(g4,g2)
    c: Symmetric(g2,g1,g4)
    c: Angle(g3,g1) = 1.0472
FEATURE [PartDesign::Fillet] Fillet003  label="HB Button top fillet 1"
  Base = -> SubtractiveLoft006 [Edge32]
  BaseFeature = -> SubtractiveLoft006
  Radius = 1
  SupportTransform = false
FEATURE [PartDesign::LinearPattern] LinearPattern009  label="HB Button nut hole 2,3"
  BaseFeature = -> Fillet003
  Direction = -> Z_Axis014
  Length = 28
  Occurrences = 3
  Originals = -> [Pocket035,Pocket036,SubtractiveLoft006,Fillet003]
FEATURE [PartDesign::Pocket] Pocket008  label="HB Separation bottom"
  BaseFeature = -> LinearPattern009
  Length = 5
  Length2 = 100
  Midplane = true
  Profile = -> Sketch053
  Type = 1
FEATURE [PartDesign::Pocket] Pocket034  label="HB Separation top"
  BaseFeature = -> Pocket008
  Length = 5
  Length2 = 100
  Profile = -> Sketch131
  Reversed = true
  Type = 1
FEATURE [PartDesign::SubtractivePipe] SubtractivePipe004  label="HB Seal groove wall plate"
  AuxilleryCurvelinear = true
  AuxillerySpineTangent = false
  BaseFeature = -> Pocket034
  Binormal = (0,0,0)
  Mode = 0
  Profile = -> Sketch050
  Spine = -> Sketch047
  SpineTangent = false
  Transformation = 0
  Transition = 0
FEATURE [PartDesign::Pocket] Pocket009  label="HB Wall screw holes"
  BaseFeature = -> SubtractivePipe004
  Length = 5
  Length2 = 100
  Profile = -> Sketch055
  Type = 1
FEATURE [PartDesign::AdditivePipe] AdditivePipe003  label="HB Seal rim top"
  AuxilleryCurvelinear = true
  AuxillerySpineTangent = false
  BaseFeature = -> Pocket009
  Binormal = (0,0,0)
  Mode = 0
  Profile = -> Sketch064
  Spine = -> Sketch047
  SpineTangent = false
  Transformation = 0
  Transition = 0
FEATURE [PartDesign::Pocket] Pocket011  label="HB Cavity for wires"
  BaseFeature = -> AdditivePipe003
  Length = 5
  Length2 = 100
  Midplane = true
  Profile = -> Sketch066
  Type = 1
FEATURE [PartDesign::AdditiveLoft] AdditiveLoft002  label="HB Dallas pillar"
  BaseFeature = -> Pocket011
  Closed = false
  Profile = -> Sketch154
  Ruled = false
  Sections = -> [Sketch155]
FEATURE [PartDesign::Fillet] Fillet002  label="HB Dallas pillar fillet"
  Base = -> AdditiveLoft002 [Edge107]
  BaseFeature = -> AdditiveLoft002
  Radius = 1.5
  SupportTransform = false
FEATURE [PartDesign::Pocket] Pocket037  label="HB Dallas cavity"
  BaseFeature = -> Fillet002
  Length = 8
  Length2 = 100
  Profile = -> Sketch156
  Reversed = true
  Type = 0
FEATURE [PartDesign::Pocket] Pocket030  label="HB Cavity adaptor PCB"
  BaseFeature = -> Pocket037
  Length = 5
  Length2 = 100
  Profile = -> Sketch121
  Reversed = true
  Type = 1
FEATURE [PartDesign::Pocket] Pocket012  label="HB Cavity ESP"
  BaseFeature = -> Pocket030
  Length = 5
  Length2 = 100
  Profile = -> Sketch067
  Reversed = true
  Type = 1
FEATURE [PartDesign::Pocket] Pocket014  label="HB Cavity wires ESP"
  BaseFeature = -> Pocket012
  Length = 5
  Length2 = 100
  Profile = -> Sketch069
  Reversed = true
  Type = 0
FEATURE [PartDesign::Pocket] Pocket015  label="HB Hole USB port"
  BaseFeature = -> Pocket014
  Length = 5
  Length2 = 100
  Midplane = true
  Profile = -> Sketch070
  Type = 0
FEATURE [PartDesign::Groove] Groove  label="HB Magnet hole 1"
  Angle = 360
  Axis = (0,3.8,0)
  Base = (-50,-3.8,25)
  BaseFeature = -> Pocket015
  Profile = -> Sketch083
  ReferenceAxis = -> Sketch083 [Axis0]
FEATURE [PartDesign::MultiTransform] MultiTransform002  label="HB Magnet hole 2,3,4"
  BaseFeature = -> Groove
  Originals = -> [Groove]
  Transformations = -> [Mirrored010,Mirrored011]
FEATURE [PartDesign::AdditiveLoft] AdditiveLoft  label="HB PCB support TR"
  BaseFeature = -> MultiTransform002
  Closed = false
  Profile = -> Sketch088
  Ruled = false
  Sections = -> [Sketch087]
FEATURE [PartDesign::AdditiveLoft] AdditiveLoft001  label="HB PCB support TL"
  BaseFeature = -> AdditiveLoft
  Closed = false
  Profile = -> Sketch090
  Ruled = false
  Sections = -> [Sketch089]
FEATURE [PartDesign::Mirrored] Mirrored004  label="HB PCB support BL"
  BaseFeature = -> AdditiveLoft001
  MirrorPlane = -> XY_Plane013
  Originals = -> [AdditiveLoft001]
FEATURE [PartDesign::Revolution] Revolution004  label="HB PCB alignment pin TL"
  Angle = 360
  Axis = (0,14.5,0)
  Base = (-36.77,-14.5,18.45)
  BaseFeature = -> Mirrored004
  Profile = -> Sketch091
  ReferenceAxis = -> Sketch091 [Axis0]
FEATURE [PartDesign::LinearPattern] LinearPattern005  label="HB PCB alignment pin TR"
  BaseFeature = -> Revolution004
  Direction = -> X_Axis013
  Length = 67.26
  Occurrences = 2
  Originals = -> [Revolution004]
FEATURE [PartDesign::Mirrored] Mirrored005  label="HB PCB alignment pin BL"
  BaseFeature = -> LinearPattern005
  MirrorPlane = -> XY_Plane013
  Originals = -> [Revolution004]
FEATURE [PartDesign::Groove] Groove002  label="HB Screwhole bottom top 1"
  Angle = 360
  Axis = (0,2.8,0)
  Base = (40,-3,30)
  BaseFeature = -> Mirrored005
  Profile = -> Sketch102
  ReferenceAxis = -> Sketch102 [Axis0]
FEATURE [PartDesign::MultiTransform] MultiTransform  label="HB Screwhole bottom top 2,3,4"
  BaseFeature = -> Groove002
  Originals = -> [Groove002]
  Transformations = -> [Mirrored006,Mirrored007]
FEATURE [PartDesign::Revolution] Revolution009  label="HB Adaptor pillar 1"
  Angle = 360
  Axis = (0,-7.80617,0)
  Base = (-24.8,-13,-33.1)
  BaseFeature = -> MultiTransform
  Profile = -> Sketch110
  ReferenceAxis = -> Sketch110 [Axis0]
FEATURE [PartDesign::Revolution] Revolution010  label="HB Adaptor pillar 2"
  Angle = 360
  Axis = (0,-7.80617,0)
  Base = (-5.2,-13,-5)
  BaseFeature = -> Revolution009
  Profile = -> Sketch122
  ReferenceAxis = -> Sketch122 [Axis0]
FEATURE [PartDesign::Body] Body013  label="HousingBottom"
  Group = -> [Sketch048,Pad011,DatumPlane002,SubtractivePipe003,Fillet001,Pocket036,Pocket035,SubtractiveLoft006,Fillet003,LinearPattern009,Pocket008,Pocket034,Sketch047,Sketch045,Sketch050,Sketch053,Sketch055,SubtractivePipe004,Pocket009,Sketch064,AdditivePipe003,Sketch066,Pocket011,AdditiveLoft002,Fillet002,Pocket037,Pocket030,Sketch067,Pocket012,Sketch069,Pocket014,Sketch070,Pocket015,Sketch083,Groove,+32 more]
  Origin = -> Origin013
  Tip = -> Revolution010
FEATURE [PartDesign::Fillet] Fillet004  label="HT Fillet button top 1"
  Base = -> SubtractiveLoft001 [Edge32]
  BaseFeature = -> SubtractiveLoft001
  Radius = 1
  SupportTransform = false
FEATURE [PartDesign::LinearPattern] LinearPattern001  label="HT Cutout button 2,3"
  BaseFeature = -> Fillet004
  Direction = -> Z_Axis015
  Length = 28
  Occurrences = 3
  Originals = -> [SubtractiveLoft001,Fillet004]
FEATURE [PartDesign::Pocket] Pocket010  label="HT Separation top"
  BaseFeature = -> LinearPattern001
  Length = 5
  Length2 = 100
  Midplane = true
  Profile = -> Sketch062
  Type = 1
FEATURE [PartDesign::SubtractiveLoft] SubtractiveLoft008  label="HT Cutout buttons"
  BaseFeature = -> Pocket010
  Closed = false
  Profile = -> Sketch136
  Ruled = true
  Sections = -> [Sketch150,Sketch151]
FEATURE [PartDesign::SubtractivePipe] SubtractivePipe  label="HT Seal groove bottom"
  AuxilleryCurvelinear = true
  AuxillerySpineTangent = false
  BaseFeature = -> SubtractiveLoft008
  Binormal = (0,0,0)
  Mode = 0
  Profile = -> Sketch065
  Spine = -> Sketch061
  SpineTangent = false
  Transformation = 0
  Transition = 0
FEATURE [PartDesign::SubtractiveLoft] SubtractiveLoft  label="HT Screen view"
  BaseFeature = -> SubtractivePipe
  Closed = false
  Profile = -> Sketch071
  Ruled = false
  Sections = -> [Sketch072]
FEATURE [PartDesign::Pocket] Pocket016  label="HT Screen glass cavity"
  BaseFeature = -> SubtractiveLoft
  Length = 5
  Length2 = 100
  Profile = -> Sketch073
  Type = 1
FEATURE [PartDesign::Pocket] Pocket017  label="HT Cutout PCB"
  BaseFeature = -> Pocket016
  Length = 5
  Length2 = 100
  Profile = -> Sketch074
  Type = 1
FEATURE [PartDesign::Groove] Groove003  label="HT Screwhole bottom top 1"
  Angle = 360
  Axis = (0,2.8,0)
  Base = (40,-3,30)
  BaseFeature = -> Pocket017
  Profile = -> Sketch103
  ReferenceAxis = -> Sketch103 [Axis0]
FEATURE [PartDesign::MultiTransform] MultiTransform001  label="HT Screwhole bottom top 2,3,4"
  BaseFeature = -> Groove003
  Originals = -> [Groove003]
  Transformations = -> [Mirrored008,Mirrored009]
FEATURE [Sketcher::SketchObject] Sketch157  label="ht sensor tunnel 60"
  AttachmentOffset = pos=(0,0,-61) rot=(0,0,1;0rad)
  FullyConstrained = true
  MapMode = 5
  Placement = pos=(-61,1.35e-14,-1.35e-14) rot=(0.57735,0.57735,0.57735;2.0944rad)
  Support = -> [YZ_Plane014]
  sketch-geometry (2):
    g0: ArcOfCircle CenterX=-11.5 CenterY=-25 CenterZ=0 NormalX=0 NormalY=0 NormalZ=1 AngleXU=0 Radius=2.4 StartAngle=4.03726 EndAngle=8.52911
    g1: LineSegment StartX=-13 StartY=-23.1265 StartZ=0 EndX=-13 EndY=-26.8735 EndZ=0
  constraints (7):
    c: Coincident(g1,g0)
    c: Coincident(g1,g0)
    c: Vertical(g1)
    c: DistanceX(g0,g-1) = 11.5
    c: DistanceY(g0,g-1) = 25
    c: Radius(g0) = 2.4
    c: DistanceX(g0,g0) = 1.5
FEATURE [Sketcher::SketchObject] Sketch158  label="ht sensor tunnel 55"
  AttachmentOffset = pos=(0,0,-55) rot=(0,0,1;0rad)
  FullyConstrained = true
  MapMode = 5
  Placement = pos=(-55,1.22e-14,-1.22e-14) rot=(0.57735,0.57735,0.57735;2.0944rad)
  Support = -> [YZ_Plane014]
  sketch-geometry (2):
    g0: ArcOfCircle CenterX=-11.5 CenterY=-25 CenterZ=0 NormalX=0 NormalY=0 NormalZ=1 AngleXU=0 Radius=2.4 StartAngle=4.03726 EndAngle=8.52911
    g1: LineSegment StartX=-13 StartY=-23.1265 StartZ=0 EndX=-13 EndY=-26.8735 EndZ=0
  constraints (7):
    c: Coincident(g1,g0)
    c: Coincident(g1,g0)
    c: Vertical(g1)
    c: DistanceX(g0,g-1) = 11.5
    c: DistanceY(g0,g-1) = 25
    c: Radius(g0) = 2.4
    c: DistanceX(g0,g0) = 1.5
FEATURE [Sketcher::SketchObject] Sketch159  label="ht sensor tunnel 53"
  AttachmentOffset = pos=(0,0,-53) rot=(0,0,1;0rad)
  FullyConstrained = true
  MapMode = 5
  Placement = pos=(-53,1.18e-14,-1.18e-14) rot=(0.57735,0.57735,0.57735;2.0944rad)
  Support = -> [YZ_Plane014]
  sketch-geometry (2):
    g0: ArcOfCircle CenterX=-11.5 CenterY=-25 CenterZ=0 NormalX=0 NormalY=0 NormalZ=1 AngleXU=0 Radius=4 StartAngle=4.32799 EndAngle=8.23838
    g1: LineSegment StartX=-13 StartY=-21.2919 StartZ=0 EndX=-13 EndY=-28.7081 EndZ=0
  constraints (7):
    c: Coincident(g1,g0)
    c: Coincident(g1,g0)
    c: Vertical(g1)
    c: DistanceX(g0,g-1) = 11.5
    c: DistanceY(g0,g-1) = 25
    c: Radius(g0) = 4
    c: DistanceX(g0,g0) = 1.5
FEATURE [Sketcher::SketchObject] Sketch160  label="ht sensor tunnel 37"
  AttachmentOffset = pos=(0,0,-37) rot=(0,0,1;0rad)
  FullyConstrained = true
  MapMode = 5
  Placement = pos=(-37,8.2e-15,-8.2e-15) rot=(0.57735,0.57735,0.57735;2.0944rad)
  Support = -> [YZ_Plane014]
  sketch-geometry (2):
    g0: ArcOfCircle CenterX=-11.5 CenterY=-25 CenterZ=0 NormalX=0 NormalY=0 NormalZ=1 AngleXU=0 Radius=4 StartAngle=4.32799 EndAngle=8.23838
    g1: LineSegment StartX=-13 StartY=-21.2919 StartZ=0 EndX=-13 EndY=-28.7081 EndZ=0
  constraints (7):
    c: Coincident(g1,g0)
    c: Coincident(g1,g0)
    c: Vertical(g1)
    c: DistanceX(g0,g-1) = 11.5
    c: DistanceY(g0,g-1) = 25
    c: Radius(g0) = 4
    c: DistanceX(g0,g0) = 1.5
FEATURE [PartDesign::SubtractiveLoft] SubtractiveLoft009  label="HT Sensor tunnel"
  BaseFeature = -> MultiTransform001
  Closed = false
  Profile = -> Sketch157
  Ruled = true
  Sections = -> [Sketch158,Sketch159,Sketch160]
FEATURE [Sketcher::SketchObject] Sketch161  label="ht esp vent crs"
  AttachmentOffset = pos=(0,0,-45) rot=(0,0,1;0rad)
  FullyConstrained = true
  MapMode = 5
  Placement = pos=(0,0,-45) rot=(0,0,1;0rad)
  Support = -> [XY_Plane014]
  sketch-geometry (5):
    g0: ArcOfCircle CenterX=7 CenterY=-11 CenterZ=0 NormalX=0 NormalY=0 NormalZ=1 AngleXU=0 Radius=0.65 StartAngle=6e-16 EndAngle=3.14159
    g1: ArcOfCircle CenterX=7 CenterY=-19 CenterZ=0 NormalX=0 NormalY=0 NormalZ=1 AngleXU=0 Radius=0.65 StartAngle=3.14159 EndAngle=6.28319
    g2: LineSegment StartX=6.35 StartY=-11 StartZ=0 EndX=6.35 EndY=-19 EndZ=0
    g3: LineSegment StartX=7.65 StartY=-11 StartZ=0 EndX=7.65 EndY=-19 EndZ=0
    g4: LineSegment StartX=6.35 StartY=-15 StartZ=0 EndX=7.65 EndY=-15 EndZ=0
  constraints (13):
    c: Tangent(g0,g3)
    c: Tangent(g0,g2)
    c: Tangent(g2,g1)
    c: Tangent(g3,g1)
    c: Vertical(g2)
    c: Equal(g0,g1)
    c: DistanceY(g1,g0) = 8
    c: DistanceX(g0,g0) = 1.3
    c: PointOnObject(g4,g2)
    c: PointOnObject(g4,g3)
    c: Symmetric(g0,g1,g4)
    c: DistanceX(g0) = 7
    c: DistanceY(g4,g-1) = 15
FEATURE [Sketcher::SketchObject] Sketch162  label="ht esp vent trj"
  AttachmentOffset = pos=(0,0,7) rot=(0,0,1;0rad)
  FullyConstrained = true
  MapMode = 5
  Placement = pos=(7,-1.6e-15,1.6e-15) rot=(0.57735,0.57735,0.57735;2.0944rad)
  Support = -> [YZ_Plane014]
  sketch-geometry (3):
    g0: LineSegment StartX=-22.5 StartY=-28 StartZ=0 EndX=-19.5 EndY=-28 EndZ=0
    g1: LineSegment StartX=-15 StartY=-32.5 StartZ=0 EndX=-15 EndY=-45 EndZ=0
    g2: ArcOfCircle CenterX=-19.5 CenterY=-32.5 CenterZ=0 NormalX=0 NormalY=0 NormalZ=1 AngleXU=0 Radius=4.5 StartAngle=-9e-16 EndAngle=1.5708
  constraints (9):
    c: Horizontal(g0)
    c: Vertical(g1)
    c: Tangent(g1,g2) = 1.5708
    c: Tangent(g0,g2) = 1.5708
    c: DistanceX(g0,g-1) = 22.5
    c: DistanceY(g0,g-1) = 28
    c: DistanceY(g1,g-1) = 45
    c: DistanceX(g0,g0) = 3
    c: DistanceX(g1,g-1) = 15
FEATURE [PartDesign::SubtractivePipe] SubtractivePipe008  label="HT ESP vent hole 1"
  AuxilleryCurvelinear = true
  AuxillerySpineTangent = false
  BaseFeature = -> SubtractiveLoft009
  Binormal = (0,0,0)
  Mode = 0
  Profile = -> Sketch161
  Spine = -> Sketch162
  SpineTangent = false
  Transformation = 0
  Transition = 0
FEATURE [PartDesign::LinearPattern] LinearPattern011  label="HT ESP vent holes 2..9"
  BaseFeature = -> SubtractivePipe008
  Direction = -> X_Axis014
  Length = 19
  Occurrences = 9
  Originals = -> [SubtractivePipe008]
FEATURE [Sketcher::SketchObject] Sketch163  label="ht SensorVentSketch"
  FullyConstrained = true
  MapMode = 5
  Support = -> [XY_Plane014]
  sketch-geometry (1):
    g0: LineSegment StartX=-61 StartY=-16.7 StartZ=0 EndX=-53.3745 EndY=-19.119 EndZ=0
  constraints (4):
    c: DistanceX(g0,g-1) = 61
    c: DistanceY(g0,g-1) = 16.7
    c: Angle(g0,g-1) = 0.307178
    c: Distance(g0) = 8
FEATURE [PartDesign::Line] DatumLine  label="ht SensorVentLine"
  AttacherType = Attacher::AttachEngineLine
  Length = 20
  MapMode = 29
  Placement = pos=(-10.3903,-32.7543,0) rot=(0.694826,0.508536,0.508536;1.9271rad)
  ResizeMode = 0
  Support = -> [Sketch163]
FEATURE [Sketcher::SketchObject] Sketch164  label="ht vent holes dallas ver"
  AttachmentOffset = pos=(0,0,11.5) rot=(0,0,1;0rad)
  FullyConstrained = true
  MapMode = 5
  Placement = pos=(0,-11.5,-2.6e-15) rot=(1,0,0;1.5708rad)
  Support = -> [XZ_Plane014]
  sketch-geometry (34):
    g0: Ellipse CenterX=-58 CenterY=-25 CenterZ=0 NormalX=0 NormalY=0 NormalZ=1 MajorRadius=5.5 MinorRadius=4.75 AngleXU=0
    g1: LineSegment StartX=-52.5 StartY=-25 StartZ=0 EndX=-63.5 EndY=-25 EndZ=0
    g2: LineSegment StartX=-58 StartY=-20.25 StartZ=0 EndX=-58 EndY=-29.75 EndZ=0
    g3: GeomPoint X=-55.2274 Y=-25 Z=0
    g4: GeomPoint X=-60.7726 Y=-25 Z=0
    g5: ArcOfCircle CenterX=-62 CenterY=-22.4522 CenterZ=0 NormalX=0 NormalY=0 NormalZ=1 AngleXU=0 Radius=0.5 StartAngle=3.3e-15 EndAngle=3.14159
    g6: ArcOfCircle CenterX=-62 CenterY=-27.5478 CenterZ=0 NormalX=0 NormalY=0 NormalZ=1 AngleXU=0 Radius=0.5 StartAngle=3.14159 EndAngle=6.28319
    g7: LineSegment StartX=-62.5 StartY=-22.4522 StartZ=0 EndX=-62.5 EndY=-27.5478 EndZ=0
    g8: LineSegment StartX=-61.5 StartY=-22.4522 StartZ=0 EndX=-61.5 EndY=-27.5478 EndZ=0
    g9: ArcOfCircle CenterX=-60 CenterY=-21.1056 CenterZ=0 NormalX=0 NormalY=0 NormalZ=1 AngleXU=0 Radius=0.5 StartAngle=8e-16 EndAngle=3.14159
    g10: ArcOfCircle CenterX=-60 CenterY=-28.8944 CenterZ=0 NormalX=0 NormalY=0 NormalZ=1 AngleXU=0 Radius=0.5 StartAngle=3.14159 EndAngle=6.28319
    g11: LineSegment StartX=-60.5 StartY=-21.1056 StartZ=0 EndX=-60.5 EndY=-28.8944 EndZ=0
    g12: LineSegment StartX=-59.5 StartY=-21.1056 StartZ=0 EndX=-59.5 EndY=-28.8944 EndZ=0
    g13: ArcOfCircle CenterX=-58 CenterY=-20.75 CenterZ=0 NormalX=0 NormalY=0 NormalZ=1 AngleXU=0 Radius=0.5 StartAngle=6e-16 EndAngle=3.14159
    g14: ArcOfCircle CenterX=-58 CenterY=-29.25 CenterZ=0 NormalX=0 NormalY=0 NormalZ=1 AngleXU=0 Radius=0.5 StartAngle=3.14159 EndAngle=6.28319
    g15: LineSegment StartX=-58.5 StartY=-20.75 StartZ=0 EndX=-58.5 EndY=-29.25 EndZ=0
    g16: LineSegment StartX=-57.5 StartY=-20.75 StartZ=0 EndX=-57.5 EndY=-29.25 EndZ=0
    g17: ArcOfCircle CenterX=-56 CenterY=-21.1056 CenterZ=0 NormalX=0 NormalY=0 NormalZ=1 AngleXU=0 Radius=0.5 StartAngle=2.9e-15 EndAngle=3.14159
    g18: ArcOfCircle CenterX=-56 CenterY=-28.8944 CenterZ=0 NormalX=0 NormalY=0 NormalZ=1 AngleXU=0 Radius=0.5 StartAngle=3.14159 EndAngle=6.28319
    g19: LineSegment StartX=-56.5 StartY=-21.1056 StartZ=0 EndX=-56.5 EndY=-28.8944 EndZ=0
    g20: LineSegment StartX=-55.5 StartY=-21.1056 StartZ=0 EndX=-55.5 EndY=-28.8944 EndZ=0
    g21: ArcOfCircle CenterX=-54 CenterY=-22.4522 CenterZ=0 NormalX=0 NormalY=0 NormalZ=1 AngleXU=0 Radius=0.5 StartAngle=3.4e-15 EndAngle=3.14159
    g22: ArcOfCircle CenterX=-54 CenterY=-27.5478 CenterZ=0 NormalX=0 NormalY=0 NormalZ=1 AngleXU=0 Radius=0.5 StartAngle=3.14159 EndAngle=6.28319
    g23: LineSegment StartX=-54.5 StartY=-22.4522 StartZ=0 EndX=-54.5 EndY=-27.5478 EndZ=0
    g24: LineSegment StartX=-53.5 StartY=-22.4522 StartZ=0 EndX=-53.5 EndY=-27.5478 EndZ=0
    g25: LineSegment StartX=-61.5 StartY=-25 StartZ=0 EndX=-60.5 EndY=-25 EndZ=0
    g26: LineSegment StartX=-59.5 StartY=-25 StartZ=0 EndX=-58.5 EndY=-25 EndZ=0
    g27: LineSegment StartX=-57.5 StartY=-25 StartZ=0 EndX=-56.5 EndY=-25 EndZ=0
    g28: LineSegment StartX=-55.5 StartY=-25 StartZ=0 EndX=-54.5 EndY=-25 EndZ=0
    g29: GeomPoint X=-53.625 Y=-22.1214 Z=0
    g30: GeomPoint X=-55.8258 Y=-20.6369 Z=0
    g31: GeomPoint X=-58 Y=-20.25 Z=0
    g32: GeomPoint X=-60.1742 Y=-20.6369 Z=0
    g33: GeomPoint X=-62.375 Y=-22.1214 Z=0
  constraints (77):
    c: InternalAlignment(g1-g4 -> g0) x4
    c: DistanceX(g0,g-1) = 58
    c: DistanceY(g1,g-1) = 25
    c: DistanceY(g2,g2) = 9.5
    c: DistanceX(g1,g1) = 11
    c: Tangent(g5,g8) = 1.5708
    c: Tangent(g5,g7) = -1.5708
    c: Tangent(g7,g6) = -1.5708
    c: Tangent(g8,g6) = 1.5708
    c: Vertical(g7)
    c: Equal(g5,g6)
    c: Tangent(g9,g12) = 1.5708
    c: Tangent(g9,g11) = -1.5708
    c: Tangent(g11,g10) = -1.5708
    c: Tangent(g12,g10) = 1.5708
    c: Vertical(g11)
    c: Tangent(g13,g16) = 1.5708
    c: Tangent(g13,g15) = -1.5708
    c: Tangent(g15,g14) = -1.5708
    c: Tangent(g16,g14) = 1.5708
    c: Vertical(g15)
    c: PointOnObject(g13,g2)
    c: Tangent(g17,g20) = 1.5708
    c: Tangent(g17,g19) = -1.5708
    c: Tangent(g19,g18) = -1.5708
    c: Tangent(g20,g18) = 1.5708
    c: Vertical(g19)
    c: Tangent(g21,g24) = 1.5708
    c: Tangent(g21,g23) = -1.5708
    c: Tangent(g23,g22) = -1.5708
    c: Tangent(g24,g22) = 1.5708
    c: Vertical(g23)
    c: Equal(g5,g9)
    c: Equal(g9,g13)
    c: Equal(g13,g17)
    c: Equal(g17,g21)
    c: DistanceX(g21,g21) = 1
    c: Symmetric(g22,g21,g1)
    c: Symmetric(g17,g18,g1)
    c: Symmetric(g13,g14,g1)
    c: Symmetric(g9,g10,g1)
    c: Symmetric(g6,g5,g1)
    c: PointOnObject(g25,g8)
    c: PointOnObject(g25,g11)
    c: Horizontal(g25)
    c: PointOnObject(g26,g12)
    c: PointOnObject(g26,g15)
    c: Horizontal(g26)
    c: PointOnObject(g27,g16)
    c: PointOnObject(g27,g19)
    c: Horizontal(g27)
    c: PointOnObject(g28,g20)
    c: PointOnObject(g28,g23)
    c: Horizontal(g28)
    c: Equal(g28,g27)
    c: Equal(g27,g26)
    c: Equal(g26,g25)
    c: DistanceX(g5,g21) = 9
    c: PointOnObject(g29,g0)
    c: PointOnObject(g29,g21)
    c: Tangent(g0,g21,g29) = -1.5708
    c: PointOnObject(g30,g0)
    c: PointOnObject(g30,g17)
    c: Tangent(g0,g17,g30) = -1.5708
    c: PointOnObject(g31,g0)
    c: PointOnObject(g31,g13)
    c: Tangent(g0,g13,g31) = -1.5708
    c: PointOnObject(g32,g0)
    c: PointOnObject(g32,g9)
    c: Tangent(g0,g9,g32) = -1.5708
    c: PointOnObject(g33,g0)
    c: PointOnObject(g33,g5)
    c: Tangent(g0,g5,g33) = -1.5708
    c: PointOnObject(g25,g1)
    c: PointOnObject(g26,g1)
    c: PointOnObject(g27,g1)
    c: PointOnObject(g28,g1)
FEATURE [Sketcher::SketchObject] Sketch165  label="ht vent holes dallas hor"
  AttachmentOffset = pos=(0,0,-25) rot=(0,0,1;0rad)
  ExternalGeometry = -> [Sketch164]
  FullyConstrained = true
  MapMode = 5
  Placement = pos=(0,0,-25) rot=(0,0,1;0rad)
  Support = -> [XY_Plane014]
  sketch-geometry (25):
    g0: ArcOfCircle CenterX=-62 CenterY=-14.5 CenterZ=0 NormalX=0 NormalY=0 NormalZ=1 AngleXU=0 Radius=0.5 StartAngle=3.14159 EndAngle=6.28319
    g1: ArcOfCircle CenterX=-62 CenterY=-10.5 CenterZ=0 NormalX=0 NormalY=0 NormalZ=1 AngleXU=0 Radius=0.5 StartAngle=-9e-16 EndAngle=3.14159
    g2: LineSegment StartX=-61.5 StartY=-14.5 StartZ=0 EndX=-61.5 EndY=-10.5 EndZ=0
    g3: LineSegment StartX=-62.5 StartY=-14.5 StartZ=0 EndX=-62.5 EndY=-10.5 EndZ=0
    g4: ArcOfCircle CenterX=-60 CenterY=-15.1887 CenterZ=0 NormalX=0 NormalY=0 NormalZ=1 AngleXU=0 Radius=0.5 StartAngle=3.14159 EndAngle=6.28319
    g5: ArcOfCircle CenterX=-60 CenterY=-10.5 CenterZ=0 NormalX=0 NormalY=0 NormalZ=1 AngleXU=0 Radius=0.5 StartAngle=-9e-16 EndAngle=3.14159
    g6: LineSegment StartX=-59.5 StartY=-15.1887 StartZ=0 EndX=-59.5 EndY=-10.5 EndZ=0
    g7: LineSegment StartX=-60.5 StartY=-15.1887 StartZ=0 EndX=-60.5 EndY=-10.5 EndZ=0
    g8: ArcOfCircle CenterX=-58 CenterY=-15.8773 CenterZ=0 NormalX=0 NormalY=0 NormalZ=1 AngleXU=0 Radius=0.5 StartAngle=3.14159 EndAngle=6.28319
    g9: ArcOfCircle CenterX=-58 CenterY=-10.5 CenterZ=0 NormalX=0 NormalY=0 NormalZ=1 AngleXU=0 Radius=0.5 StartAngle=0 EndAngle=3.14159
    g10: LineSegment StartX=-57.5 StartY=-15.8773 StartZ=0 EndX=-57.5 EndY=-10.5 EndZ=0
    g11: LineSegment StartX=-58.5 StartY=-15.8773 StartZ=0 EndX=-58.5 EndY=-10.5 EndZ=0
    g12: ArcOfCircle CenterX=-56 CenterY=-16.566 CenterZ=0 NormalX=0 NormalY=0 NormalZ=1 AngleXU=0 Radius=0.5 StartAngle=3.14159 EndAngle=6.28319
    g13: ArcOfCircle CenterX=-56 CenterY=-10.5 CenterZ=0 NormalX=0 NormalY=0 NormalZ=1 AngleXU=0 Radius=0.5 StartAngle=3e-16 EndAngle=3.14159
    g14: LineSegment StartX=-55.5 StartY=-16.566 StartZ=0 EndX=-55.5 EndY=-10.5 EndZ=0
    g15: LineSegment StartX=-56.5 StartY=-16.566 StartZ=0 EndX=-56.5 EndY=-10.5 EndZ=0
    g16: ArcOfCircle CenterX=-54 CenterY=-17.2546 CenterZ=0 NormalX=0 NormalY=0 NormalZ=1 AngleXU=0 Radius=0.5 StartAngle=3.14159 EndAngle=6.28319
    g17: ArcOfCircle CenterX=-54 CenterY=-10.5 CenterZ=0 NormalX=0 NormalY=0 NormalZ=1 AngleXU=0 Radius=0.5 StartAngle=1.1e-15 EndAngle=3.14159
    g18: LineSegment StartX=-53.5 StartY=-17.2546 StartZ=0 EndX=-53.5 EndY=-10.5 EndZ=0
    g19: LineSegment StartX=-54.5 StartY=-17.2546 StartZ=0 EndX=-54.5 EndY=-10.5 EndZ=0
    g20: LineSegment StartX=-61.5 StartY=-10.5 StartZ=0 EndX=-60.5 EndY=-10.5 EndZ=0
    g21: LineSegment StartX=-59.5 StartY=-10.5 StartZ=0 EndX=-58.5 EndY=-10.5 EndZ=0
    g22: LineSegment StartX=-57.5 StartY=-10.5 StartZ=0 EndX=-56.5 EndY=-10.5 EndZ=0
    g23: LineSegment StartX=-55.5 StartY=-10.5 StartZ=0 EndX=-54.5 EndY=-10.5 EndZ=0
    g24: LineSegment StartX=-62.1628 StartY=-14.9728 StartZ=0 EndX=-54.1628 EndY=-17.7274 EndZ=0
  constraints (60):
    c: Tangent(g0,g3) = 1.5708
    c: Tangent(g0,g2) = -1.5708
    c: Tangent(g2,g1) = -1.5708
    c: Tangent(g3,g1) = 1.5708
    c: Vertical(g2)
    c: Equal(g0,g1)
    c: Tangent(g4,g7) = 1.5708
    c: Tangent(g4,g6) = -1.5708
    c: Tangent(g6,g5) = -1.5708
    c: Tangent(g7,g5) = 1.5708
    c: Vertical(g6)
    c: Equal(g4,g5)
    c: Tangent(g8,g11) = 1.5708
    c: Tangent(g8,g10) = -1.5708
    c: Tangent(g10,g9) = -1.5708
    c: Tangent(g11,g9) = 1.5708
    c: Vertical(g10)
    c: Equal(g8,g9)
    c: Tangent(g12,g15) = 1.5708
    c: Tangent(g12,g14) = -1.5708
    c: Tangent(g14,g13) = -1.5708
    c: Tangent(g15,g13) = 1.5708
    c: Vertical(g14)
    c: Equal(g12,g13)
    c: Tangent(g16,g19) = 1.5708
    c: Tangent(g16,g18) = -1.5708
    c: Tangent(g18,g17) = -1.5708
    c: Tangent(g19,g17) = 1.5708
    c: Vertical(g18)
    c: Equal(g16,g17)
    c: PointOnObject(g-3,g18)
    c: PointOnObject(g-4,g3)
    c: Equal(g1,g5)
    c: Equal(g5,g9)
    c: Equal(g9,g13)
    c: Equal(g13,g17)
    c: Coincident(g20,g1)
    c: Coincident(g20,g5)
    c: Coincident(g21,g5)
    c: Coincident(g21,g9)
    c: Coincident(g22,g9)
    c: Coincident(g22,g13)
    c: Coincident(g23,g13)
    c: Coincident(g23,g17)
    c: Horizontal(g23)
    c: Equal(g23,g22)
    c: Equal(g22,g21)
    c: Equal(g21,g20)
    c: Horizontal(g21)
    c: Horizontal(g22)
    c: DistanceX(g17,g17) = 1
    c: Tangent(g24,g0) = -1.5708
    c: Tangent(g24,g16) = -1.5708
    c: Tangent(g12,g24)
    c: DistanceY(g0,g-1) = 14.5
    c: Angle(g24,g-1) = 0.331613
    c: Tangent(g4,g24)
    c: Tangent(g8,g24)
    c: Horizontal(g20)
    c: DistanceY(g1,g-1) = 10.5
FEATURE [PartDesign::Pocket] Pocket038  label="HT Vent holes Dallas ver"
  BaseFeature = -> LinearPattern011
  Length = 5
  Length2 = 100
  Profile = -> Sketch164
  Reversed = true
  Type = 1
FEATURE [PartDesign::Pocket] Pocket039  label="HT Vent holes Dallas hor"
  BaseFeature = -> Pocket038
  Length = 5
  Length2 = 100
  Profile = -> Sketch165
  Type = 1
FEATURE [Sketcher::SketchObject] Sketch166  label="ht temp pocket for Dallas pillar"
  AttachmentOffset = pos=(0,0,19.5) rot=(0,0,1;0rad)
  FullyConstrained = true
  MapMode = 5
  Placement = pos=(0,-19.5,-4.3e-15) rot=(1,0,0;1.5708rad)
  Support = -> [XZ_Plane014]
  sketch-geometry (14):
    g0: LineSegment StartX=-31.75 StartY=-24 StartZ=0 EndX=-28.65 EndY=-24 EndZ=0
    g1: LineSegment StartX=-27.45 StartY=-25.2 StartZ=0 EndX=-27.45 EndY=-32.8 EndZ=0
    g2: LineSegment StartX=-28.65 StartY=-34 StartZ=0 EndX=-31.75 EndY=-34 EndZ=0
    g3: LineSegment StartX=-32.95 StartY=-32.8 StartZ=0 EndX=-32.95 EndY=-25.2 EndZ=0
    g4: LineSegment StartX=-31.75 StartY=-25.2 StartZ=0 EndX=-28.65 EndY=-25.2 EndZ=0
    g5: LineSegment StartX=-28.65 StartY=-25.2 StartZ=0 EndX=-28.65 EndY=-32.8 EndZ=0
    g6: LineSegment StartX=-28.65 StartY=-32.8 StartZ=0 EndX=-31.75 EndY=-32.8 EndZ=0
    g7: LineSegment StartX=-31.75 StartY=-32.8 StartZ=0 EndX=-31.75 EndY=-25.2 EndZ=0
    g8: LineSegment StartX=-31.75 StartY=-29 StartZ=0 EndX=-28.65 EndY=-29 EndZ=0
    g9: LineSegment StartX=-30.2 StartY=-25.2 StartZ=0 EndX=-30.2 EndY=-32.8 EndZ=0
    g10: ArcOfCircle CenterX=-28.65 CenterY=-25.2 CenterZ=0 NormalX=0 NormalY=0 NormalZ=1 AngleXU=0 Radius=1.2 StartAngle=1.844e-13 EndAngle=1.5708
    g11: ArcOfCircle CenterX=-31.75 CenterY=-25.2 CenterZ=0 NormalX=0 NormalY=0 NormalZ=1 AngleXU=0 Radius=1.2 StartAngle=1.5708 EndAngle=3.14159
    g12: ArcOfCircle CenterX=-31.75 CenterY=-32.8 CenterZ=0 NormalX=0 NormalY=0 NormalZ=1 AngleXU=0 Radius=1.2 StartAngle=3.14159 EndAngle=4.71239
    g13: ArcOfCircle CenterX=-28.65 CenterY=-32.8 CenterZ=0 NormalX=0 NormalY=0 NormalZ=1 AngleXU=0 Radius=1.2 StartAngle=4.71239 EndAngle=6.28319
  constraints (34):
    c: Horizontal(g0)
    c: Horizontal(g2)
    c: Vertical(g1)
    c: Vertical(g3)
    c: Coincident(g4,g5)
    c: Coincident(g5,g6)
    c: Coincident(g6,g7)
    c: Coincident(g7,g4)
    c: Horizontal(g4)
    c: Horizontal(g6)
    c: Vertical(g5)
    c: PointOnObject(g8,g7)
    c: PointOnObject(g8,g5)
    c: PointOnObject(g9,g6)
    c: Vertical(g9)
    c: Symmetric(g4,g4,g9)
    c: Symmetric(g5,g4,g8)
    c: DistanceX(g9,g-1) = 30.2
    c: DistanceY(g8,g-1) = 29
    c: Tangent(g0,g10) = 1.5708
    c: Tangent(g1,g10) = 1.5708
    c: Tangent(g3,g11) = 1.5708
    c: Tangent(g0,g11) = 1.5708
    c: Tangent(g2,g12) = 1.5708
    c: Tangent(g3,g12) = 1.5708
    c: Tangent(g2,g13) = 1.5708
    c: Tangent(g1,g13) = 1.5708
    c: Coincident(g4,g10)
    c: Coincident(g4,g11)
    c: Coincident(g6,g12)
    c: Coincident(g5,g13)
    c: DistanceY(g2,g0) = 10
    c: Radius(g10) = 1.2
    c: DistanceX(g3,g1) = 5.5
FEATURE [PartDesign::Pocket] Pocket040  label="HT Temp pocket for Dallas pillar"
  BaseFeature = -> Pocket039
  Length = 5
  Length2 = 100
  Profile = -> Sketch166
  Type = 1
FEATURE [PartDesign::Body] Body014  label="HousingTop"
  Group = -> [Sketch059,Pad012,DatumPlane001,SubtractivePipe006,Fillet,SubtractiveLoft001,Fillet004,LinearPattern001,Sketch061,Sketch060,Sketch062,Pocket010,SubtractiveLoft008,Sketch065,SubtractivePipe,Sketch071,Sketch072,SubtractiveLoft,Sketch073,Pocket016,Sketch074,Pocket017,Sketch075,Sketch076,Sketch103,Groove003,MultiTransform001,Mirrored008,Mirrored009,Sketch136,Sketch150,Sketch151,Sketch157,Sketch158,+15 more]
  Origin = -> Origin014
  Tip = -> Pocket040
FEATURE [Part::Feature] Compound004  label="Display001"
  Placement = pos=(0,-20.5,0) rot=(0,0,1;0rad)
  shape: bbox 77.18 x 8.8 x 42.9 mm, 49 faces, 4 solids (baked)
FEATURE [Part::Feature] Screw005  label="M5x10-Screw007"
  Placement = pos=(41,-20,14) rot=(1,0,0;1.5708rad)
  shape: bbox 9.5 x 12.75 x 9.5 mm, 16 faces (baked)
FEATURE [Part::Feature] Screw001001  label="M5x10-Screw008"
  Placement = pos=(41,-20,0) rot=(1,0,0;1.5708rad)
  shape: bbox 9.5 x 12.75 x 9.5 mm, 16 faces (baked)
FEATURE [Part::Feature] Screw002001  label="M5x10-Screw009"
  Placement = pos=(41,-20,-14) rot=(1,0,0;1.5708rad)
  shape: bbox 9.5 x 12.75 x 9.5 mm, 16 faces (baked)
FEATURE [Part::Feature] Body007001  label="WallPlate001"
  shape: bbox 140 x 7 x 90 mm, 97 faces (baked)
FEATURE [Part::Feature] Body013001  label="HousingBottom001"
  shape: bbox 145 x 37.72 x 123 mm, 288 faces (baked)
FEATURE [Part::Feature] Body014001  label="HousingTop001"
  shape: bbox 144.9 x 18.86 x 123 mm, 365 faces (baked)
FEATURE [Part::Compound] Compound005  label="RotatedView"
  Links = -> [Compound004,Screw005,Screw001001,Screw002001,Body007001,Body013001,Body014001]
  Placement = pos=(0,0,0) rot=(0.568657,0.074865,-0.819161;0.936324rad)
FEATURE [Drawing::FeatureViewPart] View  label="Rotated"
  Direction = (0,-1,0)
  HiddenWidth = 0.15
  LineWidth = 0.35
  Rotation = 90
  ShowHiddenLines = false
  ShowSmoothLines = false
  Source = -> Compound005
  Tolerance = 0.05
  ViewResult = <blob: 37968 chars omitted>
  Visible = false
  X = 120
  Y = 220
FEATURE [Part::Feature] Screw002002  label="M5x10-Screw010"
  Placement = pos=(41,-20,14) rot=(1,0,0;1.5708rad)
  shape: bbox 9.5 x 12.75 x 9.5 mm, 16 faces (baked)
FEATURE [Part::Feature] Screw002003  label="M5x10-Screw011"
  Placement = pos=(41,-20,-14) rot=(1,0,0;1.5708rad)
  shape: bbox 9.5 x 12.75 x 9.5 mm, 16 faces (baked)
FEATURE [Part::Feature] Screw002004  label="M5x10-Screw012"
  Placement = pos=(41,-20,0) rot=(1,0,0;1.5708rad)
  shape: bbox 9.5 x 12.75 x 9.5 mm, 16 faces (baked)
FEATURE [Part::Feature] Body014002  label="HousingBottom002"
  shape: bbox 145 x 37.72 x 123 mm, 288 faces (baked)
FEATURE [Part::Feature] Body014003  label="HousingTop002"
  shape: bbox 144.9 x 18.86 x 123 mm, 365 faces (baked)
FEATURE [Part::Feature] Body014004  label="WallPlate002"
  shape: bbox 140 x 7 x 90 mm, 97 faces (baked)
FEATURE [Part::Feature] Compound007  label="Display002"
  Placement = pos=(0,-20.5,0) rot=(0,0,1;0rad)
  shape: bbox 77.18 x 8.8 x 42.9 mm, 49 faces, 4 solids (baked)
FEATURE [Part::Compound] Compound006  label="FrontalView"
  Links = -> [Compound007,Screw002002,Screw002004,Screw002003,Body014004,Body014002,Body014003]
FEATURE [Drawing::FeatureViewPart] View001  label="Frontal"
  Direction = (0,-1,0)
  HiddenWidth = 0.15
  LineWidth = 0.35
  Rotation = 90
  ShowHiddenLines = false
  ShowSmoothLines = false
  Source = -> Compound006
  Tolerance = 0.05
  ViewResult = <blob: 43115 chars omitted>
  Visible = false
  X = 300
  Y = 120
FEATURE [Part::Feature] Screw002005  label="M5x10-Screw013"
  Placement = pos=(41,-20,14) rot=(1,0,0;1.5708rad)
  shape: bbox 9.5 x 12.75 x 9.5 mm, 16 faces (baked)
FEATURE [Part::Feature] Body014005  label="HousingTop003"
  shape: bbox 144.9 x 18.86 x 123 mm, 365 faces (baked)
FEATURE [Part::Feature] Screw002006  label="M5x10-Screw014"
  Placement = pos=(41,-20,0) rot=(1,0,0;1.5708rad)
  shape: bbox 9.5 x 12.75 x 9.5 mm, 16 faces (baked)
FEATURE [Part::Feature] Body014006  label="HousingBottom003"
  shape: bbox 145 x 37.72 x 123 mm, 288 faces (baked)
FEATURE [Part::Feature] Body014007  label="WallPlate003"
  Placement = pos=(0,45,0) rot=(0,0,1;0rad)
  shape: bbox 140 x 7 x 90 mm, 97 faces (baked)
FEATURE [Part::Feature] Screw002007  label="M5x10-Screw015"
  Placement = pos=(41,-20,-14) rot=(1,0,0;1.5708rad)
  shape: bbox 9.5 x 12.75 x 9.5 mm, 16 faces (baked)
FEATURE [Part::Feature] Compound009  label="Display003"
  Placement = pos=(0,-20.5,0) rot=(0,0,1;0rad)
  shape: bbox 77.18 x 8.8 x 42.9 mm, 49 faces, 4 solids (baked)
FEATURE [Part::Compound] Compound008  label="ExplodedView"
  Links = -> [Compound009,Screw002005,Screw002006,Screw002007,Body014007,Body014006,Body014005]
  Placement = pos=(0,0,0) rot=(0.641489,0.182535,-0.745099;0.956149rad)
FEATURE [Drawing::FeatureViewPart] View002  label="ExplodedView001"
  Direction = (0,-1,0)
  HiddenWidth = 0.15
  LineWidth = 0.35
  Rotation = 90
  ShowHiddenLines = false
  ShowSmoothLines = false
  Source = -> Compound008
  Tolerance = 0.05
  ViewResult = <blob: 44108 chars omitted>
  Visible = false
  X = 120
  Y = 110
FEATURE [Drawing::FeaturePage] Page
  EditableTexts = AUTHOR NAME | CREATION DATE | SUPERVISOR NAME | CHECK DATE | SCALE | WEIGHT | NUMBER | SHEET | TITLE | SUBTITLE
  Group = -> [View,View001,View002]
  Template = C:/Program Files/FreeCAD 0.19/data/Mod/Drawing/Templates/A3_Landscape.svg
